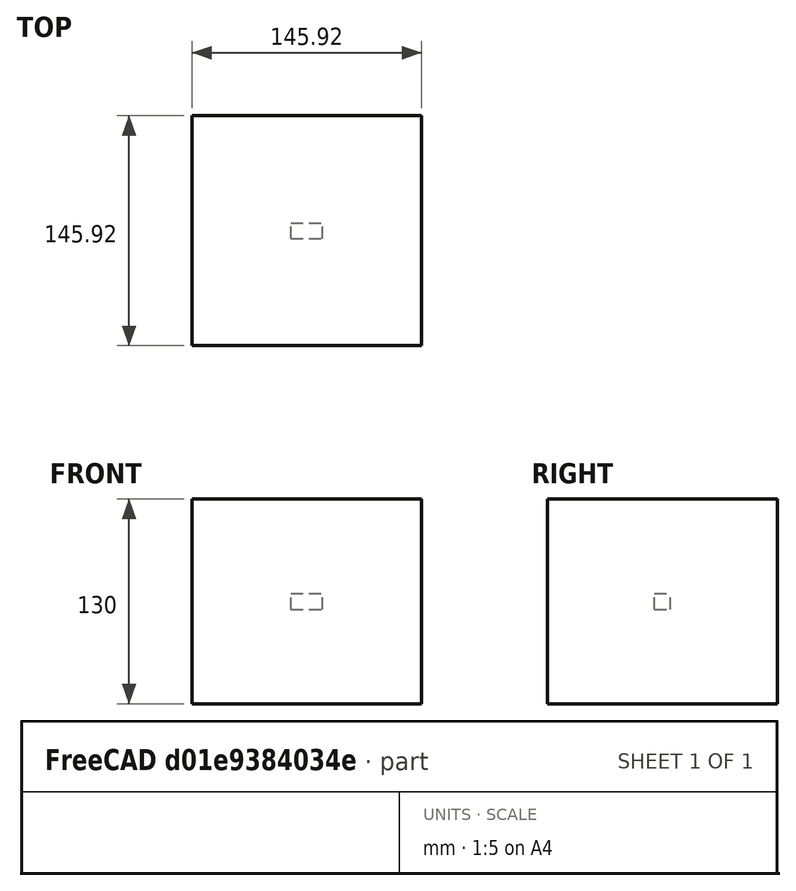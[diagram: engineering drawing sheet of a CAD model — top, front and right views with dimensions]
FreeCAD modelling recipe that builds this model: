
FCSTD DOCUMENT  (FreeCAD 0.20RUnknown)
Label: array-rotation-test-b
License: All rights reserved
objects: App::DocumentObjectGroupPython×1251, Part::FeaturePython×3, App::Part×3
note: 2 computed .brp shape members not serialized (recipe doc carries the construction recipe); baked Part::Feature solids carry a one-line shape summary decoded from their .brp

FEATURE [App::DocumentObjectGroupPython] HALFPI  # scripted group (container) (typed FeaturePython)
  name = HALFPI
  value = pi/2.
FEATURE [App::DocumentObjectGroupPython] PI  # scripted group (container) (typed FeaturePython)
  name = PI
  value = 1.*pi
FEATURE [App::DocumentObjectGroupPython] TWOPI  # scripted group (container) (typed FeaturePython)
  name = TWOPI
  value = 2.*pi
FEATURE [App::DocumentObjectGroupPython] Constants  # scripted group (container) (typed FeaturePython)
  Group = -> [HALFPI,PI,TWOPI]
FEATURE [App::DocumentObjectGroupPython] Variables  # scripted group (container) (typed FeaturePython)
FEATURE [App::DocumentObjectGroupPython] Quantities  # scripted group (container) (typed FeaturePython)
FEATURE [App::DocumentObjectGroupPython] Isotopes  # scripted group (container) (typed FeaturePython)
FEATURE [App::DocumentObjectGroupPython] Elements  # scripted group (container) (typed FeaturePython)
FEATURE [App::DocumentObjectGroupPython] Matrix  # scripted group (container) (typed FeaturePython)
FEATURE [App::DocumentObjectGroupPython] Surfaces  # scripted group (container) (typed FeaturePython)
FEATURE [App::DocumentObjectGroupPython] Opticals  # scripted group (container) (typed FeaturePython)
  Group = -> [Matrix,Surfaces]
FEATURE [App::DocumentObjectGroupPython] G4Isotopes  # scripted group (container) (typed FeaturePython)
FEATURE [App::DocumentObjectGroupPython] H_element  # scripted group (container) (typed FeaturePython)
  Z = 1
  atom_value = 1.008
  formula = H
  name = H_element
FEATURE [App::DocumentObjectGroupPython] He_element  # scripted group (container) (typed FeaturePython)
  Z = 2
  atom_value = 4.0026
  formula = He
  name = He_element
FEATURE [App::DocumentObjectGroupPython] Li_element  # scripted group (container) (typed FeaturePython)
  Z = 3
  atom_value = 6.94
  formula = Li
  name = Li_element
FEATURE [App::DocumentObjectGroupPython] Be_element  # scripted group (container) (typed FeaturePython)
  Z = 4
  atom_value = 9.01218
  formula = Be
  name = Be_element
FEATURE [App::DocumentObjectGroupPython] B_element  # scripted group (container) (typed FeaturePython)
  Z = 5
  atom_value = 10.81
  formula = B
  name = B_element
FEATURE [App::DocumentObjectGroupPython] C_element  # scripted group (container) (typed FeaturePython)
  Z = 6
  atom_value = 12.011
  formula = C
  name = C_element
FEATURE [App::DocumentObjectGroupPython] N_element  # scripted group (container) (typed FeaturePython)
  Z = 7
  atom_value = 14.007
  formula = N
  name = N_element
FEATURE [App::DocumentObjectGroupPython] O_element  # scripted group (container) (typed FeaturePython)
  Z = 8
  atom_value = 15.999
  formula = O
  name = O_element
FEATURE [App::DocumentObjectGroupPython] F_element  # scripted group (container) (typed FeaturePython)
  Z = 9
  atom_value = 18.9984
  formula = F
  name = F_element
FEATURE [App::DocumentObjectGroupPython] Ne_element  # scripted group (container) (typed FeaturePython)
  Z = 10
  atom_value = 20.1797
  formula = Ne
  name = Ne_element
FEATURE [App::DocumentObjectGroupPython] Na_element  # scripted group (container) (typed FeaturePython)
  Z = 11
  atom_value = 22.9898
  formula = Na
  name = Na_element
FEATURE [App::DocumentObjectGroupPython] Mg_element  # scripted group (container) (typed FeaturePython)
  Z = 12
  atom_value = 24.305
  formula = Mg
  name = Mg_element
FEATURE [App::DocumentObjectGroupPython] Al_element  # scripted group (container) (typed FeaturePython)
  Z = 13
  atom_value = 26.9815
  formula = Al
  name = Al_element
FEATURE [App::DocumentObjectGroupPython] Si_element  # scripted group (container) (typed FeaturePython)
  Z = 14
  atom_value = 28.085
  formula = Si
  name = Si_element
FEATURE [App::DocumentObjectGroupPython] P_element  # scripted group (container) (typed FeaturePython)
  Z = 15
  atom_value = 30.9738
  formula = P
  name = P_element
FEATURE [App::DocumentObjectGroupPython] S_element  # scripted group (container) (typed FeaturePython)
  Z = 16
  atom_value = 32.06
  formula = S
  name = S_element
FEATURE [App::DocumentObjectGroupPython] Cl_element  # scripted group (container) (typed FeaturePython)
  Z = 17
  atom_value = 35.45
  formula = Cl
  name = Cl_element
FEATURE [App::DocumentObjectGroupPython] Ar_element  # scripted group (container) (typed FeaturePython)
  Z = 18
  atom_value = 39.95
  formula = Ar
  name = Ar_element
FEATURE [App::DocumentObjectGroupPython] K_element  # scripted group (container) (typed FeaturePython)
  Z = 19
  atom_value = 39.0983
  formula = K
  name = K_element
FEATURE [App::DocumentObjectGroupPython] Ca_element  # scripted group (container) (typed FeaturePython)
  Z = 20
  atom_value = 40.078
  formula = Ca
  name = Ca_element
FEATURE [App::DocumentObjectGroupPython] Sc_element  # scripted group (container) (typed FeaturePython)
  Z = 21
  atom_value = 44.9559
  formula = Sc
  name = Sc_element
FEATURE [App::DocumentObjectGroupPython] Ti_element  # scripted group (container) (typed FeaturePython)
  Z = 22
  atom_value = 47.867
  formula = Ti
  name = Ti_element
FEATURE [App::DocumentObjectGroupPython] V_element  # scripted group (container) (typed FeaturePython)
  Z = 23
  atom_value = 50.9415
  formula = V
  name = V_element
FEATURE [App::DocumentObjectGroupPython] Cr_element  # scripted group (container) (typed FeaturePython)
  Z = 24
  atom_value = 51.9961
  formula = Cr
  name = Cr_element
FEATURE [App::DocumentObjectGroupPython] Mn_element  # scripted group (container) (typed FeaturePython)
  Z = 25
  atom_value = 54.938
  formula = Mn
  name = Mn_element
FEATURE [App::DocumentObjectGroupPython] Fe_element  # scripted group (container) (typed FeaturePython)
  Z = 26
  atom_value = 55.845
  formula = Fe
  name = Fe_element
FEATURE [App::DocumentObjectGroupPython] Co_element  # scripted group (container) (typed FeaturePython)
  Z = 27
  atom_value = 58.9332
  formula = Co
  name = Co_element
FEATURE [App::DocumentObjectGroupPython] Ni_element  # scripted group (container) (typed FeaturePython)
  Z = 28
  atom_value = 58.6934
  formula = Ni
  name = Ni_element
FEATURE [App::DocumentObjectGroupPython] Cu_element  # scripted group (container) (typed FeaturePython)
  Z = 29
  atom_value = 63.546
  formula = Cu
  name = Cu_element
FEATURE [App::DocumentObjectGroupPython] Zn_element  # scripted group (container) (typed FeaturePython)
  Z = 30
  atom_value = 65.38
  formula = Zn
  name = Zn_element
FEATURE [App::DocumentObjectGroupPython] Ga_element  # scripted group (container) (typed FeaturePython)
  Z = 31
  atom_value = 69.723
  formula = Ga
  name = Ga_element
FEATURE [App::DocumentObjectGroupPython] Ge_element  # scripted group (container) (typed FeaturePython)
  Z = 32
  atom_value = 72.63
  formula = Ge
  name = Ge_element
FEATURE [App::DocumentObjectGroupPython] As_element  # scripted group (container) (typed FeaturePython)
  Z = 33
  atom_value = 74.9216
  formula = As
  name = As_element
FEATURE [App::DocumentObjectGroupPython] Se_element  # scripted group (container) (typed FeaturePython)
  Z = 34
  atom_value = 78.971
  formula = Se
  name = Se_element
FEATURE [App::DocumentObjectGroupPython] Br_element  # scripted group (container) (typed FeaturePython)
  Z = 35
  atom_value = 79.904
  formula = Br
  name = Br_element
FEATURE [App::DocumentObjectGroupPython] Kr_element  # scripted group (container) (typed FeaturePython)
  Z = 36
  atom_value = 83.798
  formula = Kr
  name = Kr_element
FEATURE [App::DocumentObjectGroupPython] Rb_element  # scripted group (container) (typed FeaturePython)
  Z = 37
  atom_value = 85.4678
  formula = Rb
  name = Rb_element
FEATURE [App::DocumentObjectGroupPython] Sr_element  # scripted group (container) (typed FeaturePython)
  Z = 38
  atom_value = 87.62
  formula = Sr
  name = Sr_element
FEATURE [App::DocumentObjectGroupPython] Y_element  # scripted group (container) (typed FeaturePython)
  Z = 39
  atom_value = 88.9058
  formula = Y
  name = Y_element
FEATURE [App::DocumentObjectGroupPython] Zr_element  # scripted group (container) (typed FeaturePython)
  Z = 40
  atom_value = 91.224
  formula = Zr
  name = Zr_element
FEATURE [App::DocumentObjectGroupPython] Nb_element  # scripted group (container) (typed FeaturePython)
  Z = 41
  atom_value = 92.9064
  formula = Nb
  name = Nb_element
FEATURE [App::DocumentObjectGroupPython] Mo_element  # scripted group (container) (typed FeaturePython)
  Z = 42
  atom_value = 95.95
  formula = Mo
  name = Mo_element
FEATURE [App::DocumentObjectGroupPython] Tc_element  # scripted group (container) (typed FeaturePython)
  Z = 43
  atom_value = 97
  formula = Tc
  name = Tc_element
FEATURE [App::DocumentObjectGroupPython] Ru_element  # scripted group (container) (typed FeaturePython)
  Z = 44
  atom_value = 101.07
  formula = Ru
  name = Ru_element
FEATURE [App::DocumentObjectGroupPython] Rh_element  # scripted group (container) (typed FeaturePython)
  Z = 45
  atom_value = 102.905
  formula = Rh
  name = Rh_element
FEATURE [App::DocumentObjectGroupPython] Pd_element  # scripted group (container) (typed FeaturePython)
  Z = 46
  atom_value = 106.42
  formula = Pd
  name = Pd_element
FEATURE [App::DocumentObjectGroupPython] Ag_element  # scripted group (container) (typed FeaturePython)
  Z = 47
  atom_value = 107.868
  formula = Ag
  name = Ag_element
FEATURE [App::DocumentObjectGroupPython] Cd_element  # scripted group (container) (typed FeaturePython)
  Z = 48
  atom_value = 112.414
  formula = Cd
  name = Cd_element
FEATURE [App::DocumentObjectGroupPython] In_element  # scripted group (container) (typed FeaturePython)
  Z = 49
  atom_value = 114.818
  formula = In
  name = In_element
FEATURE [App::DocumentObjectGroupPython] Sn_element  # scripted group (container) (typed FeaturePython)
  Z = 50
  atom_value = 118.71
  formula = Sn
  name = Sn_element
FEATURE [App::DocumentObjectGroupPython] Sb_element  # scripted group (container) (typed FeaturePython)
  Z = 51
  atom_value = 121.76
  formula = Sb
  name = Sb_element
FEATURE [App::DocumentObjectGroupPython] Te_element  # scripted group (container) (typed FeaturePython)
  Z = 52
  atom_value = 127.6
  formula = Te
  name = Te_element
FEATURE [App::DocumentObjectGroupPython] I_element  # scripted group (container) (typed FeaturePython)
  Z = 53
  atom_value = 126.904
  formula = I
  name = I_element
FEATURE [App::DocumentObjectGroupPython] Xe_element  # scripted group (container) (typed FeaturePython)
  Z = 54
  atom_value = 131.293
  formula = Xe
  name = Xe_element
FEATURE [App::DocumentObjectGroupPython] Cs_element  # scripted group (container) (typed FeaturePython)
  Z = 55
  atom_value = 132.905
  formula = Cs
  name = Cs_element
FEATURE [App::DocumentObjectGroupPython] Ba_element  # scripted group (container) (typed FeaturePython)
  Z = 56
  atom_value = 137.327
  formula = Ba
  name = Ba_element
FEATURE [App::DocumentObjectGroupPython] La_element  # scripted group (container) (typed FeaturePython)
  Z = 57
  atom_value = 138.905
  formula = La
  name = La_element
FEATURE [App::DocumentObjectGroupPython] Ce_element  # scripted group (container) (typed FeaturePython)
  Z = 58
  atom_value = 140.116
  formula = Ce
  name = Ce_element
FEATURE [App::DocumentObjectGroupPython] Pr_element  # scripted group (container) (typed FeaturePython)
  Z = 59
  atom_value = 140.908
  formula = Pr
  name = Pr_element
FEATURE [App::DocumentObjectGroupPython] Nd_element  # scripted group (container) (typed FeaturePython)
  Z = 60
  atom_value = 144.242
  formula = Nd
  name = Nd_element
FEATURE [App::DocumentObjectGroupPython] Pm_element  # scripted group (container) (typed FeaturePython)
  Z = 61
  atom_value = 145
  formula = Pm
  name = Pm_element
FEATURE [App::DocumentObjectGroupPython] Sm_element  # scripted group (container) (typed FeaturePython)
  Z = 62
  atom_value = 150.36
  formula = Sm
  name = Sm_element
FEATURE [App::DocumentObjectGroupPython] Eu_element  # scripted group (container) (typed FeaturePython)
  Z = 63
  atom_value = 151.964
  formula = Eu
  name = Eu_element
FEATURE [App::DocumentObjectGroupPython] Gd_element  # scripted group (container) (typed FeaturePython)
  Z = 64
  atom_value = 157.25
  formula = Gd
  name = Gd_element
FEATURE [App::DocumentObjectGroupPython] Tb_element  # scripted group (container) (typed FeaturePython)
  Z = 65
  atom_value = 158.925
  formula = Tb
  name = Tb_element
FEATURE [App::DocumentObjectGroupPython] Dy_element  # scripted group (container) (typed FeaturePython)
  Z = 66
  atom_value = 162.5
  formula = Dy
  name = Dy_element
FEATURE [App::DocumentObjectGroupPython] Ho_element  # scripted group (container) (typed FeaturePython)
  Z = 67
  atom_value = 164.93
  formula = Ho
  name = Ho_element
FEATURE [App::DocumentObjectGroupPython] Er_element  # scripted group (container) (typed FeaturePython)
  Z = 68
  atom_value = 167.259
  formula = Er
  name = Er_element
FEATURE [App::DocumentObjectGroupPython] Tm_element  # scripted group (container) (typed FeaturePython)
  Z = 69
  atom_value = 168.934
  formula = Tm
  name = Tm_element
FEATURE [App::DocumentObjectGroupPython] Yb_element  # scripted group (container) (typed FeaturePython)
  Z = 70
  atom_value = 173.045
  formula = Yb
  name = Yb_element
FEATURE [App::DocumentObjectGroupPython] Lu_element  # scripted group (container) (typed FeaturePython)
  Z = 71
  atom_value = 174.967
  formula = Lu
  name = Lu_element
FEATURE [App::DocumentObjectGroupPython] Hf_element  # scripted group (container) (typed FeaturePython)
  Z = 72
  atom_value = 178.49
  formula = Hf
  name = Hf_element
FEATURE [App::DocumentObjectGroupPython] Ta_element  # scripted group (container) (typed FeaturePython)
  Z = 73
  atom_value = 180.948
  formula = Ta
  name = Ta_element
FEATURE [App::DocumentObjectGroupPython] W_element  # scripted group (container) (typed FeaturePython)
  Z = 74
  atom_value = 183.84
  formula = W
  name = W_element
FEATURE [App::DocumentObjectGroupPython] Re_element  # scripted group (container) (typed FeaturePython)
  Z = 75
  atom_value = 186.207
  formula = Re
  name = Re_element
FEATURE [App::DocumentObjectGroupPython] Os_element  # scripted group (container) (typed FeaturePython)
  Z = 76
  atom_value = 190.23
  formula = Os
  name = Os_element
FEATURE [App::DocumentObjectGroupPython] Ir_element  # scripted group (container) (typed FeaturePython)
  Z = 77
  atom_value = 192.217
  formula = Ir
  name = Ir_element
FEATURE [App::DocumentObjectGroupPython] Pt_element  # scripted group (container) (typed FeaturePython)
  Z = 78
  atom_value = 195.084
  formula = Pt
  name = Pt_element
FEATURE [App::DocumentObjectGroupPython] Au_element  # scripted group (container) (typed FeaturePython)
  Z = 79
  atom_value = 196.967
  formula = Au
  name = Au_element
FEATURE [App::DocumentObjectGroupPython] Hg_element  # scripted group (container) (typed FeaturePython)
  Z = 80
  atom_value = 200.592
  formula = Hg
  name = Hg_element
FEATURE [App::DocumentObjectGroupPython] Tl_element  # scripted group (container) (typed FeaturePython)
  Z = 81
  atom_value = 204.38
  formula = Tl
  name = Tl_element
FEATURE [App::DocumentObjectGroupPython] Pb_element  # scripted group (container) (typed FeaturePython)
  Z = 82
  atom_value = 207.2
  formula = Pb
  name = Pb_element
FEATURE [App::DocumentObjectGroupPython] Bi_element  # scripted group (container) (typed FeaturePython)
  Z = 83
  atom_value = 208.98
  formula = Bi
  name = Bi_element
FEATURE [App::DocumentObjectGroupPython] Po_element  # scripted group (container) (typed FeaturePython)
  Z = 84
  atom_value = 209
  formula = Po
  name = Po_element
FEATURE [App::DocumentObjectGroupPython] At_element  # scripted group (container) (typed FeaturePython)
  Z = 85
  atom_value = 210
  formula = At
  name = At_element
FEATURE [App::DocumentObjectGroupPython] Rn_element  # scripted group (container) (typed FeaturePython)
  Z = 86
  atom_value = 222
  formula = Rn
  name = Rn_element
FEATURE [App::DocumentObjectGroupPython] Fr_element  # scripted group (container) (typed FeaturePython)
  Z = 87
  atom_value = 223
  formula = Fr
  name = Fr_element
FEATURE [App::DocumentObjectGroupPython] Ra_element  # scripted group (container) (typed FeaturePython)
  Z = 88
  atom_value = 226
  formula = Ra
  name = Ra_element
FEATURE [App::DocumentObjectGroupPython] Ac_element  # scripted group (container) (typed FeaturePython)
  Z = 89
  atom_value = 227
  formula = Ac
  name = Ac_element
FEATURE [App::DocumentObjectGroupPython] Th_element  # scripted group (container) (typed FeaturePython)
  Z = 90
  atom_value = 232.038
  formula = Th
  name = Th_element
FEATURE [App::DocumentObjectGroupPython] Pa_element  # scripted group (container) (typed FeaturePython)
  Z = 91
  atom_value = 231.036
  formula = Pa
  name = Pa_element
FEATURE [App::DocumentObjectGroupPython] U_element  # scripted group (container) (typed FeaturePython)
  Z = 92
  atom_value = 238.029
  formula = U
  name = U_element
FEATURE [App::DocumentObjectGroupPython] Np_element  # scripted group (container) (typed FeaturePython)
  Z = 93
  atom_value = 237
  formula = Np
  name = Np_element
FEATURE [App::DocumentObjectGroupPython] Pu_element  # scripted group (container) (typed FeaturePython)
  Z = 94
  atom_value = 244
  formula = Pu
  name = Pu_element
FEATURE [App::DocumentObjectGroupPython] Am_element  # scripted group (container) (typed FeaturePython)
  Z = 95
  atom_value = 243
  formula = Am
  name = Am_element
FEATURE [App::DocumentObjectGroupPython] Cm_element  # scripted group (container) (typed FeaturePython)
  Z = 96
  atom_value = 247
  formula = Cm
  name = Cm_element
FEATURE [App::DocumentObjectGroupPython] Bk_element  # scripted group (container) (typed FeaturePython)
  Z = 97
  atom_value = 247
  formula = Bk
  name = Bk_element
FEATURE [App::DocumentObjectGroupPython] Cf_element  # scripted group (container) (typed FeaturePython)
  Z = 98
  atom_value = 251
  formula = Cf
  name = Cf_element
FEATURE [App::DocumentObjectGroupPython] G4Elements  # scripted group (container) (typed FeaturePython)
  Group = -> [H_element,He_element,Li_element,Be_element,B_element,C_element,N_element,O_element,F_element,Ne_element,Na_element,Mg_element,Al_element,Si_element,P_element,S_element,Cl_element,Ar_element,K_element,Ca_element,Sc_element,Ti_element,V_element,Cr_element,Mn_element,Fe_element,Co_element,Ni_element,Cu_element,Zn_element,Ga_element,Ge_element,As_element,Se_element,Br_element,Kr_element,Rb_element,+61 more]
FEATURE [App::DocumentObjectGroupPython] H_element001  label="H_element : 0.101"  # scripted group (container) (typed FeaturePython)
  n = 0.101327
FEATURE [App::DocumentObjectGroupPython] C_element001  label="C_element : 0.775"  # scripted group (container) (typed FeaturePython)
  n = 0.7755
FEATURE [App::DocumentObjectGroupPython] N_element001  label="N_element : 0.035"  # scripted group (container) (typed FeaturePython)
  n = 0.035057
FEATURE [App::DocumentObjectGroupPython] O_element001  label="O_element : 0.052"  # scripted group (container) (typed FeaturePython)
  n = 0.0523159
FEATURE [App::DocumentObjectGroupPython] F_element001  label="F_element : 0.017"  # scripted group (container) (typed FeaturePython)
  n = 0.017422
FEATURE [App::DocumentObjectGroupPython] Ca_element001  label="Ca_element : 0.018"  # scripted group (container) (typed FeaturePython)
  n = 0.018378
FEATURE [App::DocumentObjectGroupPython] G4_A_150_TISSUE  label="G4_A-150_TISSUE"  # scripted group (container) (typed FeaturePython)
  Dunit = g/cm3
  Dvalue = 1.127
  Group = -> [H_element001,C_element001,N_element001,O_element001,F_element001,Ca_element001]
  conduct = 2
  density = 1
  expand = 3
  formula = G4_A-150_TISSUE
  name = G4_A-150_TISSUE
  specific = 4
FEATURE [App::DocumentObjectGroupPython] C_element002  label="C_element : 3"  # scripted group (container) (typed FeaturePython)
  n = 3
  ref = C_element
FEATURE [App::DocumentObjectGroupPython] H_element002  label="H_element : 6"  # scripted group (container) (typed FeaturePython)
  n = 6
  ref = H_element
FEATURE [App::DocumentObjectGroupPython] O_element002  label="O_element : 1"  # scripted group (container) (typed FeaturePython)
  n = 1
  ref = O_element
FEATURE [App::DocumentObjectGroupPython] G4_ACETONE  # scripted group (container) (typed FeaturePython)
  Dunit = g/cm3
  Dvalue = 0.7899
  Group = -> [C_element002,H_element002,O_element002]
  conduct = 2
  density = 1
  expand = 3
  formula = G4_ACETONE
  name = G4_ACETONE
  specific = 4
FEATURE [App::DocumentObjectGroupPython] C_element003  label="C_element : 2"  # scripted group (container) (typed FeaturePython)
  n = 2
  ref = C_element
FEATURE [App::DocumentObjectGroupPython] H_element003  label="H_element : 2"  # scripted group (container) (typed FeaturePython)
  n = 2
  ref = H_element
FEATURE [App::DocumentObjectGroupPython] G4_ACETYLENE  # scripted group (container) (typed FeaturePython)
  Dunit = g/cm3
  Dvalue = 0.0010967
  Group = -> [C_element003,H_element003]
  conduct = 2
  density = 1
  expand = 3
  formula = G4_ACETYLENE
  name = G4_ACETYLENE
  specific = 4
FEATURE [App::DocumentObjectGroupPython] C_element004  label="C_element : 5"  # scripted group (container) (typed FeaturePython)
  n = 5
  ref = C_element
FEATURE [App::DocumentObjectGroupPython] H_element004  label="H_element : 5"  # scripted group (container) (typed FeaturePython)
  n = 5
  ref = H_element
FEATURE [App::DocumentObjectGroupPython] N_element002  label="N_element : 5"  # scripted group (container) (typed FeaturePython)
  n = 5
  ref = N_element
FEATURE [App::DocumentObjectGroupPython] G4_ADENINE  # scripted group (container) (typed FeaturePython)
  Dunit = g/cm3
  Dvalue = 1.6
  Group = -> [C_element004,H_element004,N_element002]
  conduct = 2
  density = 1
  expand = 3
  formula = G4_ADENINE
  name = G4_ADENINE
  specific = 4
FEATURE [App::DocumentObjectGroupPython] H_element005  label="H_element : 0.114"  # scripted group (container) (typed FeaturePython)
  n = 0.114
FEATURE [App::DocumentObjectGroupPython] C_element005  label="C_element : 0.598"  # scripted group (container) (typed FeaturePython)
  n = 0.598
FEATURE [App::DocumentObjectGroupPython] N_element003  label="N_element : 0.007"  # scripted group (container) (typed FeaturePython)
  n = 0.007
FEATURE [App::DocumentObjectGroupPython] O_element003  label="O_element : 0.278"  # scripted group (container) (typed FeaturePython)
  n = 0.278
FEATURE [App::DocumentObjectGroupPython] Na_element001  label="Na_element : 0.001"  # scripted group (container) (typed FeaturePython)
  n = 0.001
FEATURE [App::DocumentObjectGroupPython] S_element001  label="S_element : 0.001"  # scripted group (container) (typed FeaturePython)
  n = 0.001
FEATURE [App::DocumentObjectGroupPython] Cl_element001  label="Cl_element : 0.001"  # scripted group (container) (typed FeaturePython)
  n = 0.001
FEATURE [App::DocumentObjectGroupPython] G4_ADIPOSE_TISSUE_ICRP  # scripted group (container) (typed FeaturePython)
  Dunit = g/cm3
  Dvalue = 0.95
  Group = -> [H_element005,C_element005,N_element003,O_element003,Na_element001,S_element001,Cl_element001]
  conduct = 2
  density = 1
  expand = 3
  formula = G4_ADIPOSE_TISSUE_ICRP
  name = G4_ADIPOSE_TISSUE_ICRP
  specific = 4
FEATURE [App::DocumentObjectGroupPython] C_element006  label="C_element : 0.000"  # scripted group (container) (typed FeaturePython)
  n = 0.000124
FEATURE [App::DocumentObjectGroupPython] N_element004  label="N_element : 0.755"  # scripted group (container) (typed FeaturePython)
  n = 0.755268
FEATURE [App::DocumentObjectGroupPython] O_element004  label="O_element : 0.232"  # scripted group (container) (typed FeaturePython)
  n = 0.231781
FEATURE [App::DocumentObjectGroupPython] Ar_element001  label="Ar_element : 0.013"  # scripted group (container) (typed FeaturePython)
  n = 0.012827
FEATURE [App::DocumentObjectGroupPython] G4_AIR  # scripted group (container) (typed FeaturePython)
  Dunit = g/cm3
  Dvalue = 0.00120479
  Group = -> [C_element006,N_element004,O_element004,Ar_element001]
  conduct = 2
  density = 1
  expand = 3
  formula = G4_AIR
  name = G4_AIR
  specific = 4
FEATURE [App::DocumentObjectGroupPython] C_element007  label="C_element : 006"  # scripted group (container) (typed FeaturePython)
  n = 3
  ref = C_element
FEATURE [App::DocumentObjectGroupPython] H_element006  label="H_element : 7"  # scripted group (container) (typed FeaturePython)
  n = 7
  ref = H_element
FEATURE [App::DocumentObjectGroupPython] N_element005  label="N_element : 1"  # scripted group (container) (typed FeaturePython)
  n = 1
  ref = N_element
FEATURE [App::DocumentObjectGroupPython] O_element005  label="O_element : 2"  # scripted group (container) (typed FeaturePython)
  n = 2
  ref = O_element
FEATURE [App::DocumentObjectGroupPython] G4_ALANINE  # scripted group (container) (typed FeaturePython)
  Dunit = g/cm3
  Dvalue = 1.42
  Group = -> [C_element007,H_element006,N_element005,O_element005]
  conduct = 2
  density = 1
  expand = 3
  formula = G4_ALANINE
  name = G4_ALANINE
  specific = 4
FEATURE [App::DocumentObjectGroupPython] Al_element001  label="Al_element : 2"  # scripted group (container) (typed FeaturePython)
  n = 2
  ref = Al_element
FEATURE [App::DocumentObjectGroupPython] O_element006  label="O_element : 3"  # scripted group (container) (typed FeaturePython)
  n = 3
  ref = O_element
FEATURE [App::DocumentObjectGroupPython] G4_ALUMINUM_OXIDE  # scripted group (container) (typed FeaturePython)
  Dunit = g/cm3
  Dvalue = 3.97
  Group = -> [Al_element001,O_element006]
  conduct = 2
  density = 1
  expand = 3
  formula = G4_ALUMINUM_OXIDE
  name = G4_ALUMINUM_OXIDE
  specific = 4
FEATURE [App::DocumentObjectGroupPython] H_element007  label="H_element : 0.106"  # scripted group (container) (typed FeaturePython)
  n = 0.10593
FEATURE [App::DocumentObjectGroupPython] C_element008  label="C_element : 0.789"  # scripted group (container) (typed FeaturePython)
  n = 0.788974
FEATURE [App::DocumentObjectGroupPython] O_element007  label="O_element : 0.105"  # scripted group (container) (typed FeaturePython)
  n = 0.105096
FEATURE [App::DocumentObjectGroupPython] G4_AMBER  # scripted group (container) (typed FeaturePython)
  Dunit = g/cm3
  Dvalue = 1.1
  Group = -> [H_element007,C_element008,O_element007]
  conduct = 2
  density = 1
  expand = 3
  formula = G4_AMBER
  name = G4_AMBER
  specific = 4
FEATURE [App::DocumentObjectGroupPython] N_element006  label="N_element : 006"  # scripted group (container) (typed FeaturePython)
  n = 1
  ref = N_element
FEATURE [App::DocumentObjectGroupPython] H_element008  label="H_element : 3"  # scripted group (container) (typed FeaturePython)
  n = 3
  ref = H_element
FEATURE [App::DocumentObjectGroupPython] G4_AMMONIA  # scripted group (container) (typed FeaturePython)
  Dunit = g/cm3
  Dvalue = 0.000826019
  Group = -> [N_element006,H_element008]
  conduct = 2
  density = 1
  expand = 3
  formula = G4_AMMONIA
  name = G4_AMMONIA
  specific = 4
FEATURE [App::DocumentObjectGroupPython] C_element009  label="C_element : 6"  # scripted group (container) (typed FeaturePython)
  n = 6
  ref = C_element
FEATURE [App::DocumentObjectGroupPython] H_element009  label="H_element : 008"  # scripted group (container) (typed FeaturePython)
  n = 7
  ref = H_element
FEATURE [App::DocumentObjectGroupPython] N_element007  label="N_element : 007"  # scripted group (container) (typed FeaturePython)
  n = 1
  ref = N_element
FEATURE [App::DocumentObjectGroupPython] G4_ANILINE  # scripted group (container) (typed FeaturePython)
  Dunit = g/cm3
  Dvalue = 1.0235
  Group = -> [C_element009,H_element009,N_element007]
  conduct = 2
  density = 1
  expand = 3
  formula = G4_ANILINE
  name = G4_ANILINE
  specific = 4
FEATURE [App::DocumentObjectGroupPython] C_element010  label="C_element : 14"  # scripted group (container) (typed FeaturePython)
  n = 14
  ref = C_element
FEATURE [App::DocumentObjectGroupPython] H_element010  label="H_element : 10"  # scripted group (container) (typed FeaturePython)
  n = 10
  ref = H_element
FEATURE [App::DocumentObjectGroupPython] G4_ANTHRACENE  # scripted group (container) (typed FeaturePython)
  Dunit = g/cm3
  Dvalue = 1.283
  Group = -> [C_element010,H_element010]
  conduct = 2
  density = 1
  expand = 3
  formula = G4_ANTHRACENE
  name = G4_ANTHRACENE
  specific = 4
FEATURE [App::DocumentObjectGroupPython] H_element011  label="H_element : 0.065"  # scripted group (container) (typed FeaturePython)
  n = 0.0654709
FEATURE [App::DocumentObjectGroupPython] C_element011  label="C_element : 0.537"  # scripted group (container) (typed FeaturePython)
  n = 0.536944
FEATURE [App::DocumentObjectGroupPython] N_element008  label="N_element : 0.021"  # scripted group (container) (typed FeaturePython)
  n = 0.0215
FEATURE [App::DocumentObjectGroupPython] O_element008  label="O_element : 0.032"  # scripted group (container) (typed FeaturePython)
  n = 0.032085
FEATURE [App::DocumentObjectGroupPython] F_element002  label="F_element : 0.167"  # scripted group (container) (typed FeaturePython)
  n = 0.167411
FEATURE [App::DocumentObjectGroupPython] Ca_element002  label="Ca_element : 0.177"  # scripted group (container) (typed FeaturePython)
  n = 0.176589
FEATURE [App::DocumentObjectGroupPython] G4_B_100_BONE  label="G4_B-100_BONE"  # scripted group (container) (typed FeaturePython)
  Dunit = g/cm3
  Dvalue = 1.45
  Group = -> [H_element011,C_element011,N_element008,O_element008,F_element002,Ca_element002]
  conduct = 2
  density = 1
  expand = 3
  formula = G4_B-100_BONE
  name = G4_B-100_BONE
  specific = 4
FEATURE [App::DocumentObjectGroupPython] H_element012  label="H_element : 0.057"  # scripted group (container) (typed FeaturePython)
  n = 0.057441
FEATURE [App::DocumentObjectGroupPython] C_element012  label="C_element : 0.790"  # scripted group (container) (typed FeaturePython)
  n = 0.774591
FEATURE [App::DocumentObjectGroupPython] O_element009  label="O_element : 0.168"  # scripted group (container) (typed FeaturePython)
  n = 0.167968
FEATURE [App::DocumentObjectGroupPython] G4_BAKELITE  # scripted group (container) (typed FeaturePython)
  Dunit = g/cm3
  Dvalue = 1.25
  Group = -> [H_element012,C_element012,O_element009]
  conduct = 2
  density = 1
  expand = 3
  formula = G4_BAKELITE
  name = G4_BAKELITE
  specific = 4
FEATURE [App::DocumentObjectGroupPython] Ba_element001  label="Ba_element : 1"  # scripted group (container) (typed FeaturePython)
  n = 1
  ref = Ba_element
FEATURE [App::DocumentObjectGroupPython] F_element003  label="F_element : 2"  # scripted group (container) (typed FeaturePython)
  n = 2
  ref = F_element
FEATURE [App::DocumentObjectGroupPython] G4_BARIUM_FLUORIDE  # scripted group (container) (typed FeaturePython)
  Dunit = g/cm3
  Dvalue = 4.89
  Group = -> [Ba_element001,F_element003]
  conduct = 2
  density = 1
  expand = 3
  formula = G4_BARIUM_FLUORIDE
  name = G4_BARIUM_FLUORIDE
  specific = 4
FEATURE [App::DocumentObjectGroupPython] Ba_element002  label="Ba_element : 002"  # scripted group (container) (typed FeaturePython)
  n = 1
  ref = Ba_element
FEATURE [App::DocumentObjectGroupPython] S_element002  label="S_element : 1"  # scripted group (container) (typed FeaturePython)
  n = 1
  ref = S_element
FEATURE [App::DocumentObjectGroupPython] O_element010  label="O_element : 4"  # scripted group (container) (typed FeaturePython)
  n = 4
  ref = O_element
FEATURE [App::DocumentObjectGroupPython] G4_BARIUM_SULFATE  # scripted group (container) (typed FeaturePython)
  Dunit = g/cm3
  Dvalue = 4.5
  Group = -> [Ba_element002,S_element002,O_element010]
  conduct = 2
  density = 1
  expand = 3
  formula = G4_BARIUM_SULFATE
  name = G4_BARIUM_SULFATE
  specific = 4
FEATURE [App::DocumentObjectGroupPython] C_element013  label="C_element : 007"  # scripted group (container) (typed FeaturePython)
  n = 6
  ref = C_element
FEATURE [App::DocumentObjectGroupPython] H_element013  label="H_element : 009"  # scripted group (container) (typed FeaturePython)
  n = 6
  ref = H_element
FEATURE [App::DocumentObjectGroupPython] G4_BENZENE  # scripted group (container) (typed FeaturePython)
  Dunit = g/cm3
  Dvalue = 0.87865
  Group = -> [C_element013,H_element013]
  conduct = 2
  density = 1
  expand = 3
  formula = G4_BENZENE
  name = G4_BENZENE
  specific = 4
FEATURE [App::DocumentObjectGroupPython] Be_element001  label="Be_element : 1"  # scripted group (container) (typed FeaturePython)
  n = 1
  ref = Be_element
FEATURE [App::DocumentObjectGroupPython] O_element011  label="O_element : 005"  # scripted group (container) (typed FeaturePython)
  n = 1
  ref = O_element
FEATURE [App::DocumentObjectGroupPython] G4_BERYLLIUM_OXIDE  # scripted group (container) (typed FeaturePython)
  Dunit = g/cm3
  Dvalue = 3.01
  Group = -> [Be_element001,O_element011]
  conduct = 2
  density = 1
  expand = 3
  formula = G4_BERYLLIUM_OXIDE
  name = G4_BERYLLIUM_OXIDE
  specific = 4
FEATURE [App::DocumentObjectGroupPython] Bi_element001  label="Bi_element : 4"  # scripted group (container) (typed FeaturePython)
  n = 4
  ref = Bi_element
FEATURE [App::DocumentObjectGroupPython] Ge_element001  label="Ge_element : 3"  # scripted group (container) (typed FeaturePython)
  n = 3
  ref = Ge_element
FEATURE [App::DocumentObjectGroupPython] O_element012  label="O_element : 12"  # scripted group (container) (typed FeaturePython)
  n = 12
  ref = O_element
FEATURE [App::DocumentObjectGroupPython] G4_BGO  # scripted group (container) (typed FeaturePython)
  Dunit = g/cm3
  Dvalue = 7.13
  Group = -> [Bi_element001,Ge_element001,O_element012]
  conduct = 2
  density = 1
  expand = 3
  formula = G4_BGO
  name = G4_BGO
  specific = 4
FEATURE [App::DocumentObjectGroupPython] H_element014  label="H_element : 0.102"  # scripted group (container) (typed FeaturePython)
  n = 0.102
FEATURE [App::DocumentObjectGroupPython] C_element014  label="C_element : 0.110"  # scripted group (container) (typed FeaturePython)
  n = 0.11
FEATURE [App::DocumentObjectGroupPython] N_element009  label="N_element : 0.033"  # scripted group (container) (typed FeaturePython)
  n = 0.033
FEATURE [App::DocumentObjectGroupPython] O_element013  label="O_element : 0.745"  # scripted group (container) (typed FeaturePython)
  n = 0.745
FEATURE [App::DocumentObjectGroupPython] Na_element002  label="Na_element : 0.002"  # scripted group (container) (typed FeaturePython)
  n = 0.001
FEATURE [App::DocumentObjectGroupPython] P_element001  label="P_element : 0.001"  # scripted group (container) (typed FeaturePython)
  n = 0.001
FEATURE [App::DocumentObjectGroupPython] S_element003  label="S_element : 0.002"  # scripted group (container) (typed FeaturePython)
  n = 0.002
FEATURE [App::DocumentObjectGroupPython] Cl_element002  label="Cl_element : 0.003"  # scripted group (container) (typed FeaturePython)
  n = 0.003
FEATURE [App::DocumentObjectGroupPython] K_element001  label="K_element : 0.002"  # scripted group (container) (typed FeaturePython)
  n = 0.002
FEATURE [App::DocumentObjectGroupPython] Fe_element001  label="Fe_element : 0.001"  # scripted group (container) (typed FeaturePython)
  n = 0.001
FEATURE [App::DocumentObjectGroupPython] G4_BLOOD_ICRP  # scripted group (container) (typed FeaturePython)
  Dunit = g/cm3
  Dvalue = 1.06
  Group = -> [H_element014,C_element014,N_element009,O_element013,Na_element002,P_element001,S_element003,Cl_element002,K_element001,Fe_element001]
  conduct = 2
  density = 1
  expand = 3
  formula = G4_BLOOD_ICRP
  name = G4_BLOOD_ICRP
  specific = 4
FEATURE [App::DocumentObjectGroupPython] H_element015  label="H_element : 0.064"  # scripted group (container) (typed FeaturePython)
  n = 0.064
FEATURE [App::DocumentObjectGroupPython] C_element015  label="C_element : 0.278"  # scripted group (container) (typed FeaturePython)
  n = 0.278
FEATURE [App::DocumentObjectGroupPython] N_element010  label="N_element : 0.027"  # scripted group (container) (typed FeaturePython)
  n = 0.027
FEATURE [App::DocumentObjectGroupPython] O_element014  label="O_element : 0.410"  # scripted group (container) (typed FeaturePython)
  n = 0.41
FEATURE [App::DocumentObjectGroupPython] Mg_element001  label="Mg_element : 0.002"  # scripted group (container) (typed FeaturePython)
  n = 0.002
FEATURE [App::DocumentObjectGroupPython] P_element002  label="P_element : 0.070"  # scripted group (container) (typed FeaturePython)
  n = 0.07
FEATURE [App::DocumentObjectGroupPython] S_element004  label="S_element : 0.003"  # scripted group (container) (typed FeaturePython)
  n = 0.002
FEATURE [App::DocumentObjectGroupPython] Ca_element003  label="Ca_element : 0.147"  # scripted group (container) (typed FeaturePython)
  n = 0.147
FEATURE [App::DocumentObjectGroupPython] G4_BONE_COMPACT_ICRU  # scripted group (container) (typed FeaturePython)
  Dunit = g/cm3
  Dvalue = 1.85
  Group = -> [H_element015,C_element015,N_element010,O_element014,Mg_element001,P_element002,S_element004,Ca_element003]
  conduct = 2
  density = 1
  expand = 3
  formula = G4_BONE_COMPACT_ICRU
  name = G4_BONE_COMPACT_ICRU
  specific = 4
FEATURE [App::DocumentObjectGroupPython] H_element016  label="H_element : 0.034"  # scripted group (container) (typed FeaturePython)
  n = 0.034
FEATURE [App::DocumentObjectGroupPython] C_element016  label="C_element : 0.155"  # scripted group (container) (typed FeaturePython)
  n = 0.155
FEATURE [App::DocumentObjectGroupPython] N_element011  label="N_element : 0.042"  # scripted group (container) (typed FeaturePython)
  n = 0.042
FEATURE [App::DocumentObjectGroupPython] O_element015  label="O_element : 0.435"  # scripted group (container) (typed FeaturePython)
  n = 0.435
FEATURE [App::DocumentObjectGroupPython] Na_element003  label="Na_element : 0.003"  # scripted group (container) (typed FeaturePython)
  n = 0.001
FEATURE [App::DocumentObjectGroupPython] Mg_element002  label="Mg_element : 0.003"  # scripted group (container) (typed FeaturePython)
  n = 0.002
FEATURE [App::DocumentObjectGroupPython] P_element003  label="P_element : 0.103"  # scripted group (container) (typed FeaturePython)
  n = 0.103
FEATURE [App::DocumentObjectGroupPython] S_element005  label="S_element : 0.004"  # scripted group (container) (typed FeaturePython)
  n = 0.003
FEATURE [App::DocumentObjectGroupPython] Ca_element004  label="Ca_element : 0.225"  # scripted group (container) (typed FeaturePython)
  n = 0.225
FEATURE [App::DocumentObjectGroupPython] G4_BONE_CORTICAL_ICRP  # scripted group (container) (typed FeaturePython)
  Dunit = g/cm3
  Dvalue = 1.92
  Group = -> [H_element016,C_element016,N_element011,O_element015,Na_element003,Mg_element002,P_element003,S_element005,Ca_element004]
  conduct = 2
  density = 1
  expand = 3
  formula = G4_BONE_CORTICAL_ICRP
  name = G4_BONE_CORTICAL_ICRP
  specific = 4
FEATURE [App::DocumentObjectGroupPython] B_element001  label="B_element : 4"  # scripted group (container) (typed FeaturePython)
  n = 4
  ref = B_element
FEATURE [App::DocumentObjectGroupPython] C_element017  label="C_element : 1"  # scripted group (container) (typed FeaturePython)
  n = 1
  ref = C_element
FEATURE [App::DocumentObjectGroupPython] G4_BORON_CARBIDE  # scripted group (container) (typed FeaturePython)
  Dunit = g/cm3
  Dvalue = 2.52
  Group = -> [B_element001,C_element017]
  conduct = 2
  density = 1
  expand = 3
  formula = G4_BORON_CARBIDE
  name = G4_BORON_CARBIDE
  specific = 4
FEATURE [App::DocumentObjectGroupPython] B_element002  label="B_element : 2"  # scripted group (container) (typed FeaturePython)
  n = 2
  ref = B_element
FEATURE [App::DocumentObjectGroupPython] O_element016  label="O_element : 006"  # scripted group (container) (typed FeaturePython)
  n = 3
  ref = O_element
FEATURE [App::DocumentObjectGroupPython] G4_BORON_OXIDE  # scripted group (container) (typed FeaturePython)
  Dunit = g/cm3
  Dvalue = 1.812
  Group = -> [B_element002,O_element016]
  conduct = 2
  density = 1
  expand = 3
  formula = G4_BORON_OXIDE
  name = G4_BORON_OXIDE
  specific = 4
FEATURE [App::DocumentObjectGroupPython] H_element017  label="H_element : 0.107"  # scripted group (container) (typed FeaturePython)
  n = 0.107
FEATURE [App::DocumentObjectGroupPython] C_element018  label="C_element : 0.145"  # scripted group (container) (typed FeaturePython)
  n = 0.145
FEATURE [App::DocumentObjectGroupPython] N_element012  label="N_element : 0.022"  # scripted group (container) (typed FeaturePython)
  n = 0.022
FEATURE [App::DocumentObjectGroupPython] O_element017  label="O_element : 0.712"  # scripted group (container) (typed FeaturePython)
  n = 0.712
FEATURE [App::DocumentObjectGroupPython] Na_element004  label="Na_element : 0.004"  # scripted group (container) (typed FeaturePython)
  n = 0.002
FEATURE [App::DocumentObjectGroupPython] P_element004  label="P_element : 0.004"  # scripted group (container) (typed FeaturePython)
  n = 0.004
FEATURE [App::DocumentObjectGroupPython] S_element006  label="S_element : 0.005"  # scripted group (container) (typed FeaturePython)
  n = 0.002
FEATURE [App::DocumentObjectGroupPython] Cl_element003  label="Cl_element : 0.004"  # scripted group (container) (typed FeaturePython)
  n = 0.003
FEATURE [App::DocumentObjectGroupPython] K_element002  label="K_element : 0.003"  # scripted group (container) (typed FeaturePython)
  n = 0.003
FEATURE [App::DocumentObjectGroupPython] G4_BRAIN_ICRP  # scripted group (container) (typed FeaturePython)
  Dunit = g/cm3
  Dvalue = 1.04
  Group = -> [H_element017,C_element018,N_element012,O_element017,Na_element004,P_element004,S_element006,Cl_element003,K_element002]
  conduct = 2
  density = 1
  expand = 3
  formula = G4_BRAIN_ICRP
  name = G4_BRAIN_ICRP
  specific = 4
FEATURE [App::DocumentObjectGroupPython] C_element019  label="C_element : 4"  # scripted group (container) (typed FeaturePython)
  n = 4
  ref = C_element
FEATURE [App::DocumentObjectGroupPython] H_element018  label="H_element : 010"  # scripted group (container) (typed FeaturePython)
  n = 10
  ref = H_element
FEATURE [App::DocumentObjectGroupPython] G4_BUTANE  # scripted group (container) (typed FeaturePython)
  Dunit = g/cm3
  Dvalue = 0.00249343
  Group = -> [C_element019,H_element018]
  conduct = 2
  density = 1
  expand = 3
  formula = G4_BUTANE
  name = G4_BUTANE
  specific = 4
FEATURE [App::DocumentObjectGroupPython] C_element020  label="C_element : 008"  # scripted group (container) (typed FeaturePython)
  n = 4
  ref = C_element
FEATURE [App::DocumentObjectGroupPython] H_element019  label="H_element : 011"  # scripted group (container) (typed FeaturePython)
  n = 10
  ref = H_element
FEATURE [App::DocumentObjectGroupPython] O_element018  label="O_element : 007"  # scripted group (container) (typed FeaturePython)
  n = 1
  ref = O_element
FEATURE [App::DocumentObjectGroupPython] G4_N_BUTYL_ALCOHOL  label="G4_N-BUTYL_ALCOHOL"  # scripted group (container) (typed FeaturePython)
  Dunit = g/cm3
  Dvalue = 0.8098
  Group = -> [C_element020,H_element019,O_element018]
  conduct = 2
  density = 1
  expand = 3
  formula = G4_N-BUTYL_ALCOHOL
  name = G4_N-BUTYL_ALCOHOL
  specific = 4
FEATURE [App::DocumentObjectGroupPython] H_element020  label="H_element : 0.025"  # scripted group (container) (typed FeaturePython)
  n = 0.02468
FEATURE [App::DocumentObjectGroupPython] C_element021  label="C_element : 0.502"  # scripted group (container) (typed FeaturePython)
  n = 0.501611
FEATURE [App::DocumentObjectGroupPython] O_element019  label="O_element : 0.005"  # scripted group (container) (typed FeaturePython)
  n = 0.004527
FEATURE [App::DocumentObjectGroupPython] F_element004  label="F_element : 0.465"  # scripted group (container) (typed FeaturePython)
  n = 0.465209
FEATURE [App::DocumentObjectGroupPython] Si_element001  label="Si_element : 0.004"  # scripted group (container) (typed FeaturePython)
  n = 0.003973
FEATURE [App::DocumentObjectGroupPython] G4_C_552  label="G4_C-552"  # scripted group (container) (typed FeaturePython)
  Dunit = g/cm3
  Dvalue = 1.76
  Group = -> [H_element020,C_element021,O_element019,F_element004,Si_element001]
  conduct = 2
  density = 1
  expand = 3
  formula = G4_C-552
  name = G4_C-552
  specific = 4
FEATURE [App::DocumentObjectGroupPython] Cd_element001  label="Cd_element : 1"  # scripted group (container) (typed FeaturePython)
  n = 1
  ref = Cd_element
FEATURE [App::DocumentObjectGroupPython] Te_element001  label="Te_element : 1"  # scripted group (container) (typed FeaturePython)
  n = 1
  ref = Te_element
FEATURE [App::DocumentObjectGroupPython] G4_CADMIUM_TELLURIDE  # scripted group (container) (typed FeaturePython)
  Dunit = g/cm3
  Dvalue = 6.2
  Group = -> [Cd_element001,Te_element001]
  conduct = 2
  density = 1
  expand = 3
  formula = G4_CADMIUM_TELLURIDE
  name = G4_CADMIUM_TELLURIDE
  specific = 4
FEATURE [App::DocumentObjectGroupPython] Cd_element002  label="Cd_element : 002"  # scripted group (container) (typed FeaturePython)
  n = 1
  ref = Cd_element
FEATURE [App::DocumentObjectGroupPython] W_element001  label="W_element : 1"  # scripted group (container) (typed FeaturePython)
  n = 1
  ref = W_element
FEATURE [App::DocumentObjectGroupPython] O_element020  label="O_element : 008"  # scripted group (container) (typed FeaturePython)
  n = 4
  ref = O_element
FEATURE [App::DocumentObjectGroupPython] G4_CADMIUM_TUNGSTATE  # scripted group (container) (typed FeaturePython)
  Dunit = g/cm3
  Dvalue = 7.9
  Group = -> [Cd_element002,W_element001,O_element020]
  conduct = 2
  density = 1
  expand = 3
  formula = G4_CADMIUM_TUNGSTATE
  name = G4_CADMIUM_TUNGSTATE
  specific = 4
FEATURE [App::DocumentObjectGroupPython] Ca_element005  label="Ca_element : 1"  # scripted group (container) (typed FeaturePython)
  n = 1
  ref = Ca_element
FEATURE [App::DocumentObjectGroupPython] C_element022  label="C_element : 009"  # scripted group (container) (typed FeaturePython)
  n = 1
  ref = C_element
FEATURE [App::DocumentObjectGroupPython] O_element021  label="O_element : 009"  # scripted group (container) (typed FeaturePython)
  n = 3
  ref = O_element
FEATURE [App::DocumentObjectGroupPython] G4_CALCIUM_CARBONATE  # scripted group (container) (typed FeaturePython)
  Dunit = g/cm3
  Dvalue = 2.8
  Group = -> [Ca_element005,C_element022,O_element021]
  conduct = 2
  density = 1
  expand = 3
  formula = G4_CALCIUM_CARBONATE
  name = G4_CALCIUM_CARBONATE
  specific = 4
FEATURE [App::DocumentObjectGroupPython] Ca_element006  label="Ca_element : 002"  # scripted group (container) (typed FeaturePython)
  n = 1
  ref = Ca_element
FEATURE [App::DocumentObjectGroupPython] F_element005  label="F_element : 003"  # scripted group (container) (typed FeaturePython)
  n = 2
  ref = F_element
FEATURE [App::DocumentObjectGroupPython] G4_CALCIUM_FLUORIDE  # scripted group (container) (typed FeaturePython)
  Dunit = g/cm3
  Dvalue = 3.18
  Group = -> [Ca_element006,F_element005]
  conduct = 2
  density = 1
  expand = 3
  formula = G4_CALCIUM_FLUORIDE
  name = G4_CALCIUM_FLUORIDE
  specific = 4
FEATURE [App::DocumentObjectGroupPython] Ca_element007  label="Ca_element : 003"  # scripted group (container) (typed FeaturePython)
  n = 1
  ref = Ca_element
FEATURE [App::DocumentObjectGroupPython] O_element022  label="O_element : 010"  # scripted group (container) (typed FeaturePython)
  n = 1
  ref = O_element
FEATURE [App::DocumentObjectGroupPython] G4_CALCIUM_OXIDE  # scripted group (container) (typed FeaturePython)
  Dunit = g/cm3
  Dvalue = 3.3
  Group = -> [Ca_element007,O_element022]
  conduct = 2
  density = 1
  expand = 3
  formula = G4_CALCIUM_OXIDE
  name = G4_CALCIUM_OXIDE
  specific = 4
FEATURE [App::DocumentObjectGroupPython] Ca_element008  label="Ca_element : 004"  # scripted group (container) (typed FeaturePython)
  n = 1
  ref = Ca_element
FEATURE [App::DocumentObjectGroupPython] S_element007  label="S_element : 002"  # scripted group (container) (typed FeaturePython)
  n = 1
  ref = S_element
FEATURE [App::DocumentObjectGroupPython] O_element023  label="O_element : 011"  # scripted group (container) (typed FeaturePython)
  n = 4
  ref = O_element
FEATURE [App::DocumentObjectGroupPython] G4_CALCIUM_SULFATE  # scripted group (container) (typed FeaturePython)
  Dunit = g/cm3
  Dvalue = 2.96
  Group = -> [Ca_element008,S_element007,O_element023]
  conduct = 2
  density = 1
  expand = 3
  formula = G4_CALCIUM_SULFATE
  name = G4_CALCIUM_SULFATE
  specific = 4
FEATURE [App::DocumentObjectGroupPython] Ca_element009  label="Ca_element : 005"  # scripted group (container) (typed FeaturePython)
  n = 1
  ref = Ca_element
FEATURE [App::DocumentObjectGroupPython] W_element002  label="W_element : 002"  # scripted group (container) (typed FeaturePython)
  n = 1
  ref = W_element
FEATURE [App::DocumentObjectGroupPython] O_element024  label="O_element : 012"  # scripted group (container) (typed FeaturePython)
  n = 4
  ref = O_element
FEATURE [App::DocumentObjectGroupPython] G4_CALCIUM_TUNGSTATE  # scripted group (container) (typed FeaturePython)
  Dunit = g/cm3
  Dvalue = 6.062
  Group = -> [Ca_element009,W_element002,O_element024]
  conduct = 2
  density = 1
  expand = 3
  formula = G4_CALCIUM_TUNGSTATE
  name = G4_CALCIUM_TUNGSTATE
  specific = 4
FEATURE [App::DocumentObjectGroupPython] C_element023  label="C_element : 010"  # scripted group (container) (typed FeaturePython)
  n = 1
  ref = C_element
FEATURE [App::DocumentObjectGroupPython] O_element025  label="O_element : 013"  # scripted group (container) (typed FeaturePython)
  n = 2
  ref = O_element
FEATURE [App::DocumentObjectGroupPython] G4_CARBON_DIOXIDE  # scripted group (container) (typed FeaturePython)
  Dunit = g/cm3
  Dvalue = 0.00184212
  Group = -> [C_element023,O_element025]
  conduct = 2
  density = 1
  expand = 3
  formula = G4_CARBON_DIOXIDE
  name = G4_CARBON_DIOXIDE
  specific = 4
FEATURE [App::DocumentObjectGroupPython] C_element024  label="C_element : 011"  # scripted group (container) (typed FeaturePython)
  n = 1
  ref = C_element
FEATURE [App::DocumentObjectGroupPython] Cl_element004  label="Cl_element : 4"  # scripted group (container) (typed FeaturePython)
  n = 4
  ref = Cl_element
FEATURE [App::DocumentObjectGroupPython] G4_CARBON_TETRACHLORIDE  # scripted group (container) (typed FeaturePython)
  Dunit = g/cm3
  Dvalue = 1.594
  Group = -> [C_element024,Cl_element004]
  conduct = 2
  density = 1
  expand = 3
  formula = G4_CARBON_TETRACHLORIDE
  name = G4_CARBON_TETRACHLORIDE
  specific = 4
FEATURE [App::DocumentObjectGroupPython] C_element025  label="C_element : 012"  # scripted group (container) (typed FeaturePython)
  n = 6
  ref = C_element
FEATURE [App::DocumentObjectGroupPython] H_element021  label="H_element : 012"  # scripted group (container) (typed FeaturePython)
  n = 10
  ref = H_element
FEATURE [App::DocumentObjectGroupPython] O_element026  label="O_element : 5"  # scripted group (container) (typed FeaturePython)
  n = 5
  ref = O_element
FEATURE [App::DocumentObjectGroupPython] G4_CELLULOSE_CELLOPHANE  # scripted group (container) (typed FeaturePython)
  Dunit = g/cm3
  Dvalue = 1.42
  Group = -> [C_element025,H_element021,O_element026]
  conduct = 2
  density = 1
  expand = 3
  formula = G4_CELLULOSE_CELLOPHANE
  name = G4_CELLULOSE_CELLOPHANE
  specific = 4
FEATURE [App::DocumentObjectGroupPython] H_element022  label="H_element : 0.067"  # scripted group (container) (typed FeaturePython)
  n = 0.067125
FEATURE [App::DocumentObjectGroupPython] C_element026  label="C_element : 0.545"  # scripted group (container) (typed FeaturePython)
  n = 0.545403
FEATURE [App::DocumentObjectGroupPython] O_element027  label="O_element : 0.387"  # scripted group (container) (typed FeaturePython)
  n = 0.387472
FEATURE [App::DocumentObjectGroupPython] G4_CELLULOSE_BUTYRATE  # scripted group (container) (typed FeaturePython)
  Dunit = g/cm3
  Dvalue = 1.2
  Group = -> [H_element022,C_element026,O_element027]
  conduct = 2
  density = 1
  expand = 3
  formula = G4_CELLULOSE_BUTYRATE
  name = G4_CELLULOSE_BUTYRATE
  specific = 4
FEATURE [App::DocumentObjectGroupPython] H_element023  label="H_element : 0.029"  # scripted group (container) (typed FeaturePython)
  n = 0.029216
FEATURE [App::DocumentObjectGroupPython] C_element027  label="C_element : 0.271"  # scripted group (container) (typed FeaturePython)
  n = 0.271296
FEATURE [App::DocumentObjectGroupPython] N_element013  label="N_element : 0.121"  # scripted group (container) (typed FeaturePython)
  n = 0.121276
FEATURE [App::DocumentObjectGroupPython] O_element028  label="O_element : 0.578"  # scripted group (container) (typed FeaturePython)
  n = 0.578212
FEATURE [App::DocumentObjectGroupPython] G4_CELLULOSE_NITRATE  # scripted group (container) (typed FeaturePython)
  Dunit = g/cm3
  Dvalue = 1.49
  Group = -> [H_element023,C_element027,N_element013,O_element028]
  conduct = 2
  density = 1
  expand = 3
  formula = G4_CELLULOSE_NITRATE
  name = G4_CELLULOSE_NITRATE
  specific = 4
FEATURE [App::DocumentObjectGroupPython] H_element024  label="H_element : 0.108"  # scripted group (container) (typed FeaturePython)
  n = 0.107596
FEATURE [App::DocumentObjectGroupPython] N_element014  label="N_element : 0.001"  # scripted group (container) (typed FeaturePython)
  n = 0.0008
FEATURE [App::DocumentObjectGroupPython] O_element029  label="O_element : 0.875"  # scripted group (container) (typed FeaturePython)
  n = 0.874976
FEATURE [App::DocumentObjectGroupPython] S_element008  label="S_element : 0.015"  # scripted group (container) (typed FeaturePython)
  n = 0.014627
FEATURE [App::DocumentObjectGroupPython] Ce_element001  label="Ce_element : 0.002"  # scripted group (container) (typed FeaturePython)
  n = 0.002001
FEATURE [App::DocumentObjectGroupPython] G4_CERIC_SULFATE  # scripted group (container) (typed FeaturePython)
  Dunit = g/cm3
  Dvalue = 1.03
  Group = -> [H_element024,N_element014,O_element029,S_element008,Ce_element001]
  conduct = 2
  density = 1
  expand = 3
  formula = G4_CERIC_SULFATE
  name = G4_CERIC_SULFATE
  specific = 4
FEATURE [App::DocumentObjectGroupPython] Cs_element001  label="Cs_element : 1"  # scripted group (container) (typed FeaturePython)
  n = 1
  ref = Cs_element
FEATURE [App::DocumentObjectGroupPython] F_element006  label="F_element : 1"  # scripted group (container) (typed FeaturePython)
  n = 1
  ref = F_element
FEATURE [App::DocumentObjectGroupPython] G4_CESIUM_FLUORIDE  # scripted group (container) (typed FeaturePython)
  Dunit = g/cm3
  Dvalue = 4.115
  Group = -> [Cs_element001,F_element006]
  conduct = 2
  density = 1
  expand = 3
  formula = G4_CESIUM_FLUORIDE
  name = G4_CESIUM_FLUORIDE
  specific = 4
FEATURE [App::DocumentObjectGroupPython] Cs_element002  label="Cs_element : 002"  # scripted group (container) (typed FeaturePython)
  n = 1
  ref = Cs_element
FEATURE [App::DocumentObjectGroupPython] I_element001  label="I_element : 1"  # scripted group (container) (typed FeaturePython)
  n = 1
  ref = I_element
FEATURE [App::DocumentObjectGroupPython] G4_CESIUM_IODIDE  # scripted group (container) (typed FeaturePython)
  Dunit = g/cm3
  Dvalue = 4.51
  Group = -> [Cs_element002,I_element001]
  conduct = 2
  density = 1
  expand = 3
  formula = G4_CESIUM_IODIDE
  name = G4_CESIUM_IODIDE
  specific = 4
FEATURE [App::DocumentObjectGroupPython] C_element028  label="C_element : 013"  # scripted group (container) (typed FeaturePython)
  n = 6
  ref = C_element
FEATURE [App::DocumentObjectGroupPython] H_element025  label="H_element : 013"  # scripted group (container) (typed FeaturePython)
  n = 5
  ref = H_element
FEATURE [App::DocumentObjectGroupPython] Cl_element005  label="Cl_element : 1"  # scripted group (container) (typed FeaturePython)
  n = 1
  ref = Cl_element
FEATURE [App::DocumentObjectGroupPython] G4_CHLOROBENZENE  # scripted group (container) (typed FeaturePython)
  Dunit = g/cm3
  Dvalue = 1.1058
  Group = -> [C_element028,H_element025,Cl_element005]
  conduct = 2
  density = 1
  expand = 3
  formula = G4_CHLOROBENZENE
  name = G4_CHLOROBENZENE
  specific = 4
FEATURE [App::DocumentObjectGroupPython] C_element029  label="C_element : 014"  # scripted group (container) (typed FeaturePython)
  n = 1
  ref = C_element
FEATURE [App::DocumentObjectGroupPython] H_element026  label="H_element : 1"  # scripted group (container) (typed FeaturePython)
  n = 1
  ref = H_element
FEATURE [App::DocumentObjectGroupPython] Cl_element006  label="Cl_element : 3"  # scripted group (container) (typed FeaturePython)
  n = 3
  ref = Cl_element
FEATURE [App::DocumentObjectGroupPython] G4_CHLOROFORM  # scripted group (container) (typed FeaturePython)
  Dunit = g/cm3
  Dvalue = 1.4832
  Group = -> [C_element029,H_element026,Cl_element006]
  conduct = 2
  density = 1
  expand = 3
  formula = G4_CHLOROFORM
  name = G4_CHLOROFORM
  specific = 4
FEATURE [App::DocumentObjectGroupPython] H_element027  label="H_element : 0.010"  # scripted group (container) (typed FeaturePython)
  n = 0.01
FEATURE [App::DocumentObjectGroupPython] C_element030  label="C_element : 0.001"  # scripted group (container) (typed FeaturePython)
  n = 0.001
FEATURE [App::DocumentObjectGroupPython] O_element030  label="O_element : 0.529"  # scripted group (container) (typed FeaturePython)
  n = 0.529107
FEATURE [App::DocumentObjectGroupPython] Na_element005  label="Na_element : 0.016"  # scripted group (container) (typed FeaturePython)
  n = 0.016
FEATURE [App::DocumentObjectGroupPython] Mg_element003  label="Mg_element : 0.004"  # scripted group (container) (typed FeaturePython)
  n = 0.002
FEATURE [App::DocumentObjectGroupPython] Al_element002  label="Al_element : 0.034"  # scripted group (container) (typed FeaturePython)
  n = 0.033872
FEATURE [App::DocumentObjectGroupPython] Si_element002  label="Si_element : 0.337"  # scripted group (container) (typed FeaturePython)
  n = 0.337021
FEATURE [App::DocumentObjectGroupPython] K_element003  label="K_element : 0.013"  # scripted group (container) (typed FeaturePython)
  n = 0.013
FEATURE [App::DocumentObjectGroupPython] Ca_element010  label="Ca_element : 0.044"  # scripted group (container) (typed FeaturePython)
  n = 0.044
FEATURE [App::DocumentObjectGroupPython] Fe_element002  label="Fe_element : 0.014"  # scripted group (container) (typed FeaturePython)
  n = 0.014
FEATURE [App::DocumentObjectGroupPython] G4_CONCRETE  # scripted group (container) (typed FeaturePython)
  Dunit = g/cm3
  Dvalue = 2.3
  Group = -> [H_element027,C_element030,O_element030,Na_element005,Mg_element003,Al_element002,Si_element002,K_element003,Ca_element010,Fe_element002]
  conduct = 2
  density = 1
  expand = 3
  formula = G4_CONCRETE
  name = G4_CONCRETE
  specific = 4
FEATURE [App::DocumentObjectGroupPython] C_element031  label="C_element : 015"  # scripted group (container) (typed FeaturePython)
  n = 6
  ref = C_element
FEATURE [App::DocumentObjectGroupPython] H_element028  label="H_element : 12"  # scripted group (container) (typed FeaturePython)
  n = 12
  ref = H_element
FEATURE [App::DocumentObjectGroupPython] G4_CYCLOHEXANE  # scripted group (container) (typed FeaturePython)
  Dunit = g/cm3
  Dvalue = 0.779
  Group = -> [C_element031,H_element028]
  conduct = 2
  density = 1
  expand = 3
  formula = G4_CYCLOHEXANE
  name = G4_CYCLOHEXANE
  specific = 4
FEATURE [App::DocumentObjectGroupPython] C_element032  label="C_element : 016"  # scripted group (container) (typed FeaturePython)
  n = 6
  ref = C_element
FEATURE [App::DocumentObjectGroupPython] H_element029  label="H_element : 4"  # scripted group (container) (typed FeaturePython)
  n = 4
  ref = H_element
FEATURE [App::DocumentObjectGroupPython] Cl_element007  label="Cl_element : 2"  # scripted group (container) (typed FeaturePython)
  n = 2
  ref = Cl_element
FEATURE [App::DocumentObjectGroupPython] G4_1_2_DICHLOROBENZENE  label="G4_1.2-DICHLOROBENZENE"  # scripted group (container) (typed FeaturePython)
  Dunit = g/cm3
  Dvalue = 1.3048
  Group = -> [C_element032,H_element029,Cl_element007]
  conduct = 2
  density = 1
  expand = 3
  formula = G4_1.2-DICHLOROBENZENE
  name = G4_1.2-DICHLOROBENZENE
  specific = 4
FEATURE [App::DocumentObjectGroupPython] C_element033  label="C_element : 017"  # scripted group (container) (typed FeaturePython)
  n = 4
  ref = C_element
FEATURE [App::DocumentObjectGroupPython] H_element030  label="H_element : 8"  # scripted group (container) (typed FeaturePython)
  n = 8
  ref = H_element
FEATURE [App::DocumentObjectGroupPython] O_element031  label="O_element : 014"  # scripted group (container) (typed FeaturePython)
  n = 1
  ref = O_element
FEATURE [App::DocumentObjectGroupPython] Cl_element008  label="Cl_element : 005"  # scripted group (container) (typed FeaturePython)
  n = 2
  ref = Cl_element
FEATURE [App::DocumentObjectGroupPython] G4_DICHLORODIETHYL_ETHER  # scripted group (container) (typed FeaturePython)
  Dunit = g/cm3
  Dvalue = 1.2199
  Group = -> [C_element033,H_element030,O_element031,Cl_element008]
  conduct = 2
  density = 1
  expand = 3
  formula = G4_DICHLORODIETHYL_ETHER
  name = G4_DICHLORODIETHYL_ETHER
  specific = 4
FEATURE [App::DocumentObjectGroupPython] C_element034  label="C_element : 018"  # scripted group (container) (typed FeaturePython)
  n = 2
  ref = C_element
FEATURE [App::DocumentObjectGroupPython] H_element031  label="H_element : 014"  # scripted group (container) (typed FeaturePython)
  n = 4
  ref = H_element
FEATURE [App::DocumentObjectGroupPython] Cl_element009  label="Cl_element : 006"  # scripted group (container) (typed FeaturePython)
  n = 2
  ref = Cl_element
FEATURE [App::DocumentObjectGroupPython] G4_1_2_DICHLOROETHANE  label="G4_1.2-DICHLOROETHANE"  # scripted group (container) (typed FeaturePython)
  Dunit = g/cm3
  Dvalue = 1.2351
  Group = -> [C_element034,H_element031,Cl_element009]
  conduct = 2
  density = 1
  expand = 3
  formula = G4_1.2-DICHLOROETHANE
  name = G4_1.2-DICHLOROETHANE
  specific = 4
FEATURE [App::DocumentObjectGroupPython] C_element035  label="C_element : 019"  # scripted group (container) (typed FeaturePython)
  n = 4
  ref = C_element
FEATURE [App::DocumentObjectGroupPython] H_element032  label="H_element : 015"  # scripted group (container) (typed FeaturePython)
  n = 10
  ref = H_element
FEATURE [App::DocumentObjectGroupPython] O_element032  label="O_element : 015"  # scripted group (container) (typed FeaturePython)
  n = 1
  ref = O_element
FEATURE [App::DocumentObjectGroupPython] G4_DIETHYL_ETHER  # scripted group (container) (typed FeaturePython)
  Dunit = g/cm3
  Dvalue = 0.71378
  Group = -> [C_element035,H_element032,O_element032]
  conduct = 2
  density = 1
  expand = 3
  formula = G4_DIETHYL_ETHER
  name = G4_DIETHYL_ETHER
  specific = 4
FEATURE [App::DocumentObjectGroupPython] C_element036  label="C_element : 020"  # scripted group (container) (typed FeaturePython)
  n = 3
  ref = C_element
FEATURE [App::DocumentObjectGroupPython] H_element033  label="H_element : 016"  # scripted group (container) (typed FeaturePython)
  n = 7
  ref = H_element
FEATURE [App::DocumentObjectGroupPython] N_element015  label="N_element : 008"  # scripted group (container) (typed FeaturePython)
  n = 1
  ref = N_element
FEATURE [App::DocumentObjectGroupPython] O_element033  label="O_element : 016"  # scripted group (container) (typed FeaturePython)
  n = 1
  ref = O_element
FEATURE [App::DocumentObjectGroupPython] G4_N_N_DIMETHYL_FORMAMIDE  label="G4_N.N-DIMETHYL_FORMAMIDE"  # scripted group (container) (typed FeaturePython)
  Dunit = g/cm3
  Dvalue = 0.9487
  Group = -> [C_element036,H_element033,N_element015,O_element033]
  conduct = 2
  density = 1
  expand = 3
  formula = G4_N.N-DIMETHYL_FORMAMIDE
  name = G4_N.N-DIMETHYL_FORMAMIDE
  specific = 4
FEATURE [App::DocumentObjectGroupPython] C_element037  label="C_element : 021"  # scripted group (container) (typed FeaturePython)
  n = 2
  ref = C_element
FEATURE [App::DocumentObjectGroupPython] H_element034  label="H_element : 017"  # scripted group (container) (typed FeaturePython)
  n = 6
  ref = H_element
FEATURE [App::DocumentObjectGroupPython] O_element034  label="O_element : 017"  # scripted group (container) (typed FeaturePython)
  n = 1
  ref = O_element
FEATURE [App::DocumentObjectGroupPython] S_element009  label="S_element : 003"  # scripted group (container) (typed FeaturePython)
  n = 1
  ref = S_element
FEATURE [App::DocumentObjectGroupPython] G4_DIMETHYL_SULFOXIDE  # scripted group (container) (typed FeaturePython)
  Dunit = g/cm3
  Dvalue = 1.1014
  Group = -> [C_element037,H_element034,O_element034,S_element009]
  conduct = 2
  density = 1
  expand = 3
  formula = G4_DIMETHYL_SULFOXIDE
  name = G4_DIMETHYL_SULFOXIDE
  specific = 4
FEATURE [App::DocumentObjectGroupPython] C_element038  label="C_element : 022"  # scripted group (container) (typed FeaturePython)
  n = 2
  ref = C_element
FEATURE [App::DocumentObjectGroupPython] H_element035  label="H_element : 018"  # scripted group (container) (typed FeaturePython)
  n = 6
  ref = H_element
FEATURE [App::DocumentObjectGroupPython] G4_ETHANE  # scripted group (container) (typed FeaturePython)
  Dunit = g/cm3
  Dvalue = 0.00125324
  Group = -> [C_element038,H_element035]
  conduct = 2
  density = 1
  expand = 3
  formula = G4_ETHANE
  name = G4_ETHANE
  specific = 4
FEATURE [App::DocumentObjectGroupPython] C_element039  label="C_element : 023"  # scripted group (container) (typed FeaturePython)
  n = 2
  ref = C_element
FEATURE [App::DocumentObjectGroupPython] H_element036  label="H_element : 019"  # scripted group (container) (typed FeaturePython)
  n = 6
  ref = H_element
FEATURE [App::DocumentObjectGroupPython] O_element035  label="O_element : 018"  # scripted group (container) (typed FeaturePython)
  n = 1
  ref = O_element
FEATURE [App::DocumentObjectGroupPython] G4_ETHYL_ALCOHOL  # scripted group (container) (typed FeaturePython)
  Dunit = g/cm3
  Dvalue = 0.7893
  Group = -> [C_element039,H_element036,O_element035]
  conduct = 2
  density = 1
  expand = 3
  formula = G4_ETHYL_ALCOHOL
  name = G4_ETHYL_ALCOHOL
  specific = 4
FEATURE [App::DocumentObjectGroupPython] H_element037  label="H_element : 0.090"  # scripted group (container) (typed FeaturePython)
  n = 0.090027
FEATURE [App::DocumentObjectGroupPython] C_element040  label="C_element : 0.585"  # scripted group (container) (typed FeaturePython)
  n = 0.585182
FEATURE [App::DocumentObjectGroupPython] O_element036  label="O_element : 0.325"  # scripted group (container) (typed FeaturePython)
  n = 0.324791
FEATURE [App::DocumentObjectGroupPython] G4_ETHYL_CELLULOSE  # scripted group (container) (typed FeaturePython)
  Dunit = g/cm3
  Dvalue = 1.13
  Group = -> [H_element037,C_element040,O_element036]
  conduct = 2
  density = 1
  expand = 3
  formula = G4_ETHYL_CELLULOSE
  name = G4_ETHYL_CELLULOSE
  specific = 4
FEATURE [App::DocumentObjectGroupPython] C_element041  label="C_element : 024"  # scripted group (container) (typed FeaturePython)
  n = 2
  ref = C_element
FEATURE [App::DocumentObjectGroupPython] H_element038  label="H_element : 020"  # scripted group (container) (typed FeaturePython)
  n = 4
  ref = H_element
FEATURE [App::DocumentObjectGroupPython] G4_ETHYLENE  # scripted group (container) (typed FeaturePython)
  Dunit = g/cm3
  Dvalue = 0.00117497
  Group = -> [C_element041,H_element038]
  conduct = 2
  density = 1
  expand = 3
  formula = G4_ETHYLENE
  name = G4_ETHYLENE
  specific = 4
FEATURE [App::DocumentObjectGroupPython] H_element039  label="H_element : 0.096"  # scripted group (container) (typed FeaturePython)
  n = 0.096
FEATURE [App::DocumentObjectGroupPython] C_element042  label="C_element : 0.195"  # scripted group (container) (typed FeaturePython)
  n = 0.195
FEATURE [App::DocumentObjectGroupPython] N_element016  label="N_element : 0.057"  # scripted group (container) (typed FeaturePython)
  n = 0.057
FEATURE [App::DocumentObjectGroupPython] O_element037  label="O_element : 0.646"  # scripted group (container) (typed FeaturePython)
  n = 0.646
FEATURE [App::DocumentObjectGroupPython] Na_element006  label="Na_element : 0.017"  # scripted group (container) (typed FeaturePython)
  n = 0.001
FEATURE [App::DocumentObjectGroupPython] P_element005  label="P_element : 0.104"  # scripted group (container) (typed FeaturePython)
  n = 0.001
FEATURE [App::DocumentObjectGroupPython] S_element010  label="S_element : 0.016"  # scripted group (container) (typed FeaturePython)
  n = 0.003
FEATURE [App::DocumentObjectGroupPython] Cl_element010  label="Cl_element : 0.005"  # scripted group (container) (typed FeaturePython)
  n = 0.001
FEATURE [App::DocumentObjectGroupPython] G4_EYE_LENS_ICRP  # scripted group (container) (typed FeaturePython)
  Dunit = g/cm3
  Dvalue = 1.07
  Group = -> [H_element039,C_element042,N_element016,O_element037,Na_element006,P_element005,S_element010,Cl_element010]
  conduct = 2
  density = 1
  expand = 3
  formula = G4_EYE_LENS_ICRP
  name = G4_EYE_LENS_ICRP
  specific = 4
FEATURE [App::DocumentObjectGroupPython] Fe_element003  label="Fe_element : 2"  # scripted group (container) (typed FeaturePython)
  n = 2
  ref = Fe_element
FEATURE [App::DocumentObjectGroupPython] O_element038  label="O_element : 019"  # scripted group (container) (typed FeaturePython)
  n = 3
  ref = O_element
FEATURE [App::DocumentObjectGroupPython] G4_FERRIC_OXIDE  # scripted group (container) (typed FeaturePython)
  Dunit = g/cm3
  Dvalue = 5.2
  Group = -> [Fe_element003,O_element038]
  conduct = 2
  density = 1
  expand = 3
  formula = G4_FERRIC_OXIDE
  name = G4_FERRIC_OXIDE
  specific = 4
FEATURE [App::DocumentObjectGroupPython] Fe_element004  label="Fe_element : 1"  # scripted group (container) (typed FeaturePython)
  n = 1
  ref = Fe_element
FEATURE [App::DocumentObjectGroupPython] B_element003  label="B_element : 1"  # scripted group (container) (typed FeaturePython)
  n = 1
  ref = B_element
FEATURE [App::DocumentObjectGroupPython] G4_FERROBORIDE  # scripted group (container) (typed FeaturePython)
  Dunit = g/cm3
  Dvalue = 7.15
  Group = -> [Fe_element004,B_element003]
  conduct = 2
  density = 1
  expand = 3
  formula = G4_FERROBORIDE
  name = G4_FERROBORIDE
  specific = 4
FEATURE [App::DocumentObjectGroupPython] Fe_element005  label="Fe_element : 003"  # scripted group (container) (typed FeaturePython)
  n = 1
  ref = Fe_element
FEATURE [App::DocumentObjectGroupPython] O_element039  label="O_element : 020"  # scripted group (container) (typed FeaturePython)
  n = 1
  ref = O_element
FEATURE [App::DocumentObjectGroupPython] G4_FERROUS_OXIDE  # scripted group (container) (typed FeaturePython)
  Dunit = g/cm3
  Dvalue = 5.7
  Group = -> [Fe_element005,O_element039]
  conduct = 2
  density = 1
  expand = 3
  formula = G4_FERROUS_OXIDE
  name = G4_FERROUS_OXIDE
  specific = 4
FEATURE [App::DocumentObjectGroupPython] H_element040  label="H_element : 0.115"  # scripted group (container) (typed FeaturePython)
  n = 0.108259
FEATURE [App::DocumentObjectGroupPython] N_element017  label="N_element : 0.000"  # scripted group (container) (typed FeaturePython)
  n = 2.7e-05
FEATURE [App::DocumentObjectGroupPython] O_element040  label="O_element : 0.879"  # scripted group (container) (typed FeaturePython)
  n = 0.878636
FEATURE [App::DocumentObjectGroupPython] Na_element007  label="Na_element : 0.000"  # scripted group (container) (typed FeaturePython)
  n = 2.2e-05
FEATURE [App::DocumentObjectGroupPython] S_element011  label="S_element : 0.013"  # scripted group (container) (typed FeaturePython)
  n = 0.012968
FEATURE [App::DocumentObjectGroupPython] Cl_element011  label="Cl_element : 0.000"  # scripted group (container) (typed FeaturePython)
  n = 3.4e-05
FEATURE [App::DocumentObjectGroupPython] Fe_element006  label="Fe_element : 0.000"  # scripted group (container) (typed FeaturePython)
  n = 5.4e-05
FEATURE [App::DocumentObjectGroupPython] G4_FERROUS_SULFATE  # scripted group (container) (typed FeaturePython)
  Dunit = g/cm3
  Dvalue = 1.024
  Group = -> [H_element040,N_element017,O_element040,Na_element007,S_element011,Cl_element011,Fe_element006]
  conduct = 2
  density = 1
  expand = 3
  formula = G4_FERROUS_SULFATE
  name = G4_FERROUS_SULFATE
  specific = 4
FEATURE [App::DocumentObjectGroupPython] C_element043  label="C_element : 0.099"  # scripted group (container) (typed FeaturePython)
  n = 0.099335
FEATURE [App::DocumentObjectGroupPython] F_element007  label="F_element : 0.314"  # scripted group (container) (typed FeaturePython)
  n = 0.314247
FEATURE [App::DocumentObjectGroupPython] Cl_element012  label="Cl_element : 0.586"  # scripted group (container) (typed FeaturePython)
  n = 0.586418
FEATURE [App::DocumentObjectGroupPython] G4_FREON_12  label="G4_FREON-12"  # scripted group (container) (typed FeaturePython)
  Dunit = g/cm3
  Dvalue = 1.12
  Group = -> [C_element043,F_element007,Cl_element012]
  conduct = 2
  density = 1
  expand = 3
  formula = G4_FREON-12
  name = G4_FREON-12
  specific = 4
FEATURE [App::DocumentObjectGroupPython] C_element044  label="C_element : 0.057"  # scripted group (container) (typed FeaturePython)
  n = 0.057245
FEATURE [App::DocumentObjectGroupPython] F_element008  label="F_element : 0.181"  # scripted group (container) (typed FeaturePython)
  n = 0.181096
FEATURE [App::DocumentObjectGroupPython] Br_element001  label="Br_element : 0.762"  # scripted group (container) (typed FeaturePython)
  n = 0.761659
FEATURE [App::DocumentObjectGroupPython] G4_FREON_12B2  label="G4_FREON-12B2"  # scripted group (container) (typed FeaturePython)
  Dunit = g/cm3
  Dvalue = 1.8
  Group = -> [C_element044,F_element008,Br_element001]
  conduct = 2
  density = 1
  expand = 3
  formula = G4_FREON-12B2
  name = G4_FREON-12B2
  specific = 4
FEATURE [App::DocumentObjectGroupPython] C_element045  label="C_element : 0.115"  # scripted group (container) (typed FeaturePython)
  n = 0.114983
FEATURE [App::DocumentObjectGroupPython] F_element009  label="F_element : 0.546"  # scripted group (container) (typed FeaturePython)
  n = 0.545621
FEATURE [App::DocumentObjectGroupPython] Cl_element013  label="Cl_element : 0.339"  # scripted group (container) (typed FeaturePython)
  n = 0.339396
FEATURE [App::DocumentObjectGroupPython] G4_FREON_13  label="G4_FREON-13"  # scripted group (container) (typed FeaturePython)
  Dunit = g/cm3
  Dvalue = 0.95
  Group = -> [C_element045,F_element009,Cl_element013]
  conduct = 2
  density = 1
  expand = 3
  formula = G4_FREON-13
  name = G4_FREON-13
  specific = 4
FEATURE [App::DocumentObjectGroupPython] C_element046  label="C_element : 025"  # scripted group (container) (typed FeaturePython)
  n = 1
  ref = C_element
FEATURE [App::DocumentObjectGroupPython] F_element010  label="F_element : 3"  # scripted group (container) (typed FeaturePython)
  n = 3
  ref = F_element
FEATURE [App::DocumentObjectGroupPython] Br_element002  label="Br_element : 1"  # scripted group (container) (typed FeaturePython)
  n = 1
  ref = Br_element
FEATURE [App::DocumentObjectGroupPython] G4_FREON_13B1  label="G4_FREON-13B1"  # scripted group (container) (typed FeaturePython)
  Dunit = g/cm3
  Dvalue = 1.5
  Group = -> [C_element046,F_element010,Br_element002]
  conduct = 2
  density = 1
  expand = 3
  formula = G4_FREON-13B1
  name = G4_FREON-13B1
  specific = 4
FEATURE [App::DocumentObjectGroupPython] C_element047  label="C_element : 0.061"  # scripted group (container) (typed FeaturePython)
  n = 0.061309
FEATURE [App::DocumentObjectGroupPython] F_element011  label="F_element : 0.291"  # scripted group (container) (typed FeaturePython)
  n = 0.290924
FEATURE [App::DocumentObjectGroupPython] I_element002  label="I_element : 0.648"  # scripted group (container) (typed FeaturePython)
  n = 0.647767
FEATURE [App::DocumentObjectGroupPython] G4_FREON_13I1  label="G4_FREON-13I1"  # scripted group (container) (typed FeaturePython)
  Dunit = g/cm3
  Dvalue = 1.8
  Group = -> [C_element047,F_element011,I_element002]
  conduct = 2
  density = 1
  expand = 3
  formula = G4_FREON-13I1
  name = G4_FREON-13I1
  specific = 4
FEATURE [App::DocumentObjectGroupPython] Gd_element001  label="Gd_element : 2"  # scripted group (container) (typed FeaturePython)
  n = 2
  ref = Gd_element
FEATURE [App::DocumentObjectGroupPython] O_element041  label="O_element : 021"  # scripted group (container) (typed FeaturePython)
  n = 2
  ref = O_element
FEATURE [App::DocumentObjectGroupPython] S_element012  label="S_element : 004"  # scripted group (container) (typed FeaturePython)
  n = 1
  ref = S_element
FEATURE [App::DocumentObjectGroupPython] G4_GADOLINIUM_OXYSULFIDE  # scripted group (container) (typed FeaturePython)
  Dunit = g/cm3
  Dvalue = 7.44
  Group = -> [Gd_element001,O_element041,S_element012]
  conduct = 2
  density = 1
  expand = 3
  formula = G4_GADOLINIUM_OXYSULFIDE
  name = G4_GADOLINIUM_OXYSULFIDE
  specific = 4
FEATURE [App::DocumentObjectGroupPython] Ga_element001  label="Ga_element : 1"  # scripted group (container) (typed FeaturePython)
  n = 1
  ref = Ga_element
FEATURE [App::DocumentObjectGroupPython] As_element001  label="As_element : 1"  # scripted group (container) (typed FeaturePython)
  n = 1
  ref = As_element
FEATURE [App::DocumentObjectGroupPython] G4_GALLIUM_ARSENIDE  # scripted group (container) (typed FeaturePython)
  Dunit = g/cm3
  Dvalue = 5.31
  Group = -> [Ga_element001,As_element001]
  conduct = 2
  density = 1
  expand = 3
  formula = G4_GALLIUM_ARSENIDE
  name = G4_GALLIUM_ARSENIDE
  specific = 4
FEATURE [App::DocumentObjectGroupPython] H_element041  label="H_element : 0.081"  # scripted group (container) (typed FeaturePython)
  n = 0.08118
FEATURE [App::DocumentObjectGroupPython] C_element048  label="C_element : 0.416"  # scripted group (container) (typed FeaturePython)
  n = 0.41606
FEATURE [App::DocumentObjectGroupPython] N_element018  label="N_element : 0.111"  # scripted group (container) (typed FeaturePython)
  n = 0.11124
FEATURE [App::DocumentObjectGroupPython] O_element042  label="O_element : 0.381"  # scripted group (container) (typed FeaturePython)
  n = 0.38064
FEATURE [App::DocumentObjectGroupPython] S_element013  label="S_element : 0.011"  # scripted group (container) (typed FeaturePython)
  n = 0.01088
FEATURE [App::DocumentObjectGroupPython] G4_GEL_PHOTO_EMULSION  # scripted group (container) (typed FeaturePython)
  Dunit = g/cm3
  Dvalue = 1.2914
  Group = -> [H_element041,C_element048,N_element018,O_element042,S_element013]
  conduct = 2
  density = 1
  expand = 3
  formula = G4_GEL_PHOTO_EMULSION
  name = G4_GEL_PHOTO_EMULSION
  specific = 4
FEATURE [App::DocumentObjectGroupPython] B_element004  label="B_element : 0.040"  # scripted group (container) (typed FeaturePython)
  n = 0.0400639
FEATURE [App::DocumentObjectGroupPython] O_element043  label="O_element : 0.540"  # scripted group (container) (typed FeaturePython)
  n = 0.539561
FEATURE [App::DocumentObjectGroupPython] Na_element008  label="Na_element : 0.028"  # scripted group (container) (typed FeaturePython)
  n = 0.0281909
FEATURE [App::DocumentObjectGroupPython] Al_element003  label="Al_element : 0.012"  # scripted group (container) (typed FeaturePython)
  n = 0.011644
FEATURE [App::DocumentObjectGroupPython] Si_element003  label="Si_element : 0.377"  # scripted group (container) (typed FeaturePython)
  n = 0.377219
FEATURE [App::DocumentObjectGroupPython] K_element004  label="K_element : 0.014"  # scripted group (container) (typed FeaturePython)
  n = 0.00332099
FEATURE [App::DocumentObjectGroupPython] G4_Pyrex_Glass  # scripted group (container) (typed FeaturePython)
  Dunit = g/cm3
  Dvalue = 2.23
  Group = -> [B_element004,O_element043,Na_element008,Al_element003,Si_element003,K_element004]
  conduct = 2
  density = 1
  expand = 3
  formula = G4_Pyrex_Glass
  name = G4_Pyrex_Glass
  specific = 4
FEATURE [App::DocumentObjectGroupPython] O_element044  label="O_element : 0.156"  # scripted group (container) (typed FeaturePython)
  n = 0.156453
FEATURE [App::DocumentObjectGroupPython] Si_element004  label="Si_element : 0.081"  # scripted group (container) (typed FeaturePython)
  n = 0.080866
FEATURE [App::DocumentObjectGroupPython] Ti_element001  label="Ti_element : 0.008"  # scripted group (container) (typed FeaturePython)
  n = 0.008092
FEATURE [App::DocumentObjectGroupPython] As_element002  label="As_element : 0.003"  # scripted group (container) (typed FeaturePython)
  n = 0.002651
FEATURE [App::DocumentObjectGroupPython] Pb_element001  label="Pb_element : 0.752"  # scripted group (container) (typed FeaturePython)
  n = 0.751938
FEATURE [App::DocumentObjectGroupPython] G4_GLASS_LEAD  # scripted group (container) (typed FeaturePython)
  Dunit = g/cm3
  Dvalue = 6.22
  Group = -> [O_element044,Si_element004,Ti_element001,As_element002,Pb_element001]
  conduct = 2
  density = 1
  expand = 3
  formula = G4_GLASS_LEAD
  name = G4_GLASS_LEAD
  specific = 4
FEATURE [App::DocumentObjectGroupPython] O_element045  label="O_element : 0.460"  # scripted group (container) (typed FeaturePython)
  n = 0.4598
FEATURE [App::DocumentObjectGroupPython] Na_element009  label="Na_element : 0.096"  # scripted group (container) (typed FeaturePython)
  n = 0.0964411
FEATURE [App::DocumentObjectGroupPython] Si_element005  label="Si_element : 0.378"  # scripted group (container) (typed FeaturePython)
  n = 0.336553
FEATURE [App::DocumentObjectGroupPython] Ca_element011  label="Ca_element : 0.107"  # scripted group (container) (typed FeaturePython)
  n = 0.107205
FEATURE [App::DocumentObjectGroupPython] G4_GLASS_PLATE  # scripted group (container) (typed FeaturePython)
  Dunit = g/cm3
  Dvalue = 2.4
  Group = -> [O_element045,Na_element009,Si_element005,Ca_element011]
  conduct = 2
  density = 1
  expand = 3
  formula = G4_GLASS_PLATE
  name = G4_GLASS_PLATE
  specific = 4
FEATURE [App::DocumentObjectGroupPython] C_element049  label="C_element : 026"  # scripted group (container) (typed FeaturePython)
  n = 5
  ref = C_element
FEATURE [App::DocumentObjectGroupPython] H_element042  label="H_element : 021"  # scripted group (container) (typed FeaturePython)
  n = 10
  ref = H_element
FEATURE [App::DocumentObjectGroupPython] N_element019  label="N_element : 2"  # scripted group (container) (typed FeaturePython)
  n = 2
  ref = N_element
FEATURE [App::DocumentObjectGroupPython] O_element046  label="O_element : 022"  # scripted group (container) (typed FeaturePython)
  n = 3
  ref = O_element
FEATURE [App::DocumentObjectGroupPython] G4_GLUTAMINE  # scripted group (container) (typed FeaturePython)
  Dunit = g/cm3
  Dvalue = 1.46
  Group = -> [C_element049,H_element042,N_element019,O_element046]
  conduct = 2
  density = 1
  expand = 3
  formula = G4_GLUTAMINE
  name = G4_GLUTAMINE
  specific = 4
FEATURE [App::DocumentObjectGroupPython] C_element050  label="C_element : 027"  # scripted group (container) (typed FeaturePython)
  n = 3
  ref = C_element
FEATURE [App::DocumentObjectGroupPython] H_element043  label="H_element : 022"  # scripted group (container) (typed FeaturePython)
  n = 8
  ref = H_element
FEATURE [App::DocumentObjectGroupPython] O_element047  label="O_element : 023"  # scripted group (container) (typed FeaturePython)
  n = 3
  ref = O_element
FEATURE [App::DocumentObjectGroupPython] G4_GLYCEROL  # scripted group (container) (typed FeaturePython)
  Dunit = g/cm3
  Dvalue = 1.2613
  Group = -> [C_element050,H_element043,O_element047]
  conduct = 2
  density = 1
  expand = 3
  formula = G4_GLYCEROL
  name = G4_GLYCEROL
  specific = 4
FEATURE [App::DocumentObjectGroupPython] C_element051  label="C_element : 028"  # scripted group (container) (typed FeaturePython)
  n = 5
  ref = C_element
FEATURE [App::DocumentObjectGroupPython] H_element044  label="H_element : 023"  # scripted group (container) (typed FeaturePython)
  n = 5
  ref = H_element
FEATURE [App::DocumentObjectGroupPython] N_element020  label="N_element : 009"  # scripted group (container) (typed FeaturePython)
  n = 5
  ref = N_element
FEATURE [App::DocumentObjectGroupPython] O_element048  label="O_element : 024"  # scripted group (container) (typed FeaturePython)
  n = 1
  ref = O_element
FEATURE [App::DocumentObjectGroupPython] G4_GUANINE  # scripted group (container) (typed FeaturePython)
  Dunit = g/cm3
  Dvalue = 2.2
  Group = -> [C_element051,H_element044,N_element020,O_element048]
  conduct = 2
  density = 1
  expand = 3
  formula = G4_GUANINE
  name = G4_GUANINE
  specific = 4
FEATURE [App::DocumentObjectGroupPython] Ca_element012  label="Ca_element : 006"  # scripted group (container) (typed FeaturePython)
  n = 1
  ref = Ca_element
FEATURE [App::DocumentObjectGroupPython] S_element014  label="S_element : 005"  # scripted group (container) (typed FeaturePython)
  n = 1
  ref = S_element
FEATURE [App::DocumentObjectGroupPython] O_element049  label="O_element : 6"  # scripted group (container) (typed FeaturePython)
  n = 6
  ref = O_element
FEATURE [App::DocumentObjectGroupPython] H_element045  label="H_element : 024"  # scripted group (container) (typed FeaturePython)
  n = 4
  ref = H_element
FEATURE [App::DocumentObjectGroupPython] G4_GYPSUM  # scripted group (container) (typed FeaturePython)
  Dunit = g/cm3
  Dvalue = 2.32
  Group = -> [Ca_element012,S_element014,O_element049,H_element045]
  conduct = 2
  density = 1
  expand = 3
  formula = G4_GYPSUM
  name = G4_GYPSUM
  specific = 4
FEATURE [App::DocumentObjectGroupPython] C_element052  label="C_element : 7"  # scripted group (container) (typed FeaturePython)
  n = 7
  ref = C_element
FEATURE [App::DocumentObjectGroupPython] H_element046  label="H_element : 16"  # scripted group (container) (typed FeaturePython)
  n = 16
  ref = H_element
FEATURE [App::DocumentObjectGroupPython] G4_N_HEPTANE  label="G4_N-HEPTANE"  # scripted group (container) (typed FeaturePython)
  Dunit = g/cm3
  Dvalue = 0.68376
  Group = -> [C_element052,H_element046]
  conduct = 2
  density = 1
  expand = 3
  formula = G4_N-HEPTANE
  name = G4_N-HEPTANE
  specific = 4
FEATURE [App::DocumentObjectGroupPython] C_element053  label="C_element : 029"  # scripted group (container) (typed FeaturePython)
  n = 6
  ref = C_element
FEATURE [App::DocumentObjectGroupPython] H_element047  label="H_element : 14"  # scripted group (container) (typed FeaturePython)
  n = 14
  ref = H_element
FEATURE [App::DocumentObjectGroupPython] G4_N_HEXANE  label="G4_N-HEXANE"  # scripted group (container) (typed FeaturePython)
  Dunit = g/cm3
  Dvalue = 0.6603
  Group = -> [C_element053,H_element047]
  conduct = 2
  density = 1
  expand = 3
  formula = G4_N-HEXANE
  name = G4_N-HEXANE
  specific = 4
FEATURE [App::DocumentObjectGroupPython] C_element054  label="C_element : 22"  # scripted group (container) (typed FeaturePython)
  n = 22
  ref = C_element
FEATURE [App::DocumentObjectGroupPython] H_element048  label="H_element : 025"  # scripted group (container) (typed FeaturePython)
  n = 10
  ref = H_element
FEATURE [App::DocumentObjectGroupPython] N_element021  label="N_element : 010"  # scripted group (container) (typed FeaturePython)
  n = 2
  ref = N_element
FEATURE [App::DocumentObjectGroupPython] O_element050  label="O_element : 025"  # scripted group (container) (typed FeaturePython)
  n = 5
  ref = O_element
FEATURE [App::DocumentObjectGroupPython] G4_KAPTON  # scripted group (container) (typed FeaturePython)
  Dunit = g/cm3
  Dvalue = 1.42
  Group = -> [C_element054,H_element048,N_element021,O_element050]
  conduct = 2
  density = 1
  expand = 3
  formula = G4_KAPTON
  name = G4_KAPTON
  specific = 4
FEATURE [App::DocumentObjectGroupPython] La_element001  label="La_element : 1"  # scripted group (container) (typed FeaturePython)
  n = 1
  ref = La_element
FEATURE [App::DocumentObjectGroupPython] Br_element003  label="Br_element : 002"  # scripted group (container) (typed FeaturePython)
  n = 1
  ref = Br_element
FEATURE [App::DocumentObjectGroupPython] O_element051  label="O_element : 026"  # scripted group (container) (typed FeaturePython)
  n = 1
  ref = O_element
FEATURE [App::DocumentObjectGroupPython] G4_LANTHANUM_OXYBROMIDE  # scripted group (container) (typed FeaturePython)
  Dunit = g/cm3
  Dvalue = 6.28
  Group = -> [La_element001,Br_element003,O_element051]
  conduct = 2
  density = 1
  expand = 3
  formula = G4_LANTHANUM_OXYBROMIDE
  name = G4_LANTHANUM_OXYBROMIDE
  specific = 4
FEATURE [App::DocumentObjectGroupPython] La_element002  label="La_element : 2"  # scripted group (container) (typed FeaturePython)
  n = 2
  ref = La_element
FEATURE [App::DocumentObjectGroupPython] O_element052  label="O_element : 027"  # scripted group (container) (typed FeaturePython)
  n = 2
  ref = O_element
FEATURE [App::DocumentObjectGroupPython] S_element015  label="S_element : 006"  # scripted group (container) (typed FeaturePython)
  n = 1
  ref = S_element
FEATURE [App::DocumentObjectGroupPython] G4_LANTHANUM_OXYSULFIDE  # scripted group (container) (typed FeaturePython)
  Dunit = g/cm3
  Dvalue = 5.86
  Group = -> [La_element002,O_element052,S_element015]
  conduct = 2
  density = 1
  expand = 3
  formula = G4_LANTHANUM_OXYSULFIDE
  name = G4_LANTHANUM_OXYSULFIDE
  specific = 4
FEATURE [App::DocumentObjectGroupPython] O_element053  label="O_element : 0.072"  # scripted group (container) (typed FeaturePython)
  n = 0.071682
FEATURE [App::DocumentObjectGroupPython] Pb_element002  label="Pb_element : 0.928"  # scripted group (container) (typed FeaturePython)
  n = 0.928318
FEATURE [App::DocumentObjectGroupPython] G4_LEAD_OXIDE  # scripted group (container) (typed FeaturePython)
  Dunit = g/cm3
  Dvalue = 9.53
  Group = -> [O_element053,Pb_element002]
  conduct = 2
  density = 1
  expand = 3
  formula = G4_LEAD_OXIDE
  name = G4_LEAD_OXIDE
  specific = 4
FEATURE [App::DocumentObjectGroupPython] Li_element001  label="Li_element : 1"  # scripted group (container) (typed FeaturePython)
  n = 1
  ref = Li_element
FEATURE [App::DocumentObjectGroupPython] N_element022  label="N_element : 011"  # scripted group (container) (typed FeaturePython)
  n = 1
  ref = N_element
FEATURE [App::DocumentObjectGroupPython] H_element049  label="H_element : 026"  # scripted group (container) (typed FeaturePython)
  n = 2
  ref = H_element
FEATURE [App::DocumentObjectGroupPython] G4_LITHIUM_AMIDE  # scripted group (container) (typed FeaturePython)
  Dunit = g/cm3
  Dvalue = 1.178
  Group = -> [Li_element001,N_element022,H_element049]
  conduct = 2
  density = 1
  expand = 3
  formula = G4_LITHIUM_AMIDE
  name = G4_LITHIUM_AMIDE
  specific = 4
FEATURE [App::DocumentObjectGroupPython] Li_element002  label="Li_element : 2"  # scripted group (container) (typed FeaturePython)
  n = 2
  ref = Li_element
FEATURE [App::DocumentObjectGroupPython] C_element055  label="C_element : 030"  # scripted group (container) (typed FeaturePython)
  n = 1
  ref = C_element
FEATURE [App::DocumentObjectGroupPython] O_element054  label="O_element : 028"  # scripted group (container) (typed FeaturePython)
  n = 3
  ref = O_element
FEATURE [App::DocumentObjectGroupPython] G4_LITHIUM_CARBONATE  # scripted group (container) (typed FeaturePython)
  Dunit = g/cm3
  Dvalue = 2.11
  Group = -> [Li_element002,C_element055,O_element054]
  conduct = 2
  density = 1
  expand = 3
  formula = G4_LITHIUM_CARBONATE
  name = G4_LITHIUM_CARBONATE
  specific = 4
FEATURE [App::DocumentObjectGroupPython] Li_element003  label="Li_element : 003"  # scripted group (container) (typed FeaturePython)
  n = 1
  ref = Li_element
FEATURE [App::DocumentObjectGroupPython] F_element012  label="F_element : 004"  # scripted group (container) (typed FeaturePython)
  n = 1
  ref = F_element
FEATURE [App::DocumentObjectGroupPython] G4_LITHIUM_FLUORIDE  # scripted group (container) (typed FeaturePython)
  Dunit = g/cm3
  Dvalue = 2.635
  Group = -> [Li_element003,F_element012]
  conduct = 2
  density = 1
  expand = 3
  formula = G4_LITHIUM_FLUORIDE
  name = G4_LITHIUM_FLUORIDE
  specific = 4
FEATURE [App::DocumentObjectGroupPython] Li_element004  label="Li_element : 004"  # scripted group (container) (typed FeaturePython)
  n = 1
  ref = Li_element
FEATURE [App::DocumentObjectGroupPython] H_element050  label="H_element : 027"  # scripted group (container) (typed FeaturePython)
  n = 1
  ref = H_element
FEATURE [App::DocumentObjectGroupPython] G4_LITHIUM_HYDRIDE  # scripted group (container) (typed FeaturePython)
  Dunit = g/cm3
  Dvalue = 0.82
  Group = -> [Li_element004,H_element050]
  conduct = 2
  density = 1
  expand = 3
  formula = G4_LITHIUM_HYDRIDE
  name = G4_LITHIUM_HYDRIDE
  specific = 4
FEATURE [App::DocumentObjectGroupPython] Li_element005  label="Li_element : 005"  # scripted group (container) (typed FeaturePython)
  n = 1
  ref = Li_element
FEATURE [App::DocumentObjectGroupPython] I_element003  label="I_element : 002"  # scripted group (container) (typed FeaturePython)
  n = 1
  ref = I_element
FEATURE [App::DocumentObjectGroupPython] G4_LITHIUM_IODIDE  # scripted group (container) (typed FeaturePython)
  Dunit = g/cm3
  Dvalue = 3.494
  Group = -> [Li_element005,I_element003]
  conduct = 2
  density = 1
  expand = 3
  formula = G4_LITHIUM_IODIDE
  name = G4_LITHIUM_IODIDE
  specific = 4
FEATURE [App::DocumentObjectGroupPython] Li_element006  label="Li_element : 006"  # scripted group (container) (typed FeaturePython)
  n = 2
  ref = Li_element
FEATURE [App::DocumentObjectGroupPython] O_element055  label="O_element : 029"  # scripted group (container) (typed FeaturePython)
  n = 1
  ref = O_element
FEATURE [App::DocumentObjectGroupPython] G4_LITHIUM_OXIDE  # scripted group (container) (typed FeaturePython)
  Dunit = g/cm3
  Dvalue = 2.013
  Group = -> [Li_element006,O_element055]
  conduct = 2
  density = 1
  expand = 3
  formula = G4_LITHIUM_OXIDE
  name = G4_LITHIUM_OXIDE
  specific = 4
FEATURE [App::DocumentObjectGroupPython] Li_element007  label="Li_element : 007"  # scripted group (container) (typed FeaturePython)
  n = 2
  ref = Li_element
FEATURE [App::DocumentObjectGroupPython] B_element005  label="B_element : 005"  # scripted group (container) (typed FeaturePython)
  n = 4
  ref = B_element
FEATURE [App::DocumentObjectGroupPython] O_element056  label="O_element : 7"  # scripted group (container) (typed FeaturePython)
  n = 7
  ref = O_element
FEATURE [App::DocumentObjectGroupPython] G4_LITHIUM_TETRABORATE  # scripted group (container) (typed FeaturePython)
  Dunit = g/cm3
  Dvalue = 2.44
  Group = -> [Li_element007,B_element005,O_element056]
  conduct = 2
  density = 1
  expand = 3
  formula = G4_LITHIUM_TETRABORATE
  name = G4_LITHIUM_TETRABORATE
  specific = 4
FEATURE [App::DocumentObjectGroupPython] H_element051  label="H_element : 0.105"  # scripted group (container) (typed FeaturePython)
  n = 0.105
FEATURE [App::DocumentObjectGroupPython] C_element056  label="C_element : 0.083"  # scripted group (container) (typed FeaturePython)
  n = 0.083
FEATURE [App::DocumentObjectGroupPython] N_element023  label="N_element : 0.023"  # scripted group (container) (typed FeaturePython)
  n = 0.023
FEATURE [App::DocumentObjectGroupPython] O_element057  label="O_element : 0.779"  # scripted group (container) (typed FeaturePython)
  n = 0.779
FEATURE [App::DocumentObjectGroupPython] Na_element010  label="Na_element : 0.097"  # scripted group (container) (typed FeaturePython)
  n = 0.002
FEATURE [App::DocumentObjectGroupPython] P_element006  label="P_element : 0.105"  # scripted group (container) (typed FeaturePython)
  n = 0.001
FEATURE [App::DocumentObjectGroupPython] S_element016  label="S_element : 0.017"  # scripted group (container) (typed FeaturePython)
  n = 0.002
FEATURE [App::DocumentObjectGroupPython] Cl_element014  label="Cl_element : 0.587"  # scripted group (container) (typed FeaturePython)
  n = 0.003
FEATURE [App::DocumentObjectGroupPython] K_element005  label="K_element : 0.015"  # scripted group (container) (typed FeaturePython)
  n = 0.002
FEATURE [App::DocumentObjectGroupPython] G4_LUNG_ICRP  # scripted group (container) (typed FeaturePython)
  Dunit = g/cm3
  Dvalue = 1.04
  Group = -> [H_element051,C_element056,N_element023,O_element057,Na_element010,P_element006,S_element016,Cl_element014,K_element005]
  conduct = 2
  density = 1
  expand = 3
  formula = G4_LUNG_ICRP
  name = G4_LUNG_ICRP
  specific = 4
FEATURE [App::DocumentObjectGroupPython] H_element052  label="H_element : 0.116"  # scripted group (container) (typed FeaturePython)
  n = 0.114318
FEATURE [App::DocumentObjectGroupPython] C_element057  label="C_element : 0.656"  # scripted group (container) (typed FeaturePython)
  n = 0.655824
FEATURE [App::DocumentObjectGroupPython] O_element058  label="O_element : 0.092"  # scripted group (container) (typed FeaturePython)
  n = 0.0921831
FEATURE [App::DocumentObjectGroupPython] Mg_element004  label="Mg_element : 0.135"  # scripted group (container) (typed FeaturePython)
  n = 0.134792
FEATURE [App::DocumentObjectGroupPython] Ca_element013  label="Ca_element : 0.003"  # scripted group (container) (typed FeaturePython)
  n = 0.002883
FEATURE [App::DocumentObjectGroupPython] G4_M3_WAX  # scripted group (container) (typed FeaturePython)
  Dunit = g/cm3
  Dvalue = 1.05
  Group = -> [H_element052,C_element057,O_element058,Mg_element004,Ca_element013]
  conduct = 2
  density = 1
  expand = 3
  formula = G4_M3_WAX
  name = G4_M3_WAX
  specific = 4
FEATURE [App::DocumentObjectGroupPython] Mg_element005  label="Mg_element : 1"  # scripted group (container) (typed FeaturePython)
  n = 1
  ref = Mg_element
FEATURE [App::DocumentObjectGroupPython] C_element058  label="C_element : 031"  # scripted group (container) (typed FeaturePython)
  n = 1
  ref = C_element
FEATURE [App::DocumentObjectGroupPython] O_element059  label="O_element : 030"  # scripted group (container) (typed FeaturePython)
  n = 3
  ref = O_element
FEATURE [App::DocumentObjectGroupPython] G4_MAGNESIUM_CARBONATE  # scripted group (container) (typed FeaturePython)
  Dunit = g/cm3
  Dvalue = 2.958
  Group = -> [Mg_element005,C_element058,O_element059]
  conduct = 2
  density = 1
  expand = 3
  formula = G4_MAGNESIUM_CARBONATE
  name = G4_MAGNESIUM_CARBONATE
  specific = 4
FEATURE [App::DocumentObjectGroupPython] Mg_element006  label="Mg_element : 002"  # scripted group (container) (typed FeaturePython)
  n = 1
  ref = Mg_element
FEATURE [App::DocumentObjectGroupPython] F_element013  label="F_element : 005"  # scripted group (container) (typed FeaturePython)
  n = 2
  ref = F_element
FEATURE [App::DocumentObjectGroupPython] G4_MAGNESIUM_FLUORIDE  # scripted group (container) (typed FeaturePython)
  Dunit = g/cm3
  Dvalue = 3
  Group = -> [Mg_element006,F_element013]
  conduct = 2
  density = 1
  expand = 3
  formula = G4_MAGNESIUM_FLUORIDE
  name = G4_MAGNESIUM_FLUORIDE
  specific = 4
FEATURE [App::DocumentObjectGroupPython] Mg_element007  label="Mg_element : 003"  # scripted group (container) (typed FeaturePython)
  n = 1
  ref = Mg_element
FEATURE [App::DocumentObjectGroupPython] O_element060  label="O_element : 031"  # scripted group (container) (typed FeaturePython)
  n = 1
  ref = O_element
FEATURE [App::DocumentObjectGroupPython] G4_MAGNESIUM_OXIDE  # scripted group (container) (typed FeaturePython)
  Dunit = g/cm3
  Dvalue = 3.58
  Group = -> [Mg_element007,O_element060]
  conduct = 2
  density = 1
  expand = 3
  formula = G4_MAGNESIUM_OXIDE
  name = G4_MAGNESIUM_OXIDE
  specific = 4
FEATURE [App::DocumentObjectGroupPython] Mg_element008  label="Mg_element : 004"  # scripted group (container) (typed FeaturePython)
  n = 1
  ref = Mg_element
FEATURE [App::DocumentObjectGroupPython] B_element006  label="B_element : 006"  # scripted group (container) (typed FeaturePython)
  n = 4
  ref = B_element
FEATURE [App::DocumentObjectGroupPython] O_element061  label="O_element : 032"  # scripted group (container) (typed FeaturePython)
  n = 7
  ref = O_element
FEATURE [App::DocumentObjectGroupPython] G4_MAGNESIUM_TETRABORATE  # scripted group (container) (typed FeaturePython)
  Dunit = g/cm3
  Dvalue = 2.53
  Group = -> [Mg_element008,B_element006,O_element061]
  conduct = 2
  density = 1
  expand = 3
  formula = G4_MAGNESIUM_TETRABORATE
  name = G4_MAGNESIUM_TETRABORATE
  specific = 4
FEATURE [App::DocumentObjectGroupPython] Hg_element001  label="Hg_element : 1"  # scripted group (container) (typed FeaturePython)
  n = 1
  ref = Hg_element
FEATURE [App::DocumentObjectGroupPython] I_element004  label="I_element : 2"  # scripted group (container) (typed FeaturePython)
  n = 2
  ref = I_element
FEATURE [App::DocumentObjectGroupPython] G4_MERCURIC_IODIDE  # scripted group (container) (typed FeaturePython)
  Dunit = g/cm3
  Dvalue = 6.36
  Group = -> [Hg_element001,I_element004]
  conduct = 2
  density = 1
  expand = 3
  formula = G4_MERCURIC_IODIDE
  name = G4_MERCURIC_IODIDE
  specific = 4
FEATURE [App::DocumentObjectGroupPython] C_element059  label="C_element : 032"  # scripted group (container) (typed FeaturePython)
  n = 1
  ref = C_element
FEATURE [App::DocumentObjectGroupPython] H_element053  label="H_element : 028"  # scripted group (container) (typed FeaturePython)
  n = 4
  ref = H_element
FEATURE [App::DocumentObjectGroupPython] G4_METHANE  # scripted group (container) (typed FeaturePython)
  Dunit = g/cm3
  Dvalue = 0.000667151
  Group = -> [C_element059,H_element053]
  conduct = 2
  density = 1
  expand = 3
  formula = G4_METHANE
  name = G4_METHANE
  specific = 4
FEATURE [App::DocumentObjectGroupPython] C_element060  label="C_element : 033"  # scripted group (container) (typed FeaturePython)
  n = 1
  ref = C_element
FEATURE [App::DocumentObjectGroupPython] H_element054  label="H_element : 029"  # scripted group (container) (typed FeaturePython)
  n = 4
  ref = H_element
FEATURE [App::DocumentObjectGroupPython] O_element062  label="O_element : 033"  # scripted group (container) (typed FeaturePython)
  n = 1
  ref = O_element
FEATURE [App::DocumentObjectGroupPython] G4_METHANOL  # scripted group (container) (typed FeaturePython)
  Dunit = g/cm3
  Dvalue = 0.7914
  Group = -> [C_element060,H_element054,O_element062]
  conduct = 2
  density = 1
  expand = 3
  formula = G4_METHANOL
  name = G4_METHANOL
  specific = 4
FEATURE [App::DocumentObjectGroupPython] H_element055  label="H_element : 0.134"  # scripted group (container) (typed FeaturePython)
  n = 0.13404
FEATURE [App::DocumentObjectGroupPython] C_element061  label="C_element : 0.778"  # scripted group (container) (typed FeaturePython)
  n = 0.77796
FEATURE [App::DocumentObjectGroupPython] O_element063  label="O_element : 0.035"  # scripted group (container) (typed FeaturePython)
  n = 0.03502
FEATURE [App::DocumentObjectGroupPython] Mg_element009  label="Mg_element : 0.039"  # scripted group (container) (typed FeaturePython)
  n = 0.038594
FEATURE [App::DocumentObjectGroupPython] Ti_element002  label="Ti_element : 0.014"  # scripted group (container) (typed FeaturePython)
  n = 0.014386
FEATURE [App::DocumentObjectGroupPython] G4_MIX_D_WAX  # scripted group (container) (typed FeaturePython)
  Dunit = g/cm3
  Dvalue = 0.99
  Group = -> [H_element055,C_element061,O_element063,Mg_element009,Ti_element002]
  conduct = 2
  density = 1
  expand = 3
  formula = G4_MIX_D_WAX
  name = G4_MIX_D_WAX
  specific = 4
FEATURE [App::DocumentObjectGroupPython] H_element056  label="H_element : 0.135"  # scripted group (container) (typed FeaturePython)
  n = 0.081192
FEATURE [App::DocumentObjectGroupPython] C_element062  label="C_element : 0.583"  # scripted group (container) (typed FeaturePython)
  n = 0.583442
FEATURE [App::DocumentObjectGroupPython] N_element024  label="N_element : 0.018"  # scripted group (container) (typed FeaturePython)
  n = 0.017798
FEATURE [App::DocumentObjectGroupPython] O_element064  label="O_element : 0.186"  # scripted group (container) (typed FeaturePython)
  n = 0.186381
FEATURE [App::DocumentObjectGroupPython] Mg_element010  label="Mg_element : 0.130"  # scripted group (container) (typed FeaturePython)
  n = 0.130287
FEATURE [App::DocumentObjectGroupPython] Cl_element015  label="Cl_element : 0.588"  # scripted group (container) (typed FeaturePython)
  n = 0.0009
FEATURE [App::DocumentObjectGroupPython] G4_MS20_TISSUE  # scripted group (container) (typed FeaturePython)
  Dunit = g/cm3
  Dvalue = 1
  Group = -> [H_element056,C_element062,N_element024,O_element064,Mg_element010,Cl_element015]
  conduct = 2
  density = 1
  expand = 3
  formula = G4_MS20_TISSUE
  name = G4_MS20_TISSUE
  specific = 4
FEATURE [App::DocumentObjectGroupPython] H_element057  label="H_element : 0.136"  # scripted group (container) (typed FeaturePython)
  n = 0.102
FEATURE [App::DocumentObjectGroupPython] C_element063  label="C_element : 0.143"  # scripted group (container) (typed FeaturePython)
  n = 0.143
FEATURE [App::DocumentObjectGroupPython] N_element025  label="N_element : 0.034"  # scripted group (container) (typed FeaturePython)
  n = 0.034
FEATURE [App::DocumentObjectGroupPython] O_element065  label="O_element : 0.710"  # scripted group (container) (typed FeaturePython)
  n = 0.71
FEATURE [App::DocumentObjectGroupPython] Na_element011  label="Na_element : 0.098"  # scripted group (container) (typed FeaturePython)
  n = 0.001
FEATURE [App::DocumentObjectGroupPython] P_element007  label="P_element : 0.002"  # scripted group (container) (typed FeaturePython)
  n = 0.002
FEATURE [App::DocumentObjectGroupPython] S_element017  label="S_element : 0.018"  # scripted group (container) (typed FeaturePython)
  n = 0.003
FEATURE [App::DocumentObjectGroupPython] Cl_element016  label="Cl_element : 0.589"  # scripted group (container) (typed FeaturePython)
  n = 0.001
FEATURE [App::DocumentObjectGroupPython] K_element006  label="K_element : 0.004"  # scripted group (container) (typed FeaturePython)
  n = 0.004
FEATURE [App::DocumentObjectGroupPython] G4_MUSCLE_SKELETAL_ICRP  # scripted group (container) (typed FeaturePython)
  Dunit = g/cm3
  Dvalue = 1.05
  Group = -> [H_element057,C_element063,N_element025,O_element065,Na_element011,P_element007,S_element017,Cl_element016,K_element006]
  conduct = 2
  density = 1
  expand = 3
  formula = G4_MUSCLE_SKELETAL_ICRP
  name = G4_MUSCLE_SKELETAL_ICRP
  specific = 4
FEATURE [App::DocumentObjectGroupPython] H_element058  label="H_element : 0.137"  # scripted group (container) (typed FeaturePython)
  n = 0.102102
FEATURE [App::DocumentObjectGroupPython] C_element064  label="C_element : 0.123"  # scripted group (container) (typed FeaturePython)
  n = 0.123123
FEATURE [App::DocumentObjectGroupPython] N_element026  label="N_element : 0.756"  # scripted group (container) (typed FeaturePython)
  n = 0.035035
FEATURE [App::DocumentObjectGroupPython] O_element066  label="O_element : 0.730"  # scripted group (container) (typed FeaturePython)
  n = 0.72973
FEATURE [App::DocumentObjectGroupPython] Na_element012  label="Na_element : 0.099"  # scripted group (container) (typed FeaturePython)
  n = 0.001001
FEATURE [App::DocumentObjectGroupPython] P_element008  label="P_element : 0.106"  # scripted group (container) (typed FeaturePython)
  n = 0.002002
FEATURE [App::DocumentObjectGroupPython] S_element018  label="S_element : 0.019"  # scripted group (container) (typed FeaturePython)
  n = 0.004004
FEATURE [App::DocumentObjectGroupPython] K_element007  label="K_element : 0.016"  # scripted group (container) (typed FeaturePython)
  n = 0.003003
FEATURE [App::DocumentObjectGroupPython] G4_MUSCLE_STRIATED_ICRU  # scripted group (container) (typed FeaturePython)
  Dunit = g/cm3
  Dvalue = 1.04
  Group = -> [H_element058,C_element064,N_element026,O_element066,Na_element012,P_element008,S_element018,K_element007]
  conduct = 2
  density = 1
  expand = 3
  formula = G4_MUSCLE_STRIATED_ICRU
  name = G4_MUSCLE_STRIATED_ICRU
  specific = 4
FEATURE [App::DocumentObjectGroupPython] H_element059  label="H_element : 0.098"  # scripted group (container) (typed FeaturePython)
  n = 0.0982341
FEATURE [App::DocumentObjectGroupPython] C_element065  label="C_element : 0.156"  # scripted group (container) (typed FeaturePython)
  n = 0.156214
FEATURE [App::DocumentObjectGroupPython] N_element027  label="N_element : 0.757"  # scripted group (container) (typed FeaturePython)
  n = 0.035451
FEATURE [App::DocumentObjectGroupPython] O_element067  label="O_element : 0.880"  # scripted group (container) (typed FeaturePython)
  n = 0.710101
FEATURE [App::DocumentObjectGroupPython] G4_MUSCLE_WITH_SUCROSE  # scripted group (container) (typed FeaturePython)
  Dunit = g/cm3
  Dvalue = 1.11
  Group = -> [H_element059,C_element065,N_element027,O_element067]
  conduct = 2
  density = 1
  expand = 3
  formula = G4_MUSCLE_WITH_SUCROSE
  name = G4_MUSCLE_WITH_SUCROSE
  specific = 4
FEATURE [App::DocumentObjectGroupPython] H_element060  label="H_element : 0.138"  # scripted group (container) (typed FeaturePython)
  n = 0.101969
FEATURE [App::DocumentObjectGroupPython] C_element066  label="C_element : 0.120"  # scripted group (container) (typed FeaturePython)
  n = 0.120058
FEATURE [App::DocumentObjectGroupPython] N_element028  label="N_element : 0.758"  # scripted group (container) (typed FeaturePython)
  n = 0.035451
FEATURE [App::DocumentObjectGroupPython] O_element068  label="O_element : 0.743"  # scripted group (container) (typed FeaturePython)
  n = 0.742522
FEATURE [App::DocumentObjectGroupPython] G4_MUSCLE_WITHOUT_SUCROSE  # scripted group (container) (typed FeaturePython)
  Dunit = g/cm3
  Dvalue = 1.07
  Group = -> [H_element060,C_element066,N_element028,O_element068]
  conduct = 2
  density = 1
  expand = 3
  formula = G4_MUSCLE_WITHOUT_SUCROSE
  name = G4_MUSCLE_WITHOUT_SUCROSE
  specific = 4
FEATURE [App::DocumentObjectGroupPython] C_element067  label="C_element : 10"  # scripted group (container) (typed FeaturePython)
  n = 10
  ref = C_element
FEATURE [App::DocumentObjectGroupPython] H_element061  label="H_element : 030"  # scripted group (container) (typed FeaturePython)
  n = 8
  ref = H_element
FEATURE [App::DocumentObjectGroupPython] G4_NAPHTHALENE  # scripted group (container) (typed FeaturePython)
  Dunit = g/cm3
  Dvalue = 1.145
  Group = -> [C_element067,H_element061]
  conduct = 2
  density = 1
  expand = 3
  formula = G4_NAPHTHALENE
  name = G4_NAPHTHALENE
  specific = 4
FEATURE [App::DocumentObjectGroupPython] C_element068  label="C_element : 034"  # scripted group (container) (typed FeaturePython)
  n = 6
  ref = C_element
FEATURE [App::DocumentObjectGroupPython] H_element062  label="H_element : 031"  # scripted group (container) (typed FeaturePython)
  n = 5
  ref = H_element
FEATURE [App::DocumentObjectGroupPython] N_element029  label="N_element : 012"  # scripted group (container) (typed FeaturePython)
  n = 1
  ref = N_element
FEATURE [App::DocumentObjectGroupPython] O_element069  label="O_element : 034"  # scripted group (container) (typed FeaturePython)
  n = 2
  ref = O_element
FEATURE [App::DocumentObjectGroupPython] G4_NITROBENZENE  # scripted group (container) (typed FeaturePython)
  Dunit = g/cm3
  Dvalue = 1.19867
  Group = -> [C_element068,H_element062,N_element029,O_element069]
  conduct = 2
  density = 1
  expand = 3
  formula = G4_NITROBENZENE
  name = G4_NITROBENZENE
  specific = 4
FEATURE [App::DocumentObjectGroupPython] N_element030  label="N_element : 013"  # scripted group (container) (typed FeaturePython)
  n = 2
  ref = N_element
FEATURE [App::DocumentObjectGroupPython] O_element070  label="O_element : 035"  # scripted group (container) (typed FeaturePython)
  n = 1
  ref = O_element
FEATURE [App::DocumentObjectGroupPython] G4_NITROUS_OXIDE  # scripted group (container) (typed FeaturePython)
  Dunit = g/cm3
  Dvalue = 0.00183094
  Group = -> [N_element030,O_element070]
  conduct = 2
  density = 1
  expand = 3
  formula = G4_NITROUS_OXIDE
  name = G4_NITROUS_OXIDE
  specific = 4
FEATURE [App::DocumentObjectGroupPython] H_element063  label="H_element : 0.104"  # scripted group (container) (typed FeaturePython)
  n = 0.103509
FEATURE [App::DocumentObjectGroupPython] C_element069  label="C_element : 0.648"  # scripted group (container) (typed FeaturePython)
  n = 0.648416
FEATURE [App::DocumentObjectGroupPython] N_element031  label="N_element : 0.100"  # scripted group (container) (typed FeaturePython)
  n = 0.0995361
FEATURE [App::DocumentObjectGroupPython] O_element071  label="O_element : 0.149"  # scripted group (container) (typed FeaturePython)
  n = 0.148539
FEATURE [App::DocumentObjectGroupPython] G4_NYLON_8062  label="G4_NYLON-8062"  # scripted group (container) (typed FeaturePython)
  Dunit = g/cm3
  Dvalue = 1.08
  Group = -> [H_element063,C_element069,N_element031,O_element071]
  conduct = 2
  density = 1
  expand = 3
  formula = G4_NYLON-8062
  name = G4_NYLON-8062
  specific = 4
FEATURE [App::DocumentObjectGroupPython] C_element070  label="C_element : 035"  # scripted group (container) (typed FeaturePython)
  n = 6
  ref = C_element
FEATURE [App::DocumentObjectGroupPython] H_element064  label="H_element : 11"  # scripted group (container) (typed FeaturePython)
  n = 11
  ref = H_element
FEATURE [App::DocumentObjectGroupPython] N_element032  label="N_element : 014"  # scripted group (container) (typed FeaturePython)
  n = 1
  ref = N_element
FEATURE [App::DocumentObjectGroupPython] O_element072  label="O_element : 036"  # scripted group (container) (typed FeaturePython)
  n = 1
  ref = O_element
FEATURE [App::DocumentObjectGroupPython] G4_NYLON_6_6  label="G4_NYLON-6-6"  # scripted group (container) (typed FeaturePython)
  Dunit = g/cm3
  Dvalue = 1.14
  Group = -> [C_element070,H_element064,N_element032,O_element072]
  conduct = 2
  density = 1
  expand = 3
  formula = G4_NYLON-6-6
  name = G4_NYLON-6-6
  specific = 4
FEATURE [App::DocumentObjectGroupPython] H_element065  label="H_element : 0.139"  # scripted group (container) (typed FeaturePython)
  n = 0.107062
FEATURE [App::DocumentObjectGroupPython] C_element071  label="C_element : 0.680"  # scripted group (container) (typed FeaturePython)
  n = 0.680449
FEATURE [App::DocumentObjectGroupPython] N_element033  label="N_element : 0.099"  # scripted group (container) (typed FeaturePython)
  n = 0.099189
FEATURE [App::DocumentObjectGroupPython] O_element073  label="O_element : 0.113"  # scripted group (container) (typed FeaturePython)
  n = 0.1133
FEATURE [App::DocumentObjectGroupPython] G4_NYLON_6_10  label="G4_NYLON-6-10"  # scripted group (container) (typed FeaturePython)
  Dunit = g/cm3
  Dvalue = 1.14
  Group = -> [H_element065,C_element071,N_element033,O_element073]
  conduct = 2
  density = 1
  expand = 3
  formula = G4_NYLON-6-10
  name = G4_NYLON-6-10
  specific = 4
FEATURE [App::DocumentObjectGroupPython] H_element066  label="H_element : 0.140"  # scripted group (container) (typed FeaturePython)
  n = 0.115476
FEATURE [App::DocumentObjectGroupPython] C_element072  label="C_element : 0.721"  # scripted group (container) (typed FeaturePython)
  n = 0.720818
FEATURE [App::DocumentObjectGroupPython] N_element034  label="N_element : 0.076"  # scripted group (container) (typed FeaturePython)
  n = 0.0764169
FEATURE [App::DocumentObjectGroupPython] O_element074  label="O_element : 0.087"  # scripted group (container) (typed FeaturePython)
  n = 0.0872889
FEATURE [App::DocumentObjectGroupPython] G4_NYLON_11_RILSAN  label="G4_NYLON-11_RILSAN"  # scripted group (container) (typed FeaturePython)
  Dunit = g/cm3
  Dvalue = 1.425
  Group = -> [H_element066,C_element072,N_element034,O_element074]
  conduct = 2
  density = 1
  expand = 3
  formula = G4_NYLON-11_RILSAN
  name = G4_NYLON-11_RILSAN
  specific = 4
FEATURE [App::DocumentObjectGroupPython] C_element073  label="C_element : 8"  # scripted group (container) (typed FeaturePython)
  n = 8
  ref = C_element
FEATURE [App::DocumentObjectGroupPython] H_element067  label="H_element : 18"  # scripted group (container) (typed FeaturePython)
  n = 18
  ref = H_element
FEATURE [App::DocumentObjectGroupPython] G4_OCTANE  # scripted group (container) (typed FeaturePython)
  Dunit = g/cm3
  Dvalue = 0.7026
  Group = -> [C_element073,H_element067]
  conduct = 2
  density = 1
  expand = 3
  formula = G4_OCTANE
  name = G4_OCTANE
  specific = 4
FEATURE [App::DocumentObjectGroupPython] C_element074  label="C_element : 25"  # scripted group (container) (typed FeaturePython)
  n = 25
  ref = C_element
FEATURE [App::DocumentObjectGroupPython] H_element068  label="H_element : 52"  # scripted group (container) (typed FeaturePython)
  n = 52
  ref = H_element
FEATURE [App::DocumentObjectGroupPython] G4_PARAFFIN  # scripted group (container) (typed FeaturePython)
  Dunit = g/cm3
  Dvalue = 0.93
  Group = -> [C_element074,H_element068]
  conduct = 2
  density = 1
  expand = 3
  formula = G4_PARAFFIN
  name = G4_PARAFFIN
  specific = 4
FEATURE [App::DocumentObjectGroupPython] C_element075  label="C_element : 036"  # scripted group (container) (typed FeaturePython)
  n = 5
  ref = C_element
FEATURE [App::DocumentObjectGroupPython] H_element069  label="H_element : 032"  # scripted group (container) (typed FeaturePython)
  n = 12
  ref = H_element
FEATURE [App::DocumentObjectGroupPython] G4_N_PENTANE  label="G4_N-PENTANE"  # scripted group (container) (typed FeaturePython)
  Dunit = g/cm3
  Dvalue = 0.6262
  Group = -> [C_element075,H_element069]
  conduct = 2
  density = 1
  expand = 3
  formula = G4_N-PENTANE
  name = G4_N-PENTANE
  specific = 4
FEATURE [App::DocumentObjectGroupPython] H_element070  label="H_element : 0.014"  # scripted group (container) (typed FeaturePython)
  n = 0.0141
FEATURE [App::DocumentObjectGroupPython] C_element076  label="C_element : 0.072"  # scripted group (container) (typed FeaturePython)
  n = 0.072261
FEATURE [App::DocumentObjectGroupPython] N_element035  label="N_element : 0.019"  # scripted group (container) (typed FeaturePython)
  n = 0.01932
FEATURE [App::DocumentObjectGroupPython] O_element075  label="O_element : 0.066"  # scripted group (container) (typed FeaturePython)
  n = 0.066101
FEATURE [App::DocumentObjectGroupPython] S_element019  label="S_element : 0.020"  # scripted group (container) (typed FeaturePython)
  n = 0.00189
FEATURE [App::DocumentObjectGroupPython] Br_element004  label="Br_element : 0.349"  # scripted group (container) (typed FeaturePython)
  n = 0.349103
FEATURE [App::DocumentObjectGroupPython] Ag_element001  label="Ag_element : 0.474"  # scripted group (container) (typed FeaturePython)
  n = 0.474105
FEATURE [App::DocumentObjectGroupPython] I_element005  label="I_element : 0.003"  # scripted group (container) (typed FeaturePython)
  n = 0.00312
FEATURE [App::DocumentObjectGroupPython] G4_PHOTO_EMULSION  # scripted group (container) (typed FeaturePython)
  Dunit = g/cm3
  Dvalue = 3.815
  Group = -> [H_element070,C_element076,N_element035,O_element075,S_element019,Br_element004,Ag_element001,I_element005]
  conduct = 2
  density = 1
  expand = 3
  formula = G4_PHOTO_EMULSION
  name = G4_PHOTO_EMULSION
  specific = 4
FEATURE [App::DocumentObjectGroupPython] C_element077  label="C_element : 9"  # scripted group (container) (typed FeaturePython)
  n = 9
  ref = C_element
FEATURE [App::DocumentObjectGroupPython] H_element071  label="H_element : 033"  # scripted group (container) (typed FeaturePython)
  n = 10
  ref = H_element
FEATURE [App::DocumentObjectGroupPython] G4_PLASTIC_SC_VINYLTOLUENE  # scripted group (container) (typed FeaturePython)
  Dunit = g/cm3
  Dvalue = 1.032
  Group = -> [C_element077,H_element071]
  conduct = 2
  density = 1
  expand = 3
  formula = G4_PLASTIC_SC_VINYLTOLUENE
  name = G4_PLASTIC_SC_VINYLTOLUENE
  specific = 4
FEATURE [App::DocumentObjectGroupPython] Pu_element001  label="Pu_element : 1"  # scripted group (container) (typed FeaturePython)
  n = 1
  ref = Pu_element
FEATURE [App::DocumentObjectGroupPython] O_element076  label="O_element : 037"  # scripted group (container) (typed FeaturePython)
  n = 2
  ref = O_element
FEATURE [App::DocumentObjectGroupPython] G4_PLUTONIUM_DIOXIDE  # scripted group (container) (typed FeaturePython)
  Dunit = g/cm3
  Dvalue = 11.46
  Group = -> [Pu_element001,O_element076]
  conduct = 2
  density = 1
  expand = 3
  formula = G4_PLUTONIUM_DIOXIDE
  name = G4_PLUTONIUM_DIOXIDE
  specific = 4
FEATURE [App::DocumentObjectGroupPython] C_element078  label="C_element : 037"  # scripted group (container) (typed FeaturePython)
  n = 3
  ref = C_element
FEATURE [App::DocumentObjectGroupPython] H_element072  label="H_element : 034"  # scripted group (container) (typed FeaturePython)
  n = 3
  ref = H_element
FEATURE [App::DocumentObjectGroupPython] N_element036  label="N_element : 015"  # scripted group (container) (typed FeaturePython)
  n = 1
  ref = N_element
FEATURE [App::DocumentObjectGroupPython] G4_POLYACRYLONITRILE  # scripted group (container) (typed FeaturePython)
  Dunit = g/cm3
  Dvalue = 1.17
  Group = -> [C_element078,H_element072,N_element036]
  conduct = 2
  density = 1
  expand = 3
  formula = G4_POLYACRYLONITRILE
  name = G4_POLYACRYLONITRILE
  specific = 4
FEATURE [App::DocumentObjectGroupPython] C_element079  label="C_element : 16"  # scripted group (container) (typed FeaturePython)
  n = 16
  ref = C_element
FEATURE [App::DocumentObjectGroupPython] H_element073  label="H_element : 035"  # scripted group (container) (typed FeaturePython)
  n = 14
  ref = H_element
FEATURE [App::DocumentObjectGroupPython] O_element077  label="O_element : 038"  # scripted group (container) (typed FeaturePython)
  n = 3
  ref = O_element
FEATURE [App::DocumentObjectGroupPython] G4_POLYCARBONATE  # scripted group (container) (typed FeaturePython)
  Dunit = g/cm3
  Dvalue = 1.2
  Group = -> [C_element079,H_element073,O_element077]
  conduct = 2
  density = 1
  expand = 3
  formula = G4_POLYCARBONATE
  name = G4_POLYCARBONATE
  specific = 4
FEATURE [App::DocumentObjectGroupPython] C_element080  label="C_element : 038"  # scripted group (container) (typed FeaturePython)
  n = 8
  ref = C_element
FEATURE [App::DocumentObjectGroupPython] H_element074  label="H_element : 036"  # scripted group (container) (typed FeaturePython)
  n = 7
  ref = H_element
FEATURE [App::DocumentObjectGroupPython] Cl_element017  label="Cl_element : 007"  # scripted group (container) (typed FeaturePython)
  n = 1
  ref = Cl_element
FEATURE [App::DocumentObjectGroupPython] G4_POLYCHLOROSTYRENE  # scripted group (container) (typed FeaturePython)
  Dunit = g/cm3
  Dvalue = 1.3
  Group = -> [C_element080,H_element074,Cl_element017]
  conduct = 2
  density = 1
  expand = 3
  formula = G4_POLYCHLOROSTYRENE
  name = G4_POLYCHLOROSTYRENE
  specific = 4
FEATURE [App::DocumentObjectGroupPython] C_element081  label="C_element : 039"  # scripted group (container) (typed FeaturePython)
  n = 1
  ref = C_element
FEATURE [App::DocumentObjectGroupPython] H_element075  label="H_element : 037"  # scripted group (container) (typed FeaturePython)
  n = 2
  ref = H_element
FEATURE [App::DocumentObjectGroupPython] G4_POLYETHYLENE  # scripted group (container) (typed FeaturePython)
  Dunit = g/cm3
  Dvalue = 0.94
  Group = -> [C_element081,H_element075]
  conduct = 2
  density = 1
  expand = 3
  formula = G4_POLYETHYLENE
  name = G4_POLYETHYLENE
  specific = 4
FEATURE [App::DocumentObjectGroupPython] C_element082  label="C_element : 040"  # scripted group (container) (typed FeaturePython)
  n = 10
  ref = C_element
FEATURE [App::DocumentObjectGroupPython] H_element076  label="H_element : 038"  # scripted group (container) (typed FeaturePython)
  n = 8
  ref = H_element
FEATURE [App::DocumentObjectGroupPython] O_element078  label="O_element : 039"  # scripted group (container) (typed FeaturePython)
  n = 4
  ref = O_element
FEATURE [App::DocumentObjectGroupPython] G4_MYLAR  # scripted group (container) (typed FeaturePython)
  Dunit = g/cm3
  Dvalue = 1.4
  Group = -> [C_element082,H_element076,O_element078]
  conduct = 2
  density = 1
  expand = 3
  formula = G4_MYLAR
  name = G4_MYLAR
  specific = 4
FEATURE [App::DocumentObjectGroupPython] C_element083  label="C_element : 041"  # scripted group (container) (typed FeaturePython)
  n = 5
  ref = C_element
FEATURE [App::DocumentObjectGroupPython] H_element077  label="H_element : 039"  # scripted group (container) (typed FeaturePython)
  n = 8
  ref = H_element
FEATURE [App::DocumentObjectGroupPython] O_element079  label="O_element : 040"  # scripted group (container) (typed FeaturePython)
  n = 2
  ref = O_element
FEATURE [App::DocumentObjectGroupPython] G4_PLEXIGLASS  # scripted group (container) (typed FeaturePython)
  Dunit = g/cm3
  Dvalue = 1.19
  Group = -> [C_element083,H_element077,O_element079]
  conduct = 2
  density = 1
  expand = 3
  formula = G4_PLEXIGLASS
  name = G4_PLEXIGLASS
  specific = 4
FEATURE [App::DocumentObjectGroupPython] C_element084  label="C_element : 042"  # scripted group (container) (typed FeaturePython)
  n = 1
  ref = C_element
FEATURE [App::DocumentObjectGroupPython] H_element078  label="H_element : 040"  # scripted group (container) (typed FeaturePython)
  n = 2
  ref = H_element
FEATURE [App::DocumentObjectGroupPython] O_element080  label="O_element : 041"  # scripted group (container) (typed FeaturePython)
  n = 1
  ref = O_element
FEATURE [App::DocumentObjectGroupPython] G4_POLYOXYMETHYLENE  # scripted group (container) (typed FeaturePython)
  Dunit = g/cm3
  Dvalue = 1.425
  Group = -> [C_element084,H_element078,O_element080]
  conduct = 2
  density = 1
  expand = 3
  formula = G4_POLYOXYMETHYLENE
  name = G4_POLYOXYMETHYLENE
  specific = 4
FEATURE [App::DocumentObjectGroupPython] C_element085  label="C_element : 043"  # scripted group (container) (typed FeaturePython)
  n = 2
  ref = C_element
FEATURE [App::DocumentObjectGroupPython] H_element079  label="H_element : 041"  # scripted group (container) (typed FeaturePython)
  n = 4
  ref = H_element
FEATURE [App::DocumentObjectGroupPython] G4_POLYPROPYLENE  # scripted group (container) (typed FeaturePython)
  Dunit = g/cm3
  Dvalue = 0.9
  Group = -> [C_element085,H_element079]
  conduct = 2
  density = 1
  expand = 3
  formula = G4_POLYPROPYLENE
  name = G4_POLYPROPYLENE
  specific = 4
FEATURE [App::DocumentObjectGroupPython] C_element086  label="C_element : 044"  # scripted group (container) (typed FeaturePython)
  n = 8
  ref = C_element
FEATURE [App::DocumentObjectGroupPython] H_element080  label="H_element : 042"  # scripted group (container) (typed FeaturePython)
  n = 8
  ref = H_element
FEATURE [App::DocumentObjectGroupPython] G4_POLYSTYRENE  # scripted group (container) (typed FeaturePython)
  Dunit = g/cm3
  Dvalue = 1.06
  Group = -> [C_element086,H_element080]
  conduct = 2
  density = 1
  expand = 3
  formula = G4_POLYSTYRENE
  name = G4_POLYSTYRENE
  specific = 4
FEATURE [App::DocumentObjectGroupPython] C_element087  label="C_element : 045"  # scripted group (container) (typed FeaturePython)
  n = 2
  ref = C_element
FEATURE [App::DocumentObjectGroupPython] F_element014  label="F_element : 4"  # scripted group (container) (typed FeaturePython)
  n = 4
  ref = F_element
FEATURE [App::DocumentObjectGroupPython] G4_TEFLON  # scripted group (container) (typed FeaturePython)
  Dunit = g/cm3
  Dvalue = 2.2
  Group = -> [C_element087,F_element014]
  conduct = 2
  density = 1
  expand = 3
  formula = G4_TEFLON
  name = G4_TEFLON
  specific = 4
FEATURE [App::DocumentObjectGroupPython] C_element088  label="C_element : 046"  # scripted group (container) (typed FeaturePython)
  n = 2
  ref = C_element
FEATURE [App::DocumentObjectGroupPython] F_element015  label="F_element : 006"  # scripted group (container) (typed FeaturePython)
  n = 3
  ref = F_element
FEATURE [App::DocumentObjectGroupPython] Cl_element018  label="Cl_element : 008"  # scripted group (container) (typed FeaturePython)
  n = 1
  ref = Cl_element
FEATURE [App::DocumentObjectGroupPython] G4_POLYTRIFLUOROCHLOROETHYLENE  # scripted group (container) (typed FeaturePython)
  Dunit = g/cm3
  Dvalue = 2.1
  Group = -> [C_element088,F_element015,Cl_element018]
  conduct = 2
  density = 1
  expand = 3
  formula = G4_POLYTRIFLUOROCHLOROETHYLENE
  name = G4_POLYTRIFLUOROCHLOROETHYLENE
  specific = 4
FEATURE [App::DocumentObjectGroupPython] C_element089  label="C_element : 047"  # scripted group (container) (typed FeaturePython)
  n = 4
  ref = C_element
FEATURE [App::DocumentObjectGroupPython] H_element081  label="H_element : 043"  # scripted group (container) (typed FeaturePython)
  n = 6
  ref = H_element
FEATURE [App::DocumentObjectGroupPython] O_element081  label="O_element : 042"  # scripted group (container) (typed FeaturePython)
  n = 2
  ref = O_element
FEATURE [App::DocumentObjectGroupPython] G4_POLYVINYL_ACETATE  # scripted group (container) (typed FeaturePython)
  Dunit = g/cm3
  Dvalue = 1.19
  Group = -> [C_element089,H_element081,O_element081]
  conduct = 2
  density = 1
  expand = 3
  formula = G4_POLYVINYL_ACETATE
  name = G4_POLYVINYL_ACETATE
  specific = 4
FEATURE [App::DocumentObjectGroupPython] C_element090  label="C_element : 048"  # scripted group (container) (typed FeaturePython)
  n = 2
  ref = C_element
FEATURE [App::DocumentObjectGroupPython] H_element082  label="H_element : 044"  # scripted group (container) (typed FeaturePython)
  n = 4
  ref = H_element
FEATURE [App::DocumentObjectGroupPython] O_element082  label="O_element : 043"  # scripted group (container) (typed FeaturePython)
  n = 1
  ref = O_element
FEATURE [App::DocumentObjectGroupPython] G4_POLYVINYL_ALCOHOL  # scripted group (container) (typed FeaturePython)
  Dunit = g/cm3
  Dvalue = 1.3
  Group = -> [C_element090,H_element082,O_element082]
  conduct = 2
  density = 1
  expand = 3
  formula = G4_POLYVINYL_ALCOHOL
  name = G4_POLYVINYL_ALCOHOL
  specific = 4
FEATURE [App::DocumentObjectGroupPython] C_element091  label="C_element : 049"  # scripted group (container) (typed FeaturePython)
  n = 8
  ref = C_element
FEATURE [App::DocumentObjectGroupPython] H_element083  label="H_element : 045"  # scripted group (container) (typed FeaturePython)
  n = 14
  ref = H_element
FEATURE [App::DocumentObjectGroupPython] O_element083  label="O_element : 044"  # scripted group (container) (typed FeaturePython)
  n = 2
  ref = O_element
FEATURE [App::DocumentObjectGroupPython] G4_POLYVINYL_BUTYRAL  # scripted group (container) (typed FeaturePython)
  Dunit = g/cm3
  Dvalue = 1.12
  Group = -> [C_element091,H_element083,O_element083]
  conduct = 2
  density = 1
  expand = 3
  formula = G4_POLYVINYL_BUTYRAL
  name = G4_POLYVINYL_BUTYRAL
  specific = 4
FEATURE [App::DocumentObjectGroupPython] C_element092  label="C_element : 050"  # scripted group (container) (typed FeaturePython)
  n = 2
  ref = C_element
FEATURE [App::DocumentObjectGroupPython] H_element084  label="H_element : 046"  # scripted group (container) (typed FeaturePython)
  n = 3
  ref = H_element
FEATURE [App::DocumentObjectGroupPython] Cl_element019  label="Cl_element : 009"  # scripted group (container) (typed FeaturePython)
  n = 1
  ref = Cl_element
FEATURE [App::DocumentObjectGroupPython] G4_POLYVINYL_CHLORIDE  # scripted group (container) (typed FeaturePython)
  Dunit = g/cm3
  Dvalue = 1.3
  Group = -> [C_element092,H_element084,Cl_element019]
  conduct = 2
  density = 1
  expand = 3
  formula = G4_POLYVINYL_CHLORIDE
  name = G4_POLYVINYL_CHLORIDE
  specific = 4
FEATURE [App::DocumentObjectGroupPython] C_element093  label="C_element : 051"  # scripted group (container) (typed FeaturePython)
  n = 2
  ref = C_element
FEATURE [App::DocumentObjectGroupPython] H_element085  label="H_element : 047"  # scripted group (container) (typed FeaturePython)
  n = 2
  ref = H_element
FEATURE [App::DocumentObjectGroupPython] Cl_element020  label="Cl_element : 010"  # scripted group (container) (typed FeaturePython)
  n = 2
  ref = Cl_element
FEATURE [App::DocumentObjectGroupPython] G4_POLYVINYLIDENE_CHLORIDE  # scripted group (container) (typed FeaturePython)
  Dunit = g/cm3
  Dvalue = 1.7
  Group = -> [C_element093,H_element085,Cl_element020]
  conduct = 2
  density = 1
  expand = 3
  formula = G4_POLYVINYLIDENE_CHLORIDE
  name = G4_POLYVINYLIDENE_CHLORIDE
  specific = 4
FEATURE [App::DocumentObjectGroupPython] C_element094  label="C_element : 052"  # scripted group (container) (typed FeaturePython)
  n = 2
  ref = C_element
FEATURE [App::DocumentObjectGroupPython] H_element086  label="H_element : 048"  # scripted group (container) (typed FeaturePython)
  n = 2
  ref = H_element
FEATURE [App::DocumentObjectGroupPython] F_element016  label="F_element : 007"  # scripted group (container) (typed FeaturePython)
  n = 2
  ref = F_element
FEATURE [App::DocumentObjectGroupPython] G4_POLYVINYLIDENE_FLUORIDE  # scripted group (container) (typed FeaturePython)
  Dunit = g/cm3
  Dvalue = 1.76
  Group = -> [C_element094,H_element086,F_element016]
  conduct = 2
  density = 1
  expand = 3
  formula = G4_POLYVINYLIDENE_FLUORIDE
  name = G4_POLYVINYLIDENE_FLUORIDE
  specific = 4
FEATURE [App::DocumentObjectGroupPython] C_element095  label="C_element : 053"  # scripted group (container) (typed FeaturePython)
  n = 6
  ref = C_element
FEATURE [App::DocumentObjectGroupPython] H_element087  label="H_element : 9"  # scripted group (container) (typed FeaturePython)
  n = 9
  ref = H_element
FEATURE [App::DocumentObjectGroupPython] N_element037  label="N_element : 016"  # scripted group (container) (typed FeaturePython)
  n = 1
  ref = N_element
FEATURE [App::DocumentObjectGroupPython] O_element084  label="O_element : 045"  # scripted group (container) (typed FeaturePython)
  n = 1
  ref = O_element
FEATURE [App::DocumentObjectGroupPython] G4_POLYVINYL_PYRROLIDONE  # scripted group (container) (typed FeaturePython)
  Dunit = g/cm3
  Dvalue = 1.25
  Group = -> [C_element095,H_element087,N_element037,O_element084]
  conduct = 2
  density = 1
  expand = 3
  formula = G4_POLYVINYL_PYRROLIDONE
  name = G4_POLYVINYL_PYRROLIDONE
  specific = 4
FEATURE [App::DocumentObjectGroupPython] K_element008  label="K_element : 1"  # scripted group (container) (typed FeaturePython)
  n = 1
  ref = K_element
FEATURE [App::DocumentObjectGroupPython] I_element006  label="I_element : 003"  # scripted group (container) (typed FeaturePython)
  n = 1
  ref = I_element
FEATURE [App::DocumentObjectGroupPython] G4_POTASSIUM_IODIDE  # scripted group (container) (typed FeaturePython)
  Dunit = g/cm3
  Dvalue = 3.13
  Group = -> [K_element008,I_element006]
  conduct = 2
  density = 1
  expand = 3
  formula = G4_POTASSIUM_IODIDE
  name = G4_POTASSIUM_IODIDE
  specific = 4
FEATURE [App::DocumentObjectGroupPython] K_element009  label="K_element : 2"  # scripted group (container) (typed FeaturePython)
  n = 2
  ref = K_element
FEATURE [App::DocumentObjectGroupPython] O_element085  label="O_element : 046"  # scripted group (container) (typed FeaturePython)
  n = 1
  ref = O_element
FEATURE [App::DocumentObjectGroupPython] G4_POTASSIUM_OXIDE  # scripted group (container) (typed FeaturePython)
  Dunit = g/cm3
  Dvalue = 2.32
  Group = -> [K_element009,O_element085]
  conduct = 2
  density = 1
  expand = 3
  formula = G4_POTASSIUM_OXIDE
  name = G4_POTASSIUM_OXIDE
  specific = 4
FEATURE [App::DocumentObjectGroupPython] C_element096  label="C_element : 054"  # scripted group (container) (typed FeaturePython)
  n = 3
  ref = C_element
FEATURE [App::DocumentObjectGroupPython] H_element088  label="H_element : 049"  # scripted group (container) (typed FeaturePython)
  n = 8
  ref = H_element
FEATURE [App::DocumentObjectGroupPython] G4_PROPANE  # scripted group (container) (typed FeaturePython)
  Dunit = g/cm3
  Dvalue = 0.00187939
  Group = -> [C_element096,H_element088]
  conduct = 2
  density = 1
  expand = 3
  formula = G4_PROPANE
  name = G4_PROPANE
  specific = 4
FEATURE [App::DocumentObjectGroupPython] C_element097  label="C_element : 055"  # scripted group (container) (typed FeaturePython)
  n = 3
  ref = C_element
FEATURE [App::DocumentObjectGroupPython] H_element089  label="H_element : 050"  # scripted group (container) (typed FeaturePython)
  n = 8
  ref = H_element
FEATURE [App::DocumentObjectGroupPython] G4_lPROPANE  # scripted group (container) (typed FeaturePython)
  Dunit = g/cm3
  Dvalue = 0.43
  Group = -> [C_element097,H_element089]
  conduct = 2
  density = 1
  expand = 3
  formula = G4_lPROPANE
  name = G4_lPROPANE
  specific = 4
FEATURE [App::DocumentObjectGroupPython] C_element098  label="C_element : 056"  # scripted group (container) (typed FeaturePython)
  n = 3
  ref = C_element
FEATURE [App::DocumentObjectGroupPython] H_element090  label="H_element : 051"  # scripted group (container) (typed FeaturePython)
  n = 8
  ref = H_element
FEATURE [App::DocumentObjectGroupPython] O_element086  label="O_element : 047"  # scripted group (container) (typed FeaturePython)
  n = 1
  ref = O_element
FEATURE [App::DocumentObjectGroupPython] G4_N_PROPYL_ALCOHOL  label="G4_N-PROPYL_ALCOHOL"  # scripted group (container) (typed FeaturePython)
  Dunit = g/cm3
  Dvalue = 0.8035
  Group = -> [C_element098,H_element090,O_element086]
  conduct = 2
  density = 1
  expand = 3
  formula = G4_N-PROPYL_ALCOHOL
  name = G4_N-PROPYL_ALCOHOL
  specific = 4
FEATURE [App::DocumentObjectGroupPython] C_element099  label="C_element : 057"  # scripted group (container) (typed FeaturePython)
  n = 5
  ref = C_element
FEATURE [App::DocumentObjectGroupPython] H_element091  label="H_element : 052"  # scripted group (container) (typed FeaturePython)
  n = 5
  ref = H_element
FEATURE [App::DocumentObjectGroupPython] N_element038  label="N_element : 017"  # scripted group (container) (typed FeaturePython)
  n = 1
  ref = N_element
FEATURE [App::DocumentObjectGroupPython] G4_PYRIDINE  # scripted group (container) (typed FeaturePython)
  Dunit = g/cm3
  Dvalue = 0.9819
  Group = -> [C_element099,H_element091,N_element038]
  conduct = 2
  density = 1
  expand = 3
  formula = G4_PYRIDINE
  name = G4_PYRIDINE
  specific = 4
FEATURE [App::DocumentObjectGroupPython] H_element092  label="H_element : 0.144"  # scripted group (container) (typed FeaturePython)
  n = 0.143711
FEATURE [App::DocumentObjectGroupPython] C_element100  label="C_element : 0.856"  # scripted group (container) (typed FeaturePython)
  n = 0.856289
FEATURE [App::DocumentObjectGroupPython] G4_RUBBER_BUTYL  # scripted group (container) (typed FeaturePython)
  Dunit = g/cm3
  Dvalue = 0.92
  Group = -> [H_element092,C_element100]
  conduct = 2
  density = 1
  expand = 3
  formula = G4_RUBBER_BUTYL
  name = G4_RUBBER_BUTYL
  specific = 4
FEATURE [App::DocumentObjectGroupPython] H_element093  label="H_element : 0.118"  # scripted group (container) (typed FeaturePython)
  n = 0.118371
FEATURE [App::DocumentObjectGroupPython] C_element101  label="C_element : 0.882"  # scripted group (container) (typed FeaturePython)
  n = 0.881629
FEATURE [App::DocumentObjectGroupPython] G4_RUBBER_NATURAL  # scripted group (container) (typed FeaturePython)
  Dunit = g/cm3
  Dvalue = 0.92
  Group = -> [H_element093,C_element101]
  conduct = 2
  density = 1
  expand = 3
  formula = G4_RUBBER_NATURAL
  name = G4_RUBBER_NATURAL
  specific = 4
FEATURE [App::DocumentObjectGroupPython] H_element094  label="H_element : 0.145"  # scripted group (container) (typed FeaturePython)
  n = 0.05692
FEATURE [App::DocumentObjectGroupPython] C_element102  label="C_element : 0.543"  # scripted group (container) (typed FeaturePython)
  n = 0.542646
FEATURE [App::DocumentObjectGroupPython] Cl_element021  label="Cl_element : 0.400"  # scripted group (container) (typed FeaturePython)
  n = 0.400434
FEATURE [App::DocumentObjectGroupPython] G4_RUBBER_NEOPRENE  # scripted group (container) (typed FeaturePython)
  Dunit = g/cm3
  Dvalue = 1.23
  Group = -> [H_element094,C_element102,Cl_element021]
  conduct = 2
  density = 1
  expand = 3
  formula = G4_RUBBER_NEOPRENE
  name = G4_RUBBER_NEOPRENE
  specific = 4
FEATURE [App::DocumentObjectGroupPython] Si_element006  label="Si_element : 1"  # scripted group (container) (typed FeaturePython)
  n = 1
  ref = Si_element
FEATURE [App::DocumentObjectGroupPython] O_element087  label="O_element : 048"  # scripted group (container) (typed FeaturePython)
  n = 2
  ref = O_element
FEATURE [App::DocumentObjectGroupPython] G4_SILICON_DIOXIDE  # scripted group (container) (typed FeaturePython)
  Dunit = g/cm3
  Dvalue = 2.32
  Group = -> [Si_element006,O_element087]
  conduct = 2
  density = 1
  expand = 3
  formula = G4_SILICON_DIOXIDE
  name = G4_SILICON_DIOXIDE
  specific = 4
FEATURE [App::DocumentObjectGroupPython] Ag_element002  label="Ag_element : 1"  # scripted group (container) (typed FeaturePython)
  n = 1
  ref = Ag_element
FEATURE [App::DocumentObjectGroupPython] Br_element005  label="Br_element : 003"  # scripted group (container) (typed FeaturePython)
  n = 1
  ref = Br_element
FEATURE [App::DocumentObjectGroupPython] G4_SILVER_BROMIDE  # scripted group (container) (typed FeaturePython)
  Dunit = g/cm3
  Dvalue = 6.473
  Group = -> [Ag_element002,Br_element005]
  conduct = 2
  density = 1
  expand = 3
  formula = G4_SILVER_BROMIDE
  name = G4_SILVER_BROMIDE
  specific = 4
FEATURE [App::DocumentObjectGroupPython] Ag_element003  label="Ag_element : 002"  # scripted group (container) (typed FeaturePython)
  n = 1
  ref = Ag_element
FEATURE [App::DocumentObjectGroupPython] Cl_element022  label="Cl_element : 011"  # scripted group (container) (typed FeaturePython)
  n = 1
  ref = Cl_element
FEATURE [App::DocumentObjectGroupPython] G4_SILVER_CHLORIDE  # scripted group (container) (typed FeaturePython)
  Dunit = g/cm3
  Dvalue = 5.56
  Group = -> [Ag_element003,Cl_element022]
  conduct = 2
  density = 1
  expand = 3
  formula = G4_SILVER_CHLORIDE
  name = G4_SILVER_CHLORIDE
  specific = 4
FEATURE [App::DocumentObjectGroupPython] Br_element006  label="Br_element : 0.423"  # scripted group (container) (typed FeaturePython)
  n = 0.422895
FEATURE [App::DocumentObjectGroupPython] Ag_element004  label="Ag_element : 0.574"  # scripted group (container) (typed FeaturePython)
  n = 0.573748
FEATURE [App::DocumentObjectGroupPython] I_element007  label="I_element : 0.649"  # scripted group (container) (typed FeaturePython)
  n = 0.003357
FEATURE [App::DocumentObjectGroupPython] G4_SILVER_HALIDES  # scripted group (container) (typed FeaturePython)
  Dunit = g/cm3
  Dvalue = 6.47
  Group = -> [Br_element006,Ag_element004,I_element007]
  conduct = 2
  density = 1
  expand = 3
  formula = G4_SILVER_HALIDES
  name = G4_SILVER_HALIDES
  specific = 4
FEATURE [App::DocumentObjectGroupPython] Ag_element005  label="Ag_element : 003"  # scripted group (container) (typed FeaturePython)
  n = 1
  ref = Ag_element
FEATURE [App::DocumentObjectGroupPython] I_element008  label="I_element : 004"  # scripted group (container) (typed FeaturePython)
  n = 1
  ref = I_element
FEATURE [App::DocumentObjectGroupPython] G4_SILVER_IODIDE  # scripted group (container) (typed FeaturePython)
  Dunit = g/cm3
  Dvalue = 6.01
  Group = -> [Ag_element005,I_element008]
  conduct = 2
  density = 1
  expand = 3
  formula = G4_SILVER_IODIDE
  name = G4_SILVER_IODIDE
  specific = 4
FEATURE [App::DocumentObjectGroupPython] H_element095  label="H_element : 0.100"  # scripted group (container) (typed FeaturePython)
  n = 0.1
FEATURE [App::DocumentObjectGroupPython] C_element103  label="C_element : 0.204"  # scripted group (container) (typed FeaturePython)
  n = 0.204
FEATURE [App::DocumentObjectGroupPython] N_element039  label="N_element : 0.759"  # scripted group (container) (typed FeaturePython)
  n = 0.042
FEATURE [App::DocumentObjectGroupPython] O_element088  label="O_element : 0.645"  # scripted group (container) (typed FeaturePython)
  n = 0.645
FEATURE [App::DocumentObjectGroupPython] Na_element013  label="Na_element : 0.100"  # scripted group (container) (typed FeaturePython)
  n = 0.002
FEATURE [App::DocumentObjectGroupPython] P_element009  label="P_element : 0.107"  # scripted group (container) (typed FeaturePython)
  n = 0.001
FEATURE [App::DocumentObjectGroupPython] S_element020  label="S_element : 0.021"  # scripted group (container) (typed FeaturePython)
  n = 0.002
FEATURE [App::DocumentObjectGroupPython] Cl_element023  label="Cl_element : 0.590"  # scripted group (container) (typed FeaturePython)
  n = 0.003
FEATURE [App::DocumentObjectGroupPython] K_element010  label="K_element : 0.001"  # scripted group (container) (typed FeaturePython)
  n = 0.001
FEATURE [App::DocumentObjectGroupPython] G4_SKIN_ICRP  # scripted group (container) (typed FeaturePython)
  Dunit = g/cm3
  Dvalue = 1.09
  Group = -> [H_element095,C_element103,N_element039,O_element088,Na_element013,P_element009,S_element020,Cl_element023,K_element010]
  conduct = 2
  density = 1
  expand = 3
  formula = G4_SKIN_ICRP
  name = G4_SKIN_ICRP
  specific = 4
FEATURE [App::DocumentObjectGroupPython] Na_element014  label="Na_element : 2"  # scripted group (container) (typed FeaturePython)
  n = 2
  ref = Na_element
FEATURE [App::DocumentObjectGroupPython] C_element104  label="C_element : 058"  # scripted group (container) (typed FeaturePython)
  n = 1
  ref = C_element
FEATURE [App::DocumentObjectGroupPython] O_element089  label="O_element : 049"  # scripted group (container) (typed FeaturePython)
  n = 3
  ref = O_element
FEATURE [App::DocumentObjectGroupPython] G4_SODIUM_CARBONATE  # scripted group (container) (typed FeaturePython)
  Dunit = g/cm3
  Dvalue = 2.532
  Group = -> [Na_element014,C_element104,O_element089]
  conduct = 2
  density = 1
  expand = 3
  formula = G4_SODIUM_CARBONATE
  name = G4_SODIUM_CARBONATE
  specific = 4
FEATURE [App::DocumentObjectGroupPython] Na_element015  label="Na_element : 1"  # scripted group (container) (typed FeaturePython)
  n = 1
  ref = Na_element
FEATURE [App::DocumentObjectGroupPython] I_element009  label="I_element : 005"  # scripted group (container) (typed FeaturePython)
  n = 1
  ref = I_element
FEATURE [App::DocumentObjectGroupPython] G4_SODIUM_IODIDE  # scripted group (container) (typed FeaturePython)
  Dunit = g/cm3
  Dvalue = 3.667
  Group = -> [Na_element015,I_element009]
  conduct = 2
  density = 1
  expand = 3
  formula = G4_SODIUM_IODIDE
  name = G4_SODIUM_IODIDE
  specific = 4
FEATURE [App::DocumentObjectGroupPython] Na_element016  label="Na_element : 003"  # scripted group (container) (typed FeaturePython)
  n = 2
  ref = Na_element
FEATURE [App::DocumentObjectGroupPython] O_element090  label="O_element : 050"  # scripted group (container) (typed FeaturePython)
  n = 1
  ref = O_element
FEATURE [App::DocumentObjectGroupPython] G4_SODIUM_MONOXIDE  # scripted group (container) (typed FeaturePython)
  Dunit = g/cm3
  Dvalue = 2.27
  Group = -> [Na_element016,O_element090]
  conduct = 2
  density = 1
  expand = 3
  formula = G4_SODIUM_MONOXIDE
  name = G4_SODIUM_MONOXIDE
  specific = 4
FEATURE [App::DocumentObjectGroupPython] Na_element017  label="Na_element : 004"  # scripted group (container) (typed FeaturePython)
  n = 1
  ref = Na_element
FEATURE [App::DocumentObjectGroupPython] N_element040  label="N_element : 018"  # scripted group (container) (typed FeaturePython)
  n = 1
  ref = N_element
FEATURE [App::DocumentObjectGroupPython] O_element091  label="O_element : 051"  # scripted group (container) (typed FeaturePython)
  n = 3
  ref = O_element
FEATURE [App::DocumentObjectGroupPython] G4_SODIUM_NITRATE  # scripted group (container) (typed FeaturePython)
  Dunit = g/cm3
  Dvalue = 2.261
  Group = -> [Na_element017,N_element040,O_element091]
  conduct = 2
  density = 1
  expand = 3
  formula = G4_SODIUM_NITRATE
  name = G4_SODIUM_NITRATE
  specific = 4
FEATURE [App::DocumentObjectGroupPython] C_element105  label="C_element : 059"  # scripted group (container) (typed FeaturePython)
  n = 14
  ref = C_element
FEATURE [App::DocumentObjectGroupPython] H_element096  label="H_element : 053"  # scripted group (container) (typed FeaturePython)
  n = 12
  ref = H_element
FEATURE [App::DocumentObjectGroupPython] G4_STILBENE  # scripted group (container) (typed FeaturePython)
  Dunit = g/cm3
  Dvalue = 0.9707
  Group = -> [C_element105,H_element096]
  conduct = 2
  density = 1
  expand = 3
  formula = G4_STILBENE
  name = G4_STILBENE
  specific = 4
FEATURE [App::DocumentObjectGroupPython] C_element106  label="C_element : 12"  # scripted group (container) (typed FeaturePython)
  n = 12
  ref = C_element
FEATURE [App::DocumentObjectGroupPython] H_element097  label="H_element : 22"  # scripted group (container) (typed FeaturePython)
  n = 22
  ref = H_element
FEATURE [App::DocumentObjectGroupPython] O_element092  label="O_element : 11"  # scripted group (container) (typed FeaturePython)
  n = 11
  ref = O_element
FEATURE [App::DocumentObjectGroupPython] G4_SUCROSE  # scripted group (container) (typed FeaturePython)
  Dunit = g/cm3
  Dvalue = 1.5805
  Group = -> [C_element106,H_element097,O_element092]
  conduct = 2
  density = 1
  expand = 3
  formula = G4_SUCROSE
  name = G4_SUCROSE
  specific = 4
FEATURE [App::DocumentObjectGroupPython] C_element107  label="C_element : 18"  # scripted group (container) (typed FeaturePython)
  n = 18
  ref = C_element
FEATURE [App::DocumentObjectGroupPython] H_element098  label="H_element : 054"  # scripted group (container) (typed FeaturePython)
  n = 14
  ref = H_element
FEATURE [App::DocumentObjectGroupPython] G4_TERPHENYL  # scripted group (container) (typed FeaturePython)
  Dunit = g/cm3
  Dvalue = 1.24
  Group = -> [C_element107,H_element098]
  conduct = 2
  density = 1
  expand = 3
  formula = G4_TERPHENYL
  name = G4_TERPHENYL
  specific = 4
FEATURE [App::DocumentObjectGroupPython] H_element099  label="H_element : 0.146"  # scripted group (container) (typed FeaturePython)
  n = 0.106
FEATURE [App::DocumentObjectGroupPython] C_element108  label="C_element : 0.883"  # scripted group (container) (typed FeaturePython)
  n = 0.099
FEATURE [App::DocumentObjectGroupPython] N_element041  label="N_element : 0.020"  # scripted group (container) (typed FeaturePython)
  n = 0.02
FEATURE [App::DocumentObjectGroupPython] O_element093  label="O_element : 0.766"  # scripted group (container) (typed FeaturePython)
  n = 0.766
FEATURE [App::DocumentObjectGroupPython] Na_element018  label="Na_element : 0.101"  # scripted group (container) (typed FeaturePython)
  n = 0.002
FEATURE [App::DocumentObjectGroupPython] P_element010  label="P_element : 0.108"  # scripted group (container) (typed FeaturePython)
  n = 0.001
FEATURE [App::DocumentObjectGroupPython] S_element021  label="S_element : 0.022"  # scripted group (container) (typed FeaturePython)
  n = 0.002
FEATURE [App::DocumentObjectGroupPython] Cl_element024  label="Cl_element : 0.002"  # scripted group (container) (typed FeaturePython)
  n = 0.002
FEATURE [App::DocumentObjectGroupPython] K_element011  label="K_element : 0.017"  # scripted group (container) (typed FeaturePython)
  n = 0.002
FEATURE [App::DocumentObjectGroupPython] G4_TESTIS_ICRP  # scripted group (container) (typed FeaturePython)
  Dunit = g/cm3
  Dvalue = 1.04
  Group = -> [H_element099,C_element108,N_element041,O_element093,Na_element018,P_element010,S_element021,Cl_element024,K_element011]
  conduct = 2
  density = 1
  expand = 3
  formula = G4_TESTIS_ICRP
  name = G4_TESTIS_ICRP
  specific = 4
FEATURE [App::DocumentObjectGroupPython] C_element109  label="C_element : 060"  # scripted group (container) (typed FeaturePython)
  n = 2
  ref = C_element
FEATURE [App::DocumentObjectGroupPython] Cl_element025  label="Cl_element : 012"  # scripted group (container) (typed FeaturePython)
  n = 4
  ref = Cl_element
FEATURE [App::DocumentObjectGroupPython] G4_TETRACHLOROETHYLENE  # scripted group (container) (typed FeaturePython)
  Dunit = g/cm3
  Dvalue = 1.625
  Group = -> [C_element109,Cl_element025]
  conduct = 2
  density = 1
  expand = 3
  formula = G4_TETRACHLOROETHYLENE
  name = G4_TETRACHLOROETHYLENE
  specific = 4
FEATURE [App::DocumentObjectGroupPython] Tl_element001  label="Tl_element : 1"  # scripted group (container) (typed FeaturePython)
  n = 1
  ref = Tl_element
FEATURE [App::DocumentObjectGroupPython] Cl_element026  label="Cl_element : 013"  # scripted group (container) (typed FeaturePython)
  n = 1
  ref = Cl_element
FEATURE [App::DocumentObjectGroupPython] G4_THALLIUM_CHLORIDE  # scripted group (container) (typed FeaturePython)
  Dunit = g/cm3
  Dvalue = 7.004
  Group = -> [Tl_element001,Cl_element026]
  conduct = 2
  density = 1
  expand = 3
  formula = G4_THALLIUM_CHLORIDE
  name = G4_THALLIUM_CHLORIDE
  specific = 4
FEATURE [App::DocumentObjectGroupPython] H_element100  label="H_element : 0.147"  # scripted group (container) (typed FeaturePython)
  n = 0.105
FEATURE [App::DocumentObjectGroupPython] C_element110  label="C_element : 0.256"  # scripted group (container) (typed FeaturePython)
  n = 0.256
FEATURE [App::DocumentObjectGroupPython] N_element042  label="N_element : 0.760"  # scripted group (container) (typed FeaturePython)
  n = 0.027
FEATURE [App::DocumentObjectGroupPython] O_element094  label="O_element : 0.602"  # scripted group (container) (typed FeaturePython)
  n = 0.602
FEATURE [App::DocumentObjectGroupPython] Na_element019  label="Na_element : 0.102"  # scripted group (container) (typed FeaturePython)
  n = 0.001
FEATURE [App::DocumentObjectGroupPython] P_element011  label="P_element : 0.109"  # scripted group (container) (typed FeaturePython)
  n = 0.002
FEATURE [App::DocumentObjectGroupPython] S_element022  label="S_element : 0.023"  # scripted group (container) (typed FeaturePython)
  n = 0.003
FEATURE [App::DocumentObjectGroupPython] Cl_element027  label="Cl_element : 0.591"  # scripted group (container) (typed FeaturePython)
  n = 0.002
FEATURE [App::DocumentObjectGroupPython] K_element012  label="K_element : 0.018"  # scripted group (container) (typed FeaturePython)
  n = 0.002
FEATURE [App::DocumentObjectGroupPython] G4_TISSUE_SOFT_ICRP  # scripted group (container) (typed FeaturePython)
  Dunit = g/cm3
  Dvalue = 1.03
  Group = -> [H_element100,C_element110,N_element042,O_element094,Na_element019,P_element011,S_element022,Cl_element027,K_element012]
  conduct = 2
  density = 1
  expand = 3
  formula = G4_TISSUE_SOFT_ICRP
  name = G4_TISSUE_SOFT_ICRP
  specific = 4
FEATURE [App::DocumentObjectGroupPython] H_element101  label="H_element : 0.148"  # scripted group (container) (typed FeaturePython)
  n = 0.101
FEATURE [App::DocumentObjectGroupPython] C_element111  label="C_element : 0.111"  # scripted group (container) (typed FeaturePython)
  n = 0.111
FEATURE [App::DocumentObjectGroupPython] N_element043  label="N_element : 0.026"  # scripted group (container) (typed FeaturePython)
  n = 0.026
FEATURE [App::DocumentObjectGroupPython] O_element095  label="O_element : 0.762"  # scripted group (container) (typed FeaturePython)
  n = 0.762
FEATURE [App::DocumentObjectGroupPython] G4_TISSUE_SOFT_ICRU_4  label="G4_TISSUE_SOFT_ICRU-4"  # scripted group (container) (typed FeaturePython)
  Dunit = g/cm3
  Dvalue = 1
  Group = -> [H_element101,C_element111,N_element043,O_element095]
  conduct = 2
  density = 1
  expand = 3
  formula = G4_TISSUE_SOFT_ICRU-4
  name = G4_TISSUE_SOFT_ICRU-4
  specific = 4
FEATURE [App::DocumentObjectGroupPython] H_element102  label="H_element : 0.149"  # scripted group (container) (typed FeaturePython)
  n = 0.101869
FEATURE [App::DocumentObjectGroupPython] C_element112  label="C_element : 0.456"  # scripted group (container) (typed FeaturePython)
  n = 0.456179
FEATURE [App::DocumentObjectGroupPython] N_element044  label="N_element : 0.761"  # scripted group (container) (typed FeaturePython)
  n = 0.035172
FEATURE [App::DocumentObjectGroupPython] O_element096  label="O_element : 0.407"  # scripted group (container) (typed FeaturePython)
  n = 0.40678
FEATURE [App::DocumentObjectGroupPython] G4_TISSUE_METHANE  label="G4_TISSUE-METHANE"  # scripted group (container) (typed FeaturePython)
  Dunit = g/cm3
  Dvalue = 0.00106409
  Group = -> [H_element102,C_element112,N_element044,O_element096]
  conduct = 2
  density = 1
  expand = 3
  formula = G4_TISSUE-METHANE
  name = G4_TISSUE-METHANE
  specific = 4
FEATURE [App::DocumentObjectGroupPython] H_element103  label="H_element : 0.103"  # scripted group (container) (typed FeaturePython)
  n = 0.102672
FEATURE [App::DocumentObjectGroupPython] C_element113  label="C_element : 0.569"  # scripted group (container) (typed FeaturePython)
  n = 0.56894
FEATURE [App::DocumentObjectGroupPython] N_element045  label="N_element : 0.762"  # scripted group (container) (typed FeaturePython)
  n = 0.035022
FEATURE [App::DocumentObjectGroupPython] O_element097  label="O_element : 0.293"  # scripted group (container) (typed FeaturePython)
  n = 0.293366
FEATURE [App::DocumentObjectGroupPython] G4_TISSUE_PROPANE  label="G4_TISSUE-PROPANE"  # scripted group (container) (typed FeaturePython)
  Dunit = g/cm3
  Dvalue = 0.00182628
  Group = -> [H_element103,C_element113,N_element045,O_element097]
  conduct = 2
  density = 1
  expand = 3
  formula = G4_TISSUE-PROPANE
  name = G4_TISSUE-PROPANE
  specific = 4
FEATURE [App::DocumentObjectGroupPython] Ti_element003  label="Ti_element : 1"  # scripted group (container) (typed FeaturePython)
  n = 1
  ref = Ti_element
FEATURE [App::DocumentObjectGroupPython] O_element098  label="O_element : 052"  # scripted group (container) (typed FeaturePython)
  n = 2
  ref = O_element
FEATURE [App::DocumentObjectGroupPython] G4_TITANIUM_DIOXIDE  # scripted group (container) (typed FeaturePython)
  Dunit = g/cm3
  Dvalue = 4.26
  Group = -> [Ti_element003,O_element098]
  conduct = 2
  density = 1
  expand = 3
  formula = G4_TITANIUM_DIOXIDE
  name = G4_TITANIUM_DIOXIDE
  specific = 4
FEATURE [App::DocumentObjectGroupPython] C_element114  label="C_element : 061"  # scripted group (container) (typed FeaturePython)
  n = 7
  ref = C_element
FEATURE [App::DocumentObjectGroupPython] H_element104  label="H_element : 055"  # scripted group (container) (typed FeaturePython)
  n = 8
  ref = H_element
FEATURE [App::DocumentObjectGroupPython] G4_TOLUENE  # scripted group (container) (typed FeaturePython)
  Dunit = g/cm3
  Dvalue = 0.8669
  Group = -> [C_element114,H_element104]
  conduct = 2
  density = 1
  expand = 3
  formula = G4_TOLUENE
  name = G4_TOLUENE
  specific = 4
FEATURE [App::DocumentObjectGroupPython] C_element115  label="C_element : 062"  # scripted group (container) (typed FeaturePython)
  n = 2
  ref = C_element
FEATURE [App::DocumentObjectGroupPython] H_element105  label="H_element : 056"  # scripted group (container) (typed FeaturePython)
  n = 1
  ref = H_element
FEATURE [App::DocumentObjectGroupPython] Cl_element028  label="Cl_element : 014"  # scripted group (container) (typed FeaturePython)
  n = 3
  ref = Cl_element
FEATURE [App::DocumentObjectGroupPython] G4_TRICHLOROETHYLENE  # scripted group (container) (typed FeaturePython)
  Dunit = g/cm3
  Dvalue = 1.46
  Group = -> [C_element115,H_element105,Cl_element028]
  conduct = 2
  density = 1
  expand = 3
  formula = G4_TRICHLOROETHYLENE
  name = G4_TRICHLOROETHYLENE
  specific = 4
FEATURE [App::DocumentObjectGroupPython] C_element116  label="C_element : 063"  # scripted group (container) (typed FeaturePython)
  n = 6
  ref = C_element
FEATURE [App::DocumentObjectGroupPython] H_element106  label="H_element : 15"  # scripted group (container) (typed FeaturePython)
  n = 15
  ref = H_element
FEATURE [App::DocumentObjectGroupPython] O_element099  label="O_element : 053"  # scripted group (container) (typed FeaturePython)
  n = 4
  ref = O_element
FEATURE [App::DocumentObjectGroupPython] P_element012  label="P_element : 1"  # scripted group (container) (typed FeaturePython)
  n = 1
  ref = P_element
FEATURE [App::DocumentObjectGroupPython] G4_TRIETHYL_PHOSPHATE  # scripted group (container) (typed FeaturePython)
  Dunit = g/cm3
  Dvalue = 1.07
  Group = -> [C_element116,H_element106,O_element099,P_element012]
  conduct = 2
  density = 1
  expand = 3
  formula = G4_TRIETHYL_PHOSPHATE
  name = G4_TRIETHYL_PHOSPHATE
  specific = 4
FEATURE [App::DocumentObjectGroupPython] W_element003  label="W_element : 003"  # scripted group (container) (typed FeaturePython)
  n = 1
  ref = W_element
FEATURE [App::DocumentObjectGroupPython] F_element017  label="F_element : 6"  # scripted group (container) (typed FeaturePython)
  n = 6
  ref = F_element
FEATURE [App::DocumentObjectGroupPython] G4_TUNGSTEN_HEXAFLUORIDE  # scripted group (container) (typed FeaturePython)
  Dunit = g/cm3
  Dvalue = 2.4
  Group = -> [W_element003,F_element017]
  conduct = 2
  density = 1
  expand = 3
  formula = G4_TUNGSTEN_HEXAFLUORIDE
  name = G4_TUNGSTEN_HEXAFLUORIDE
  specific = 4
FEATURE [App::DocumentObjectGroupPython] U_element001  label="U_element : 1"  # scripted group (container) (typed FeaturePython)
  n = 1
  ref = U_element
FEATURE [App::DocumentObjectGroupPython] C_element117  label="C_element : 064"  # scripted group (container) (typed FeaturePython)
  n = 2
  ref = C_element
FEATURE [App::DocumentObjectGroupPython] G4_URANIUM_DICARBIDE  # scripted group (container) (typed FeaturePython)
  Dunit = g/cm3
  Dvalue = 11.28
  Group = -> [U_element001,C_element117]
  conduct = 2
  density = 1
  expand = 3
  formula = G4_URANIUM_DICARBIDE
  name = G4_URANIUM_DICARBIDE
  specific = 4
FEATURE [App::DocumentObjectGroupPython] U_element002  label="U_element : 002"  # scripted group (container) (typed FeaturePython)
  n = 1
  ref = U_element
FEATURE [App::DocumentObjectGroupPython] C_element118  label="C_element : 065"  # scripted group (container) (typed FeaturePython)
  n = 1
  ref = C_element
FEATURE [App::DocumentObjectGroupPython] G4_URANIUM_MONOCARBIDE  # scripted group (container) (typed FeaturePython)
  Dunit = g/cm3
  Dvalue = 13.63
  Group = -> [U_element002,C_element118]
  conduct = 2
  density = 1
  expand = 3
  formula = G4_URANIUM_MONOCARBIDE
  name = G4_URANIUM_MONOCARBIDE
  specific = 4
FEATURE [App::DocumentObjectGroupPython] U_element003  label="U_element : 003"  # scripted group (container) (typed FeaturePython)
  n = 1
  ref = U_element
FEATURE [App::DocumentObjectGroupPython] O_element100  label="O_element : 054"  # scripted group (container) (typed FeaturePython)
  n = 2
  ref = O_element
FEATURE [App::DocumentObjectGroupPython] G4_URANIUM_OXIDE  # scripted group (container) (typed FeaturePython)
  Dunit = g/cm3
  Dvalue = 10.96
  Group = -> [U_element003,O_element100]
  conduct = 2
  density = 1
  expand = 3
  formula = G4_URANIUM_OXIDE
  name = G4_URANIUM_OXIDE
  specific = 4
FEATURE [App::DocumentObjectGroupPython] C_element119  label="C_element : 066"  # scripted group (container) (typed FeaturePython)
  n = 1
  ref = C_element
FEATURE [App::DocumentObjectGroupPython] H_element107  label="H_element : 057"  # scripted group (container) (typed FeaturePython)
  n = 4
  ref = H_element
FEATURE [App::DocumentObjectGroupPython] N_element046  label="N_element : 019"  # scripted group (container) (typed FeaturePython)
  n = 2
  ref = N_element
FEATURE [App::DocumentObjectGroupPython] O_element101  label="O_element : 055"  # scripted group (container) (typed FeaturePython)
  n = 1
  ref = O_element
FEATURE [App::DocumentObjectGroupPython] G4_UREA  # scripted group (container) (typed FeaturePython)
  Dunit = g/cm3
  Dvalue = 1.323
  Group = -> [C_element119,H_element107,N_element046,O_element101]
  conduct = 2
  density = 1
  expand = 3
  formula = G4_UREA
  name = G4_UREA
  specific = 4
FEATURE [App::DocumentObjectGroupPython] C_element120  label="C_element : 067"  # scripted group (container) (typed FeaturePython)
  n = 5
  ref = C_element
FEATURE [App::DocumentObjectGroupPython] H_element108  label="H_element : 058"  # scripted group (container) (typed FeaturePython)
  n = 11
  ref = H_element
FEATURE [App::DocumentObjectGroupPython] N_element047  label="N_element : 020"  # scripted group (container) (typed FeaturePython)
  n = 1
  ref = N_element
FEATURE [App::DocumentObjectGroupPython] O_element102  label="O_element : 056"  # scripted group (container) (typed FeaturePython)
  n = 2
  ref = O_element
FEATURE [App::DocumentObjectGroupPython] G4_VALINE  # scripted group (container) (typed FeaturePython)
  Dunit = g/cm3
  Dvalue = 1.23
  Group = -> [C_element120,H_element108,N_element047,O_element102]
  conduct = 2
  density = 1
  expand = 3
  formula = G4_VALINE
  name = G4_VALINE
  specific = 4
FEATURE [App::DocumentObjectGroupPython] H_element109  label="H_element : 0.009"  # scripted group (container) (typed FeaturePython)
  n = 0.009417
FEATURE [App::DocumentObjectGroupPython] C_element121  label="C_element : 0.281"  # scripted group (container) (typed FeaturePython)
  n = 0.280555
FEATURE [App::DocumentObjectGroupPython] F_element018  label="F_element : 0.710"  # scripted group (container) (typed FeaturePython)
  n = 0.710028
FEATURE [App::DocumentObjectGroupPython] G4_VITON  # scripted group (container) (typed FeaturePython)
  Dunit = g/cm3
  Dvalue = 1.8
  Group = -> [H_element109,C_element121,F_element018]
  conduct = 2
  density = 1
  expand = 3
  formula = G4_VITON
  name = G4_VITON
  specific = 4
FEATURE [App::DocumentObjectGroupPython] H_element110  label="H_element : 059"  # scripted group (container) (typed FeaturePython)
  n = 2
  ref = H_element
FEATURE [App::DocumentObjectGroupPython] O_element103  label="O_element : 057"  # scripted group (container) (typed FeaturePython)
  n = 1
  ref = O_element
FEATURE [App::DocumentObjectGroupPython] G4_WATER  # scripted group (container) (typed FeaturePython)
  Dunit = g/cm3
  Dvalue = 1
  Group = -> [H_element110,O_element103]
  conduct = 2
  density = 1
  expand = 3
  formula = G4_WATER
  name = G4_WATER
  specific = 4
FEATURE [App::DocumentObjectGroupPython] H_element111  label="H_element : 060"  # scripted group (container) (typed FeaturePython)
  n = 2
  ref = H_element
FEATURE [App::DocumentObjectGroupPython] O_element104  label="O_element : 058"  # scripted group (container) (typed FeaturePython)
  n = 1
  ref = O_element
FEATURE [App::DocumentObjectGroupPython] G4_WATER_VAPOR  # scripted group (container) (typed FeaturePython)
  Dunit = g/cm3
  Dvalue = 0.000756182
  Group = -> [H_element111,O_element104]
  conduct = 2
  density = 1
  expand = 3
  formula = G4_WATER_VAPOR
  name = G4_WATER_VAPOR
  specific = 4
FEATURE [App::DocumentObjectGroupPython] C_element122  label="C_element : 068"  # scripted group (container) (typed FeaturePython)
  n = 8
  ref = C_element
FEATURE [App::DocumentObjectGroupPython] H_element112  label="H_element : 061"  # scripted group (container) (typed FeaturePython)
  n = 10
  ref = H_element
FEATURE [App::DocumentObjectGroupPython] G4_XYLENE  # scripted group (container) (typed FeaturePython)
  Dunit = g/cm3
  Dvalue = 0.87
  Group = -> [C_element122,H_element112]
  conduct = 2
  density = 1
  expand = 3
  formula = G4_XYLENE
  name = G4_XYLENE
  specific = 4
FEATURE [App::DocumentObjectGroupPython] C_element123  label="C_element : 069"  # scripted group (container) (typed FeaturePython)
  n = 1
  ref = C_element
FEATURE [App::DocumentObjectGroupPython] G4_GRAPHITE  # scripted group (container) (typed FeaturePython)
  Dunit = g/cm3
  Dvalue = 2.21
  Group = -> [C_element123]
  conduct = 2
  density = 1
  expand = 3
  formula = G4_GRAPHITE
  name = G4_GRAPHITE
  specific = 4
FEATURE [App::DocumentObjectGroupPython] NIST  # scripted group (container) (typed FeaturePython)
  Group = -> [G4_A_150_TISSUE,G4_ACETONE,G4_ACETYLENE,G4_ADENINE,G4_ADIPOSE_TISSUE_ICRP,G4_AIR,G4_ALANINE,G4_ALUMINUM_OXIDE,G4_AMBER,G4_AMMONIA,G4_ANILINE,G4_ANTHRACENE,G4_B_100_BONE,G4_BAKELITE,G4_BARIUM_FLUORIDE,G4_BARIUM_SULFATE,G4_BENZENE,G4_BERYLLIUM_OXIDE,G4_BGO,G4_BLOOD_ICRP,G4_BONE_COMPACT_ICRU,G4_BONE_CORTICAL_ICRP,G4_BORON_CARBIDE,G4_BORON_OXIDE,G4_BRAIN_ICRP,G4_BUTANE,G4_N_BUTYL_ALCOHOL,G4_C_552,+152 more]
FEATURE [App::DocumentObjectGroupPython] H_element113  label="H_element : 062"  # scripted group (container) (typed FeaturePython)
  n = 1
  ref = H_element
FEATURE [App::DocumentObjectGroupPython] G4_H  # scripted group (container) (typed FeaturePython)
  Dunit = g/cm3
  Dvalue = 8.3748e-05
  Group = -> [H_element113]
  conduct = 2
  density = 1
  expand = 3
  formula = H
  name = G4_H
  specific = 4
FEATURE [App::DocumentObjectGroupPython] He_element001  label="He_element : 1"  # scripted group (container) (typed FeaturePython)
  n = 1
  ref = He_element
FEATURE [App::DocumentObjectGroupPython] G4_He  # scripted group (container) (typed FeaturePython)
  Dunit = g/cm3
  Dvalue = 0.000166322
  Group = -> [He_element001]
  conduct = 2
  density = 1
  expand = 3
  formula = He
  name = G4_He
  specific = 4
FEATURE [App::DocumentObjectGroupPython] Li_element008  label="Li_element : 008"  # scripted group (container) (typed FeaturePython)
  n = 1
  ref = Li_element
FEATURE [App::DocumentObjectGroupPython] G4_Li  # scripted group (container) (typed FeaturePython)
  Dunit = g/cm3
  Dvalue = 0.534
  Group = -> [Li_element008]
  conduct = 2
  density = 1
  expand = 3
  formula = Li
  name = G4_Li
  specific = 4
FEATURE [App::DocumentObjectGroupPython] Be_element002  label="Be_element : 002"  # scripted group (container) (typed FeaturePython)
  n = 1
  ref = Be_element
FEATURE [App::DocumentObjectGroupPython] G4_Be  # scripted group (container) (typed FeaturePython)
  Dunit = g/cm3
  Dvalue = 1.848
  Group = -> [Be_element002]
  conduct = 2
  density = 1
  expand = 3
  formula = Be
  name = G4_Be
  specific = 4
FEATURE [App::DocumentObjectGroupPython] B_element007  label="B_element : 007"  # scripted group (container) (typed FeaturePython)
  n = 1
  ref = B_element
FEATURE [App::DocumentObjectGroupPython] G4_B  # scripted group (container) (typed FeaturePython)
  Dunit = g/cm3
  Dvalue = 2.37
  Group = -> [B_element007]
  conduct = 2
  density = 1
  expand = 3
  formula = B
  name = G4_B
  specific = 4
FEATURE [App::DocumentObjectGroupPython] C_element124  label="C_element : 070"  # scripted group (container) (typed FeaturePython)
  n = 1
  ref = C_element
FEATURE [App::DocumentObjectGroupPython] G4_C  # scripted group (container) (typed FeaturePython)
  Dunit = g/cm3
  Dvalue = 2
  Group = -> [C_element124]
  conduct = 2
  density = 1
  expand = 3
  formula = C
  name = G4_C
  specific = 4
FEATURE [App::DocumentObjectGroupPython] N_element048  label="N_element : 021"  # scripted group (container) (typed FeaturePython)
  n = 1
  ref = N_element
FEATURE [App::DocumentObjectGroupPython] G4_N  # scripted group (container) (typed FeaturePython)
  Dunit = g/cm3
  Dvalue = 0.0011652
  Group = -> [N_element048]
  conduct = 2
  density = 1
  expand = 3
  formula = N
  name = G4_N
  specific = 4
FEATURE [App::DocumentObjectGroupPython] O_element105  label="O_element : 059"  # scripted group (container) (typed FeaturePython)
  n = 1
  ref = O_element
FEATURE [App::DocumentObjectGroupPython] G4_O  # scripted group (container) (typed FeaturePython)
  Dunit = g/cm3
  Dvalue = 0.00133151
  Group = -> [O_element105]
  conduct = 2
  density = 1
  expand = 3
  formula = O
  name = G4_O
  specific = 4
FEATURE [App::DocumentObjectGroupPython] F_element019  label="F_element : 008"  # scripted group (container) (typed FeaturePython)
  n = 1
  ref = F_element
FEATURE [App::DocumentObjectGroupPython] G4_F  # scripted group (container) (typed FeaturePython)
  Dunit = g/cm3
  Dvalue = 0.00158029
  Group = -> [F_element019]
  conduct = 2
  density = 1
  expand = 3
  formula = F
  name = G4_F
  specific = 4
FEATURE [App::DocumentObjectGroupPython] Ne_element001  label="Ne_element : 1"  # scripted group (container) (typed FeaturePython)
  n = 1
  ref = Ne_element
FEATURE [App::DocumentObjectGroupPython] G4_Ne  # scripted group (container) (typed FeaturePython)
  Dunit = g/cm3
  Dvalue = 0.000838505
  Group = -> [Ne_element001]
  conduct = 2
  density = 1
  expand = 3
  formula = Ne
  name = G4_Ne
  specific = 4
FEATURE [App::DocumentObjectGroupPython] Na_element020  label="Na_element : 005"  # scripted group (container) (typed FeaturePython)
  n = 1
  ref = Na_element
FEATURE [App::DocumentObjectGroupPython] G4_Na  # scripted group (container) (typed FeaturePython)
  Dunit = g/cm3
  Dvalue = 0.971
  Group = -> [Na_element020]
  conduct = 2
  density = 1
  expand = 3
  formula = Na
  name = G4_Na
  specific = 4
FEATURE [App::DocumentObjectGroupPython] Mg_element011  label="Mg_element : 005"  # scripted group (container) (typed FeaturePython)
  n = 1
  ref = Mg_element
FEATURE [App::DocumentObjectGroupPython] G4_Mg  # scripted group (container) (typed FeaturePython)
  Dunit = g/cm3
  Dvalue = 1.74
  Group = -> [Mg_element011]
  conduct = 2
  density = 1
  expand = 3
  formula = Mg
  name = G4_Mg
  specific = 4
FEATURE [App::DocumentObjectGroupPython] Al_element004  label="Al_element : 1"  # scripted group (container) (typed FeaturePython)
  n = 1
  ref = Al_element
FEATURE [App::DocumentObjectGroupPython] G4_Al  # scripted group (container) (typed FeaturePython)
  Dunit = g/cm3
  Dvalue = 2.699
  Group = -> [Al_element004]
  conduct = 2
  density = 1
  expand = 3
  formula = Al
  name = G4_Al
  specific = 4
FEATURE [App::DocumentObjectGroupPython] Si_element007  label="Si_element : 002"  # scripted group (container) (typed FeaturePython)
  n = 1
  ref = Si_element
FEATURE [App::DocumentObjectGroupPython] G4_Si  # scripted group (container) (typed FeaturePython)
  Dunit = g/cm3
  Dvalue = 2.33
  Group = -> [Si_element007]
  conduct = 2
  density = 1
  expand = 3
  formula = Si
  name = G4_Si
  specific = 4
FEATURE [App::DocumentObjectGroupPython] P_element013  label="P_element : 002"  # scripted group (container) (typed FeaturePython)
  n = 1
  ref = P_element
FEATURE [App::DocumentObjectGroupPython] G4_P  # scripted group (container) (typed FeaturePython)
  Dunit = g/cm3
  Dvalue = 2.2
  Group = -> [P_element013]
  conduct = 2
  density = 1
  expand = 3
  formula = P
  name = G4_P
  specific = 4
FEATURE [App::DocumentObjectGroupPython] S_element023  label="S_element : 007"  # scripted group (container) (typed FeaturePython)
  n = 1
  ref = S_element
FEATURE [App::DocumentObjectGroupPython] G4_S  # scripted group (container) (typed FeaturePython)
  Dunit = g/cm3
  Dvalue = 2
  Group = -> [S_element023]
  conduct = 2
  density = 1
  expand = 3
  formula = S
  name = G4_S
  specific = 4
FEATURE [App::DocumentObjectGroupPython] Cl_element029  label="Cl_element : 015"  # scripted group (container) (typed FeaturePython)
  n = 1
  ref = Cl_element
FEATURE [App::DocumentObjectGroupPython] G4_Cl  # scripted group (container) (typed FeaturePython)
  Dunit = g/cm3
  Dvalue = 0.00299473
  Group = -> [Cl_element029]
  conduct = 2
  density = 1
  expand = 3
  formula = Cl
  name = G4_Cl
  specific = 4
FEATURE [App::DocumentObjectGroupPython] Ar_element002  label="Ar_element : 1"  # scripted group (container) (typed FeaturePython)
  n = 1
  ref = Ar_element
FEATURE [App::DocumentObjectGroupPython] G4_Ar  # scripted group (container) (typed FeaturePython)
  Dunit = g/cm3
  Dvalue = 0.00166201
  Group = -> [Ar_element002]
  conduct = 2
  density = 1
  expand = 3
  formula = Ar
  name = G4_Ar
  specific = 4
FEATURE [App::DocumentObjectGroupPython] K_element013  label="K_element : 003"  # scripted group (container) (typed FeaturePython)
  n = 1
  ref = K_element
FEATURE [App::DocumentObjectGroupPython] G4_K  # scripted group (container) (typed FeaturePython)
  Dunit = g/cm3
  Dvalue = 0.862
  Group = -> [K_element013]
  conduct = 2
  density = 1
  expand = 3
  formula = K
  name = G4_K
  specific = 4
FEATURE [App::DocumentObjectGroupPython] Ca_element014  label="Ca_element : 007"  # scripted group (container) (typed FeaturePython)
  n = 1
  ref = Ca_element
FEATURE [App::DocumentObjectGroupPython] G4_Ca  # scripted group (container) (typed FeaturePython)
  Dunit = g/cm3
  Dvalue = 1.55
  Group = -> [Ca_element014]
  conduct = 2
  density = 1
  expand = 3
  formula = Ca
  name = G4_Ca
  specific = 4
FEATURE [App::DocumentObjectGroupPython] Sc_element001  label="Sc_element : 1"  # scripted group (container) (typed FeaturePython)
  n = 1
  ref = Sc_element
FEATURE [App::DocumentObjectGroupPython] G4_Sc  # scripted group (container) (typed FeaturePython)
  Dunit = g/cm3
  Dvalue = 2.989
  Group = -> [Sc_element001]
  conduct = 2
  density = 1
  expand = 3
  formula = Sc
  name = G4_Sc
  specific = 4
FEATURE [App::DocumentObjectGroupPython] Ti_element004  label="Ti_element : 002"  # scripted group (container) (typed FeaturePython)
  n = 1
  ref = Ti_element
FEATURE [App::DocumentObjectGroupPython] G4_Ti  # scripted group (container) (typed FeaturePython)
  Dunit = g/cm3
  Dvalue = 4.54
  Group = -> [Ti_element004]
  conduct = 2
  density = 1
  expand = 3
  formula = Ti
  name = G4_Ti
  specific = 4
FEATURE [App::DocumentObjectGroupPython] V_element001  label="V_element : 1"  # scripted group (container) (typed FeaturePython)
  n = 1
  ref = V_element
FEATURE [App::DocumentObjectGroupPython] G4_V  # scripted group (container) (typed FeaturePython)
  Dunit = g/cm3
  Dvalue = 6.11
  Group = -> [V_element001]
  conduct = 2
  density = 1
  expand = 3
  formula = V
  name = G4_V
  specific = 4
FEATURE [App::DocumentObjectGroupPython] Cr_element001  label="Cr_element : 1"  # scripted group (container) (typed FeaturePython)
  n = 1
  ref = Cr_element
FEATURE [App::DocumentObjectGroupPython] G4_Cr  # scripted group (container) (typed FeaturePython)
  Dunit = g/cm3
  Dvalue = 7.18
  Group = -> [Cr_element001]
  conduct = 2
  density = 1
  expand = 3
  formula = Cr
  name = G4_Cr
  specific = 4
FEATURE [App::DocumentObjectGroupPython] Mn_element001  label="Mn_element : 1"  # scripted group (container) (typed FeaturePython)
  n = 1
  ref = Mn_element
FEATURE [App::DocumentObjectGroupPython] G4_Mn  # scripted group (container) (typed FeaturePython)
  Dunit = g/cm3
  Dvalue = 7.44
  Group = -> [Mn_element001]
  conduct = 2
  density = 1
  expand = 3
  formula = Mn
  name = G4_Mn
  specific = 4
FEATURE [App::DocumentObjectGroupPython] Fe_element007  label="Fe_element : 004"  # scripted group (container) (typed FeaturePython)
  n = 1
  ref = Fe_element
FEATURE [App::DocumentObjectGroupPython] G4_Fe  # scripted group (container) (typed FeaturePython)
  Dunit = g/cm3
  Dvalue = 7.874
  Group = -> [Fe_element007]
  conduct = 2
  density = 1
  expand = 3
  formula = Fe
  name = G4_Fe
  specific = 4
FEATURE [App::DocumentObjectGroupPython] Co_element001  label="Co_element : 1"  # scripted group (container) (typed FeaturePython)
  n = 1
  ref = Co_element
FEATURE [App::DocumentObjectGroupPython] G4_Co  # scripted group (container) (typed FeaturePython)
  Dunit = g/cm3
  Dvalue = 8.9
  Group = -> [Co_element001]
  conduct = 2
  density = 1
  expand = 3
  formula = Co
  name = G4_Co
  specific = 4
FEATURE [App::DocumentObjectGroupPython] Ni_element001  label="Ni_element : 1"  # scripted group (container) (typed FeaturePython)
  n = 1
  ref = Ni_element
FEATURE [App::DocumentObjectGroupPython] G4_Ni  # scripted group (container) (typed FeaturePython)
  Dunit = g/cm3
  Dvalue = 8.902
  Group = -> [Ni_element001]
  conduct = 2
  density = 1
  expand = 3
  formula = Ni
  name = G4_Ni
  specific = 4
FEATURE [App::DocumentObjectGroupPython] Cu_element001  label="Cu_element : 1"  # scripted group (container) (typed FeaturePython)
  n = 1
  ref = Cu_element
FEATURE [App::DocumentObjectGroupPython] G4_Cu  # scripted group (container) (typed FeaturePython)
  Dunit = g/cm3
  Dvalue = 8.96
  Group = -> [Cu_element001]
  conduct = 2
  density = 1
  expand = 3
  formula = Cu
  name = G4_Cu
  specific = 4
FEATURE [App::DocumentObjectGroupPython] Zn_element001  label="Zn_element : 1"  # scripted group (container) (typed FeaturePython)
  n = 1
  ref = Zn_element
FEATURE [App::DocumentObjectGroupPython] G4_Zn  # scripted group (container) (typed FeaturePython)
  Dunit = g/cm3
  Dvalue = 7.133
  Group = -> [Zn_element001]
  conduct = 2
  density = 1
  expand = 3
  formula = Zn
  name = G4_Zn
  specific = 4
FEATURE [App::DocumentObjectGroupPython] Ga_element002  label="Ga_element : 002"  # scripted group (container) (typed FeaturePython)
  n = 1
  ref = Ga_element
FEATURE [App::DocumentObjectGroupPython] G4_Ga  # scripted group (container) (typed FeaturePython)
  Dunit = g/cm3
  Dvalue = 5.904
  Group = -> [Ga_element002]
  conduct = 2
  density = 1
  expand = 3
  formula = Ga
  name = G4_Ga
  specific = 4
FEATURE [App::DocumentObjectGroupPython] Ge_element002  label="Ge_element : 1"  # scripted group (container) (typed FeaturePython)
  n = 1
  ref = Ge_element
FEATURE [App::DocumentObjectGroupPython] G4_Ge  # scripted group (container) (typed FeaturePython)
  Dunit = g/cm3
  Dvalue = 5.323
  Group = -> [Ge_element002]
  conduct = 2
  density = 1
  expand = 3
  formula = Ge
  name = G4_Ge
  specific = 4
FEATURE [App::DocumentObjectGroupPython] As_element003  label="As_element : 002"  # scripted group (container) (typed FeaturePython)
  n = 1
  ref = As_element
FEATURE [App::DocumentObjectGroupPython] G4_As  # scripted group (container) (typed FeaturePython)
  Dunit = g/cm3
  Dvalue = 5.73
  Group = -> [As_element003]
  conduct = 2
  density = 1
  expand = 3
  formula = As
  name = G4_As
  specific = 4
FEATURE [App::DocumentObjectGroupPython] Se_element001  label="Se_element : 1"  # scripted group (container) (typed FeaturePython)
  n = 1
  ref = Se_element
FEATURE [App::DocumentObjectGroupPython] G4_Se  # scripted group (container) (typed FeaturePython)
  Dunit = g/cm3
  Dvalue = 4.5
  Group = -> [Se_element001]
  conduct = 2
  density = 1
  expand = 3
  formula = Se
  name = G4_Se
  specific = 4
FEATURE [App::DocumentObjectGroupPython] Br_element007  label="Br_element : 004"  # scripted group (container) (typed FeaturePython)
  n = 1
  ref = Br_element
FEATURE [App::DocumentObjectGroupPython] G4_Br  # scripted group (container) (typed FeaturePython)
  Dunit = g/cm3
  Dvalue = 0.0070721
  Group = -> [Br_element007]
  conduct = 2
  density = 1
  expand = 3
  formula = Br
  name = G4_Br
  specific = 4
FEATURE [App::DocumentObjectGroupPython] Kr_element001  label="Kr_element : 1"  # scripted group (container) (typed FeaturePython)
  n = 1
  ref = Kr_element
FEATURE [App::DocumentObjectGroupPython] G4_Kr  # scripted group (container) (typed FeaturePython)
  Dunit = g/cm3
  Dvalue = 0.00347832
  Group = -> [Kr_element001]
  conduct = 2
  density = 1
  expand = 3
  formula = Kr
  name = G4_Kr
  specific = 4
FEATURE [App::DocumentObjectGroupPython] Rb_element001  label="Rb_element : 1"  # scripted group (container) (typed FeaturePython)
  n = 1
  ref = Rb_element
FEATURE [App::DocumentObjectGroupPython] G4_Rb  # scripted group (container) (typed FeaturePython)
  Dunit = g/cm3
  Dvalue = 1.532
  Group = -> [Rb_element001]
  conduct = 2
  density = 1
  expand = 3
  formula = Rb
  name = G4_Rb
  specific = 4
FEATURE [App::DocumentObjectGroupPython] Sr_element001  label="Sr_element : 1"  # scripted group (container) (typed FeaturePython)
  n = 1
  ref = Sr_element
FEATURE [App::DocumentObjectGroupPython] G4_Sr  # scripted group (container) (typed FeaturePython)
  Dunit = g/cm3
  Dvalue = 2.54
  Group = -> [Sr_element001]
  conduct = 2
  density = 1
  expand = 3
  formula = Sr
  name = G4_Sr
  specific = 4
FEATURE [App::DocumentObjectGroupPython] Y_element001  label="Y_element : 1"  # scripted group (container) (typed FeaturePython)
  n = 1
  ref = Y_element
FEATURE [App::DocumentObjectGroupPython] G4_Y  # scripted group (container) (typed FeaturePython)
  Dunit = g/cm3
  Dvalue = 4.469
  Group = -> [Y_element001]
  conduct = 2
  density = 1
  expand = 3
  formula = Y
  name = G4_Y
  specific = 4
FEATURE [App::DocumentObjectGroupPython] Zr_element001  label="Zr_element : 1"  # scripted group (container) (typed FeaturePython)
  n = 1
  ref = Zr_element
FEATURE [App::DocumentObjectGroupPython] G4_Zr  # scripted group (container) (typed FeaturePython)
  Dunit = g/cm3
  Dvalue = 6.506
  Group = -> [Zr_element001]
  conduct = 2
  density = 1
  expand = 3
  formula = Zr
  name = G4_Zr
  specific = 4
FEATURE [App::DocumentObjectGroupPython] Nb_element001  label="Nb_element : 1"  # scripted group (container) (typed FeaturePython)
  n = 1
  ref = Nb_element
FEATURE [App::DocumentObjectGroupPython] G4_Nb  # scripted group (container) (typed FeaturePython)
  Dunit = g/cm3
  Dvalue = 8.57
  Group = -> [Nb_element001]
  conduct = 2
  density = 1
  expand = 3
  formula = Nb
  name = G4_Nb
  specific = 4
FEATURE [App::DocumentObjectGroupPython] Mo_element001  label="Mo_element : 1"  # scripted group (container) (typed FeaturePython)
  n = 1
  ref = Mo_element
FEATURE [App::DocumentObjectGroupPython] G4_Mo  # scripted group (container) (typed FeaturePython)
  Dunit = g/cm3
  Dvalue = 10.22
  Group = -> [Mo_element001]
  conduct = 2
  density = 1
  expand = 3
  formula = Mo
  name = G4_Mo
  specific = 4
FEATURE [App::DocumentObjectGroupPython] Tc_element001  label="Tc_element : 1"  # scripted group (container) (typed FeaturePython)
  n = 1
  ref = Tc_element
FEATURE [App::DocumentObjectGroupPython] G4_Tc  # scripted group (container) (typed FeaturePython)
  Dunit = g/cm3
  Dvalue = 11.5
  Group = -> [Tc_element001]
  conduct = 2
  density = 1
  expand = 3
  formula = Tc
  name = G4_Tc
  specific = 4
FEATURE [App::DocumentObjectGroupPython] Ru_element001  label="Ru_element : 1"  # scripted group (container) (typed FeaturePython)
  n = 1
  ref = Ru_element
FEATURE [App::DocumentObjectGroupPython] G4_Ru  # scripted group (container) (typed FeaturePython)
  Dunit = g/cm3
  Dvalue = 12.41
  Group = -> [Ru_element001]
  conduct = 2
  density = 1
  expand = 3
  formula = Ru
  name = G4_Ru
  specific = 4
FEATURE [App::DocumentObjectGroupPython] Rh_element001  label="Rh_element : 1"  # scripted group (container) (typed FeaturePython)
  n = 1
  ref = Rh_element
FEATURE [App::DocumentObjectGroupPython] G4_Rh  # scripted group (container) (typed FeaturePython)
  Dunit = g/cm3
  Dvalue = 12.41
  Group = -> [Rh_element001]
  conduct = 2
  density = 1
  expand = 3
  formula = Rh
  name = G4_Rh
  specific = 4
FEATURE [App::DocumentObjectGroupPython] Pd_element001  label="Pd_element : 1"  # scripted group (container) (typed FeaturePython)
  n = 1
  ref = Pd_element
FEATURE [App::DocumentObjectGroupPython] G4_Pd  # scripted group (container) (typed FeaturePython)
  Dunit = g/cm3
  Dvalue = 12.02
  Group = -> [Pd_element001]
  conduct = 2
  density = 1
  expand = 3
  formula = Pd
  name = G4_Pd
  specific = 4
FEATURE [App::DocumentObjectGroupPython] Ag_element006  label="Ag_element : 004"  # scripted group (container) (typed FeaturePython)
  n = 1
  ref = Ag_element
FEATURE [App::DocumentObjectGroupPython] G4_Ag  # scripted group (container) (typed FeaturePython)
  Dunit = g/cm3
  Dvalue = 10.5
  Group = -> [Ag_element006]
  conduct = 2
  density = 1
  expand = 3
  formula = Ag
  name = G4_Ag
  specific = 4
FEATURE [App::DocumentObjectGroupPython] Cd_element003  label="Cd_element : 003"  # scripted group (container) (typed FeaturePython)
  n = 1
  ref = Cd_element
FEATURE [App::DocumentObjectGroupPython] G4_Cd  # scripted group (container) (typed FeaturePython)
  Dunit = g/cm3
  Dvalue = 8.65
  Group = -> [Cd_element003]
  conduct = 2
  density = 1
  expand = 3
  formula = Cd
  name = G4_Cd
  specific = 4
FEATURE [App::DocumentObjectGroupPython] In_element001  label="In_element : 1"  # scripted group (container) (typed FeaturePython)
  n = 1
  ref = In_element
FEATURE [App::DocumentObjectGroupPython] G4_In  # scripted group (container) (typed FeaturePython)
  Dunit = g/cm3
  Dvalue = 7.31
  Group = -> [In_element001]
  conduct = 2
  density = 1
  expand = 3
  formula = In
  name = G4_In
  specific = 4
FEATURE [App::DocumentObjectGroupPython] Sn_element001  label="Sn_element : 1"  # scripted group (container) (typed FeaturePython)
  n = 1
  ref = Sn_element
FEATURE [App::DocumentObjectGroupPython] G4_Sn  # scripted group (container) (typed FeaturePython)
  Dunit = g/cm3
  Dvalue = 7.31
  Group = -> [Sn_element001]
  conduct = 2
  density = 1
  expand = 3
  formula = Sn
  name = G4_Sn
  specific = 4
FEATURE [App::DocumentObjectGroupPython] Sb_element001  label="Sb_element : 1"  # scripted group (container) (typed FeaturePython)
  n = 1
  ref = Sb_element
FEATURE [App::DocumentObjectGroupPython] G4_Sb  # scripted group (container) (typed FeaturePython)
  Dunit = g/cm3
  Dvalue = 6.691
  Group = -> [Sb_element001]
  conduct = 2
  density = 1
  expand = 3
  formula = Sb
  name = G4_Sb
  specific = 4
FEATURE [App::DocumentObjectGroupPython] Te_element002  label="Te_element : 002"  # scripted group (container) (typed FeaturePython)
  n = 1
  ref = Te_element
FEATURE [App::DocumentObjectGroupPython] G4_Te  # scripted group (container) (typed FeaturePython)
  Dunit = g/cm3
  Dvalue = 6.24
  Group = -> [Te_element002]
  conduct = 2
  density = 1
  expand = 3
  formula = Te
  name = G4_Te
  specific = 4
FEATURE [App::DocumentObjectGroupPython] I_element010  label="I_element : 006"  # scripted group (container) (typed FeaturePython)
  n = 1
  ref = I_element
FEATURE [App::DocumentObjectGroupPython] G4_I  # scripted group (container) (typed FeaturePython)
  Dunit = g/cm3
  Dvalue = 4.93
  Group = -> [I_element010]
  conduct = 2
  density = 1
  expand = 3
  formula = I
  name = G4_I
  specific = 4
FEATURE [App::DocumentObjectGroupPython] Xe_element001  label="Xe_element : 1"  # scripted group (container) (typed FeaturePython)
  n = 1
  ref = Xe_element
FEATURE [App::DocumentObjectGroupPython] G4_Xe  # scripted group (container) (typed FeaturePython)
  Dunit = g/cm3
  Dvalue = 0.00548536
  Group = -> [Xe_element001]
  conduct = 2
  density = 1
  expand = 3
  formula = Xe
  name = G4_Xe
  specific = 4
FEATURE [App::DocumentObjectGroupPython] Cs_element003  label="Cs_element : 003"  # scripted group (container) (typed FeaturePython)
  n = 1
  ref = Cs_element
FEATURE [App::DocumentObjectGroupPython] G4_Cs  # scripted group (container) (typed FeaturePython)
  Dunit = g/cm3
  Dvalue = 1.873
  Group = -> [Cs_element003]
  conduct = 2
  density = 1
  expand = 3
  formula = Cs
  name = G4_Cs
  specific = 4
FEATURE [App::DocumentObjectGroupPython] Ba_element003  label="Ba_element : 003"  # scripted group (container) (typed FeaturePython)
  n = 1
  ref = Ba_element
FEATURE [App::DocumentObjectGroupPython] G4_Ba  # scripted group (container) (typed FeaturePython)
  Dunit = g/cm3
  Dvalue = 3.5
  Group = -> [Ba_element003]
  conduct = 2
  density = 1
  expand = 3
  formula = Ba
  name = G4_Ba
  specific = 4
FEATURE [App::DocumentObjectGroupPython] La_element003  label="La_element : 003"  # scripted group (container) (typed FeaturePython)
  n = 1
  ref = La_element
FEATURE [App::DocumentObjectGroupPython] G4_La  # scripted group (container) (typed FeaturePython)
  Dunit = g/cm3
  Dvalue = 6.154
  Group = -> [La_element003]
  conduct = 2
  density = 1
  expand = 3
  formula = La
  name = G4_La
  specific = 4
FEATURE [App::DocumentObjectGroupPython] Ce_element002  label="Ce_element : 1"  # scripted group (container) (typed FeaturePython)
  n = 1
  ref = Ce_element
FEATURE [App::DocumentObjectGroupPython] G4_Ce  # scripted group (container) (typed FeaturePython)
  Dunit = g/cm3
  Dvalue = 6.657
  Group = -> [Ce_element002]
  conduct = 2
  density = 1
  expand = 3
  formula = Ce
  name = G4_Ce
  specific = 4
FEATURE [App::DocumentObjectGroupPython] Pr_element001  label="Pr_element : 1"  # scripted group (container) (typed FeaturePython)
  n = 1
  ref = Pr_element
FEATURE [App::DocumentObjectGroupPython] G4_Pr  # scripted group (container) (typed FeaturePython)
  Dunit = g/cm3
  Dvalue = 6.71
  Group = -> [Pr_element001]
  conduct = 2
  density = 1
  expand = 3
  formula = Pr
  name = G4_Pr
  specific = 4
FEATURE [App::DocumentObjectGroupPython] Nd_element001  label="Nd_element : 1"  # scripted group (container) (typed FeaturePython)
  n = 1
  ref = Nd_element
FEATURE [App::DocumentObjectGroupPython] G4_Nd  # scripted group (container) (typed FeaturePython)
  Dunit = g/cm3
  Dvalue = 6.9
  Group = -> [Nd_element001]
  conduct = 2
  density = 1
  expand = 3
  formula = Nd
  name = G4_Nd
  specific = 4
FEATURE [App::DocumentObjectGroupPython] Pm_element001  label="Pm_element : 1"  # scripted group (container) (typed FeaturePython)
  n = 1
  ref = Pm_element
FEATURE [App::DocumentObjectGroupPython] G4_Pm  # scripted group (container) (typed FeaturePython)
  Dunit = g/cm3
  Dvalue = 7.22
  Group = -> [Pm_element001]
  conduct = 2
  density = 1
  expand = 3
  formula = Pm
  name = G4_Pm
  specific = 4
FEATURE [App::DocumentObjectGroupPython] Sm_element001  label="Sm_element : 1"  # scripted group (container) (typed FeaturePython)
  n = 1
  ref = Sm_element
FEATURE [App::DocumentObjectGroupPython] G4_Sm  # scripted group (container) (typed FeaturePython)
  Dunit = g/cm3
  Dvalue = 7.46
  Group = -> [Sm_element001]
  conduct = 2
  density = 1
  expand = 3
  formula = Sm
  name = G4_Sm
  specific = 4
FEATURE [App::DocumentObjectGroupPython] Eu_element001  label="Eu_element : 1"  # scripted group (container) (typed FeaturePython)
  n = 1
  ref = Eu_element
FEATURE [App::DocumentObjectGroupPython] G4_Eu  # scripted group (container) (typed FeaturePython)
  Dunit = g/cm3
  Dvalue = 5.243
  Group = -> [Eu_element001]
  conduct = 2
  density = 1
  expand = 3
  formula = Eu
  name = G4_Eu
  specific = 4
FEATURE [App::DocumentObjectGroupPython] Gd_element002  label="Gd_element : 1"  # scripted group (container) (typed FeaturePython)
  n = 1
  ref = Gd_element
FEATURE [App::DocumentObjectGroupPython] G4_Gd  # scripted group (container) (typed FeaturePython)
  Dunit = g/cm3
  Dvalue = 7.9004
  Group = -> [Gd_element002]
  conduct = 2
  density = 1
  expand = 3
  formula = Gd
  name = G4_Gd
  specific = 4
FEATURE [App::DocumentObjectGroupPython] Tb_element001  label="Tb_element : 1"  # scripted group (container) (typed FeaturePython)
  n = 1
  ref = Tb_element
FEATURE [App::DocumentObjectGroupPython] G4_Tb  # scripted group (container) (typed FeaturePython)
  Dunit = g/cm3
  Dvalue = 8.229
  Group = -> [Tb_element001]
  conduct = 2
  density = 1
  expand = 3
  formula = Tb
  name = G4_Tb
  specific = 4
FEATURE [App::DocumentObjectGroupPython] Dy_element001  label="Dy_element : 1"  # scripted group (container) (typed FeaturePython)
  n = 1
  ref = Dy_element
FEATURE [App::DocumentObjectGroupPython] G4_Dy  # scripted group (container) (typed FeaturePython)
  Dunit = g/cm3
  Dvalue = 8.55
  Group = -> [Dy_element001]
  conduct = 2
  density = 1
  expand = 3
  formula = Dy
  name = G4_Dy
  specific = 4
FEATURE [App::DocumentObjectGroupPython] Ho_element001  label="Ho_element : 1"  # scripted group (container) (typed FeaturePython)
  n = 1
  ref = Ho_element
FEATURE [App::DocumentObjectGroupPython] G4_Ho  # scripted group (container) (typed FeaturePython)
  Dunit = g/cm3
  Dvalue = 8.795
  Group = -> [Ho_element001]
  conduct = 2
  density = 1
  expand = 3
  formula = Ho
  name = G4_Ho
  specific = 4
FEATURE [App::DocumentObjectGroupPython] Er_element001  label="Er_element : 1"  # scripted group (container) (typed FeaturePython)
  n = 1
  ref = Er_element
FEATURE [App::DocumentObjectGroupPython] G4_Er  # scripted group (container) (typed FeaturePython)
  Dunit = g/cm3
  Dvalue = 9.066
  Group = -> [Er_element001]
  conduct = 2
  density = 1
  expand = 3
  formula = Er
  name = G4_Er
  specific = 4
FEATURE [App::DocumentObjectGroupPython] Tm_element001  label="Tm_element : 1"  # scripted group (container) (typed FeaturePython)
  n = 1
  ref = Tm_element
FEATURE [App::DocumentObjectGroupPython] G4_Tm  # scripted group (container) (typed FeaturePython)
  Dunit = g/cm3
  Dvalue = 9.321
  Group = -> [Tm_element001]
  conduct = 2
  density = 1
  expand = 3
  formula = Tm
  name = G4_Tm
  specific = 4
FEATURE [App::DocumentObjectGroupPython] Yb_element001  label="Yb_element : 1"  # scripted group (container) (typed FeaturePython)
  n = 1
  ref = Yb_element
FEATURE [App::DocumentObjectGroupPython] G4_Yb  # scripted group (container) (typed FeaturePython)
  Dunit = g/cm3
  Dvalue = 6.73
  Group = -> [Yb_element001]
  conduct = 2
  density = 1
  expand = 3
  formula = Yb
  name = G4_Yb
  specific = 4
FEATURE [App::DocumentObjectGroupPython] Lu_element001  label="Lu_element : 1"  # scripted group (container) (typed FeaturePython)
  n = 1
  ref = Lu_element
FEATURE [App::DocumentObjectGroupPython] G4_Lu  # scripted group (container) (typed FeaturePython)
  Dunit = g/cm3
  Dvalue = 9.84
  Group = -> [Lu_element001]
  conduct = 2
  density = 1
  expand = 3
  formula = Lu
  name = G4_Lu
  specific = 4
FEATURE [App::DocumentObjectGroupPython] Hf_element001  label="Hf_element : 1"  # scripted group (container) (typed FeaturePython)
  n = 1
  ref = Hf_element
FEATURE [App::DocumentObjectGroupPython] G4_Hf  # scripted group (container) (typed FeaturePython)
  Dunit = g/cm3
  Dvalue = 13.31
  Group = -> [Hf_element001]
  conduct = 2
  density = 1
  expand = 3
  formula = Hf
  name = G4_Hf
  specific = 4
FEATURE [App::DocumentObjectGroupPython] Ta_element001  label="Ta_element : 1"  # scripted group (container) (typed FeaturePython)
  n = 1
  ref = Ta_element
FEATURE [App::DocumentObjectGroupPython] G4_Ta  # scripted group (container) (typed FeaturePython)
  Dunit = g/cm3
  Dvalue = 16.654
  Group = -> [Ta_element001]
  conduct = 2
  density = 1
  expand = 3
  formula = Ta
  name = G4_Ta
  specific = 4
FEATURE [App::DocumentObjectGroupPython] W_element004  label="W_element : 004"  # scripted group (container) (typed FeaturePython)
  n = 1
  ref = W_element
FEATURE [App::DocumentObjectGroupPython] G4_W  # scripted group (container) (typed FeaturePython)
  Dunit = g/cm3
  Dvalue = 19.3
  Group = -> [W_element004]
  conduct = 2
  density = 1
  expand = 3
  formula = W
  name = G4_W
  specific = 4
FEATURE [App::DocumentObjectGroupPython] Re_element001  label="Re_element : 1"  # scripted group (container) (typed FeaturePython)
  n = 1
  ref = Re_element
FEATURE [App::DocumentObjectGroupPython] G4_Re  # scripted group (container) (typed FeaturePython)
  Dunit = g/cm3
  Dvalue = 21.02
  Group = -> [Re_element001]
  conduct = 2
  density = 1
  expand = 3
  formula = Re
  name = G4_Re
  specific = 4
FEATURE [App::DocumentObjectGroupPython] Os_element001  label="Os_element : 1"  # scripted group (container) (typed FeaturePython)
  n = 1
  ref = Os_element
FEATURE [App::DocumentObjectGroupPython] G4_Os  # scripted group (container) (typed FeaturePython)
  Dunit = g/cm3
  Dvalue = 22.57
  Group = -> [Os_element001]
  conduct = 2
  density = 1
  expand = 3
  formula = Os
  name = G4_Os
  specific = 4
FEATURE [App::DocumentObjectGroupPython] Ir_element001  label="Ir_element : 1"  # scripted group (container) (typed FeaturePython)
  n = 1
  ref = Ir_element
FEATURE [App::DocumentObjectGroupPython] G4_Ir  # scripted group (container) (typed FeaturePython)
  Dunit = g/cm3
  Dvalue = 22.42
  Group = -> [Ir_element001]
  conduct = 2
  density = 1
  expand = 3
  formula = Ir
  name = G4_Ir
  specific = 4
FEATURE [App::DocumentObjectGroupPython] Pt_element001  label="Pt_element : 1"  # scripted group (container) (typed FeaturePython)
  n = 1
  ref = Pt_element
FEATURE [App::DocumentObjectGroupPython] G4_Pt  # scripted group (container) (typed FeaturePython)
  Dunit = g/cm3
  Dvalue = 21.45
  Group = -> [Pt_element001]
  conduct = 2
  density = 1
  expand = 3
  formula = Pt
  name = G4_Pt
  specific = 4
FEATURE [App::DocumentObjectGroupPython] Au_element001  label="Au_element : 1"  # scripted group (container) (typed FeaturePython)
  n = 1
  ref = Au_element
FEATURE [App::DocumentObjectGroupPython] G4_Au  # scripted group (container) (typed FeaturePython)
  Dunit = g/cm3
  Dvalue = 19.32
  Group = -> [Au_element001]
  conduct = 2
  density = 1
  expand = 3
  formula = Au
  name = G4_Au
  specific = 4
FEATURE [App::DocumentObjectGroupPython] Hg_element002  label="Hg_element : 002"  # scripted group (container) (typed FeaturePython)
  n = 1
  ref = Hg_element
FEATURE [App::DocumentObjectGroupPython] G4_Hg  # scripted group (container) (typed FeaturePython)
  Dunit = g/cm3
  Dvalue = 13.546
  Group = -> [Hg_element002]
  conduct = 2
  density = 1
  expand = 3
  formula = Hg
  name = G4_Hg
  specific = 4
FEATURE [App::DocumentObjectGroupPython] Tl_element002  label="Tl_element : 002"  # scripted group (container) (typed FeaturePython)
  n = 1
  ref = Tl_element
FEATURE [App::DocumentObjectGroupPython] G4_Tl  # scripted group (container) (typed FeaturePython)
  Dunit = g/cm3
  Dvalue = 11.72
  Group = -> [Tl_element002]
  conduct = 2
  density = 1
  expand = 3
  formula = Tl
  name = G4_Tl
  specific = 4
FEATURE [App::DocumentObjectGroupPython] Pb_element003  label="Pb_element : 1"  # scripted group (container) (typed FeaturePython)
  n = 1
  ref = Pb_element
FEATURE [App::DocumentObjectGroupPython] G4_Pb  # scripted group (container) (typed FeaturePython)
  Dunit = g/cm3
  Dvalue = 11.35
  Group = -> [Pb_element003]
  conduct = 2
  density = 1
  expand = 3
  formula = Pb
  name = G4_Pb
  specific = 4
FEATURE [App::DocumentObjectGroupPython] Bi_element002  label="Bi_element : 1"  # scripted group (container) (typed FeaturePython)
  n = 1
  ref = Bi_element
FEATURE [App::DocumentObjectGroupPython] G4_Bi  # scripted group (container) (typed FeaturePython)
  Dunit = g/cm3
  Dvalue = 9.747
  Group = -> [Bi_element002]
  conduct = 2
  density = 1
  expand = 3
  formula = Bi
  name = G4_Bi
  specific = 4
FEATURE [App::DocumentObjectGroupPython] Po_element001  label="Po_element : 1"  # scripted group (container) (typed FeaturePython)
  n = 1
  ref = Po_element
FEATURE [App::DocumentObjectGroupPython] G4_Po  # scripted group (container) (typed FeaturePython)
  Dunit = g/cm3
  Dvalue = 9.32
  Group = -> [Po_element001]
  conduct = 2
  density = 1
  expand = 3
  formula = Po
  name = G4_Po
  specific = 4
FEATURE [App::DocumentObjectGroupPython] At_element001  label="At_element : 1"  # scripted group (container) (typed FeaturePython)
  n = 1
  ref = At_element
FEATURE [App::DocumentObjectGroupPython] G4_At  # scripted group (container) (typed FeaturePython)
  Dunit = g/cm3
  Dvalue = 9.32
  Group = -> [At_element001]
  conduct = 2
  density = 1
  expand = 3
  formula = At
  name = G4_At
  specific = 4
FEATURE [App::DocumentObjectGroupPython] Rn_element001  label="Rn_element : 1"  # scripted group (container) (typed FeaturePython)
  n = 1
  ref = Rn_element
FEATURE [App::DocumentObjectGroupPython] G4_Rn  # scripted group (container) (typed FeaturePython)
  Dunit = g/cm3
  Dvalue = 0.00900662
  Group = -> [Rn_element001]
  conduct = 2
  density = 1
  expand = 3
  formula = Rn
  name = G4_Rn
  specific = 4
FEATURE [App::DocumentObjectGroupPython] Fr_element001  label="Fr_element : 1"  # scripted group (container) (typed FeaturePython)
  n = 1
  ref = Fr_element
FEATURE [App::DocumentObjectGroupPython] G4_Fr  # scripted group (container) (typed FeaturePython)
  Dunit = g/cm3
  Dvalue = 1
  Group = -> [Fr_element001]
  conduct = 2
  density = 1
  expand = 3
  formula = Fr
  name = G4_Fr
  specific = 4
FEATURE [App::DocumentObjectGroupPython] Ra_element001  label="Ra_element : 1"  # scripted group (container) (typed FeaturePython)
  n = 1
  ref = Ra_element
FEATURE [App::DocumentObjectGroupPython] G4_Ra  # scripted group (container) (typed FeaturePython)
  Dunit = g/cm3
  Dvalue = 5
  Group = -> [Ra_element001]
  conduct = 2
  density = 1
  expand = 3
  formula = Ra
  name = G4_Ra
  specific = 4
FEATURE [App::DocumentObjectGroupPython] Ac_element001  label="Ac_element : 1"  # scripted group (container) (typed FeaturePython)
  n = 1
  ref = Ac_element
FEATURE [App::DocumentObjectGroupPython] G4_Ac  # scripted group (container) (typed FeaturePython)
  Dunit = g/cm3
  Dvalue = 10.07
  Group = -> [Ac_element001]
  conduct = 2
  density = 1
  expand = 3
  formula = Ac
  name = G4_Ac
  specific = 4
FEATURE [App::DocumentObjectGroupPython] Th_element001  label="Th_element : 1"  # scripted group (container) (typed FeaturePython)
  n = 1
  ref = Th_element
FEATURE [App::DocumentObjectGroupPython] G4_Th  # scripted group (container) (typed FeaturePython)
  Dunit = g/cm3
  Dvalue = 11.72
  Group = -> [Th_element001]
  conduct = 2
  density = 1
  expand = 3
  formula = Th
  name = G4_Th
  specific = 4
FEATURE [App::DocumentObjectGroupPython] Pa_element001  label="Pa_element : 1"  # scripted group (container) (typed FeaturePython)
  n = 1
  ref = Pa_element
FEATURE [App::DocumentObjectGroupPython] G4_Pa  # scripted group (container) (typed FeaturePython)
  Dunit = g/cm3
  Dvalue = 15.37
  Group = -> [Pa_element001]
  conduct = 2
  density = 1
  expand = 3
  formula = Pa
  name = G4_Pa
  specific = 4
FEATURE [App::DocumentObjectGroupPython] U_element004  label="U_element : 004"  # scripted group (container) (typed FeaturePython)
  n = 1
  ref = U_element
FEATURE [App::DocumentObjectGroupPython] G4_U  # scripted group (container) (typed FeaturePython)
  Dunit = g/cm3
  Dvalue = 18.95
  Group = -> [U_element004]
  conduct = 2
  density = 1
  expand = 3
  formula = U
  name = G4_U
  specific = 4
FEATURE [App::DocumentObjectGroupPython] Np_element001  label="Np_element : 1"  # scripted group (container) (typed FeaturePython)
  n = 1
  ref = Np_element
FEATURE [App::DocumentObjectGroupPython] G4_Np  # scripted group (container) (typed FeaturePython)
  Dunit = g/cm3
  Dvalue = 20.25
  Group = -> [Np_element001]
  conduct = 2
  density = 1
  expand = 3
  formula = Np
  name = G4_Np
  specific = 4
FEATURE [App::DocumentObjectGroupPython] Pu_element002  label="Pu_element : 002"  # scripted group (container) (typed FeaturePython)
  n = 1
  ref = Pu_element
FEATURE [App::DocumentObjectGroupPython] G4_Pu  # scripted group (container) (typed FeaturePython)
  Dunit = g/cm3
  Dvalue = 19.84
  Group = -> [Pu_element002]
  conduct = 2
  density = 1
  expand = 3
  formula = Pu
  name = G4_Pu
  specific = 4
FEATURE [App::DocumentObjectGroupPython] Am_element001  label="Am_element : 1"  # scripted group (container) (typed FeaturePython)
  n = 1
  ref = Am_element
FEATURE [App::DocumentObjectGroupPython] G4_Am  # scripted group (container) (typed FeaturePython)
  Dunit = g/cm3
  Dvalue = 13.67
  Group = -> [Am_element001]
  conduct = 2
  density = 1
  expand = 3
  formula = Am
  name = G4_Am
  specific = 4
FEATURE [App::DocumentObjectGroupPython] Cm_element001  label="Cm_element : 1"  # scripted group (container) (typed FeaturePython)
  n = 1
  ref = Cm_element
FEATURE [App::DocumentObjectGroupPython] G4_Cm  # scripted group (container) (typed FeaturePython)
  Dunit = g/cm3
  Dvalue = 13.51
  Group = -> [Cm_element001]
  conduct = 2
  density = 1
  expand = 3
  formula = Cm
  name = G4_Cm
  specific = 4
FEATURE [App::DocumentObjectGroupPython] Bk_element001  label="Bk_element : 1"  # scripted group (container) (typed FeaturePython)
  n = 1
  ref = Bk_element
FEATURE [App::DocumentObjectGroupPython] G4_Bk  # scripted group (container) (typed FeaturePython)
  Dunit = g/cm3
  Dvalue = 14
  Group = -> [Bk_element001]
  conduct = 2
  density = 1
  expand = 3
  formula = Bk
  name = G4_Bk
  specific = 4
FEATURE [App::DocumentObjectGroupPython] Cf_element001  label="Cf_element : 1"  # scripted group (container) (typed FeaturePython)
  n = 1
  ref = Cf_element
FEATURE [App::DocumentObjectGroupPython] G4_Cf  # scripted group (container) (typed FeaturePython)
  Dunit = g/cm3
  Dvalue = 10
  Group = -> [Cf_element001]
  conduct = 2
  density = 1
  expand = 3
  formula = Cf
  name = G4_Cf
  specific = 4
FEATURE [App::DocumentObjectGroupPython] Element  # scripted group (container) (typed FeaturePython)
  Group = -> [G4_H,G4_He,G4_Li,G4_Be,G4_B,G4_C,G4_N,G4_O,G4_F,G4_Ne,G4_Na,G4_Mg,G4_Al,G4_Si,G4_P,G4_S,G4_Cl,G4_Ar,G4_K,G4_Ca,G4_Sc,G4_Ti,G4_V,G4_Cr,G4_Mn,G4_Fe,G4_Co,G4_Ni,G4_Cu,G4_Zn,G4_Ga,G4_Ge,G4_As,G4_Se,G4_Br,G4_Kr,G4_Rb,G4_Sr,G4_Y,G4_Zr,G4_Nb,G4_Mo,G4_Tc,G4_Ru,G4_Rh,G4_Pd,G4_Ag,G4_Cd,G4_In,G4_Sn,G4_Sb,G4_Te,G4_I,G4_Xe,G4_Cs,G4_Ba,G4_La,G4_Ce,G4_Pr,G4_Nd,G4_Pm,G4_Sm,G4_Eu,G4_Gd,G4_Tb,G4_Dy,G4_Ho,G4_Er,+30 more]
FEATURE [App::DocumentObjectGroupPython] H_element114  label="H_element : 063"  # scripted group (container) (typed FeaturePython)
  n = 2
  ref = H_element
FEATURE [App::DocumentObjectGroupPython] G4_lH2  # scripted group (container) (typed FeaturePython)
  Dunit = g/cm3
  Dvalue = 0.0708
  Group = -> [H_element114]
  conduct = 2
  density = 1
  expand = 3
  formula = G4_lH2
  name = G4_lH2
  specific = 4
FEATURE [App::DocumentObjectGroupPython] N_element049  label="N_element : 022"  # scripted group (container) (typed FeaturePython)
  n = 2
  ref = N_element
FEATURE [App::DocumentObjectGroupPython] G4_lN2  # scripted group (container) (typed FeaturePython)
  Dunit = g/cm3
  Dvalue = 0.807
  Group = -> [N_element049]
  conduct = 2
  density = 1
  expand = 3
  formula = G4_lN2
  name = G4_lN2
  specific = 4
FEATURE [App::DocumentObjectGroupPython] O_element106  label="O_element : 060"  # scripted group (container) (typed FeaturePython)
  n = 2
  ref = O_element
FEATURE [App::DocumentObjectGroupPython] G4_lO2  # scripted group (container) (typed FeaturePython)
  Dunit = g/cm3
  Dvalue = 1.141
  Group = -> [O_element106]
  conduct = 2
  density = 1
  expand = 3
  formula = G4_lO2
  name = G4_lO2
  specific = 4
FEATURE [App::DocumentObjectGroupPython] Ar_element003  label="Ar_element : 002"  # scripted group (container) (typed FeaturePython)
  n = 1
  ref = Ar_element
FEATURE [App::DocumentObjectGroupPython] G4_lAr  # scripted group (container) (typed FeaturePython)
  Dunit = g/cm3
  Dvalue = 1.396
  Group = -> [Ar_element003]
  conduct = 2
  density = 1
  expand = 3
  formula = G4_lAr
  name = G4_lAr
  specific = 4
FEATURE [App::DocumentObjectGroupPython] Br_element008  label="Br_element : 005"  # scripted group (container) (typed FeaturePython)
  n = 1
  ref = Br_element
FEATURE [App::DocumentObjectGroupPython] G4_lBr  # scripted group (container) (typed FeaturePython)
  Dunit = g/cm3
  Dvalue = 3.1028
  Group = -> [Br_element008]
  conduct = 2
  density = 1
  expand = 3
  formula = G4_lBr
  name = G4_lBr
  specific = 4
FEATURE [App::DocumentObjectGroupPython] Kr_element002  label="Kr_element : 002"  # scripted group (container) (typed FeaturePython)
  n = 1
  ref = Kr_element
FEATURE [App::DocumentObjectGroupPython] G4_lKr  # scripted group (container) (typed FeaturePython)
  Dunit = g/cm3
  Dvalue = 2.418
  Group = -> [Kr_element002]
  conduct = 2
  density = 1
  expand = 3
  formula = G4_lKr
  name = G4_lKr
  specific = 4
FEATURE [App::DocumentObjectGroupPython] Xe_element002  label="Xe_element : 002"  # scripted group (container) (typed FeaturePython)
  n = 1
  ref = Xe_element
FEATURE [App::DocumentObjectGroupPython] G4_lXe  # scripted group (container) (typed FeaturePython)
  Dunit = g/cm3
  Dvalue = 2.953
  Group = -> [Xe_element002]
  conduct = 2
  density = 1
  expand = 3
  formula = G4_lXe
  name = G4_lXe
  specific = 4
FEATURE [App::DocumentObjectGroupPython] O_element107  label="O_element : 061"  # scripted group (container) (typed FeaturePython)
  n = 4
  ref = O_element
FEATURE [App::DocumentObjectGroupPython] Pb_element004  label="Pb_element : 002"  # scripted group (container) (typed FeaturePython)
  n = 1
  ref = Pb_element
FEATURE [App::DocumentObjectGroupPython] W_element005  label="W_element : 005"  # scripted group (container) (typed FeaturePython)
  n = 1
  ref = W_element
FEATURE [App::DocumentObjectGroupPython] G4_PbWO4  # scripted group (container) (typed FeaturePython)
  Dunit = g/cm3
  Dvalue = 8.28
  Group = -> [O_element107,Pb_element004,W_element005]
  conduct = 2
  density = 1
  expand = 3
  formula = G4_PbWO4
  name = G4_PbWO4
  specific = 4
FEATURE [App::DocumentObjectGroupPython] H_element115  label="H_element : 064"  # scripted group (container) (typed FeaturePython)
  n = 1
  ref = H_element
FEATURE [App::DocumentObjectGroupPython] G4_Galactic  # scripted group (container) (typed FeaturePython)
  Dunit = g/cm3
  Dvalue = 0
  Group = -> [H_element115]
  conduct = 2
  density = 1
  expand = 3
  formula = G4_Galactic
  name = G4_Galactic
  specific = 4
FEATURE [App::DocumentObjectGroupPython] C_element125  label="C_element : 071"  # scripted group (container) (typed FeaturePython)
  n = 1
  ref = C_element
FEATURE [App::DocumentObjectGroupPython] G4_GRAPHITE_POROUS  # scripted group (container) (typed FeaturePython)
  Dunit = g/cm3
  Dvalue = 1.7
  Group = -> [C_element125]
  conduct = 2
  density = 1
  expand = 3
  formula = G4_GRAPHITE_POROUS
  name = G4_GRAPHITE_POROUS
  specific = 4
FEATURE [App::DocumentObjectGroupPython] H_element116  label="H_element : 0.150"  # scripted group (container) (typed FeaturePython)
  n = 0.080538
FEATURE [App::DocumentObjectGroupPython] C_element126  label="C_element : 0.600"  # scripted group (container) (typed FeaturePython)
  n = 0.599848
FEATURE [App::DocumentObjectGroupPython] O_element108  label="O_element : 0.320"  # scripted group (container) (typed FeaturePython)
  n = 0.319614
FEATURE [App::DocumentObjectGroupPython] G4_LUCITE  # scripted group (container) (typed FeaturePython)
  Dunit = g/cm3
  Dvalue = 1.19
  Group = -> [H_element116,C_element126,O_element108]
  conduct = 2
  density = 1
  expand = 3
  formula = G4_LUCITE
  name = G4_LUCITE
  specific = 4
FEATURE [App::DocumentObjectGroupPython] Cu_element002  label="Cu_element : 62"  # scripted group (container) (typed FeaturePython)
  n = 62
  ref = Cu_element
FEATURE [App::DocumentObjectGroupPython] Zn_element002  label="Zn_element : 35"  # scripted group (container) (typed FeaturePython)
  n = 35
  ref = Zn_element
FEATURE [App::DocumentObjectGroupPython] Pb_element005  label="Pb_element : 3"  # scripted group (container) (typed FeaturePython)
  n = 3
  ref = Pb_element
FEATURE [App::DocumentObjectGroupPython] G4_BRASS  # scripted group (container) (typed FeaturePython)
  Dunit = g/cm3
  Dvalue = 8.52
  Group = -> [Cu_element002,Zn_element002,Pb_element005]
  conduct = 2
  density = 1
  expand = 3
  formula = G4_BRASS
  name = G4_BRASS
  specific = 4
FEATURE [App::DocumentObjectGroupPython] Cu_element003  label="Cu_element : 89"  # scripted group (container) (typed FeaturePython)
  n = 89
  ref = Cu_element
FEATURE [App::DocumentObjectGroupPython] Zn_element003  label="Zn_element : 9"  # scripted group (container) (typed FeaturePython)
  n = 9
  ref = Zn_element
FEATURE [App::DocumentObjectGroupPython] Pb_element006  label="Pb_element : 2"  # scripted group (container) (typed FeaturePython)
  n = 2
  ref = Pb_element
FEATURE [App::DocumentObjectGroupPython] G4_BRONZE  # scripted group (container) (typed FeaturePython)
  Dunit = g/cm3
  Dvalue = 8.82
  Group = -> [Cu_element003,Zn_element003,Pb_element006]
  conduct = 2
  density = 1
  expand = 3
  formula = G4_BRONZE
  name = G4_BRONZE
  specific = 4
FEATURE [App::DocumentObjectGroupPython] Fe_element008  label="Fe_element : 74"  # scripted group (container) (typed FeaturePython)
  n = 74
  ref = Fe_element
FEATURE [App::DocumentObjectGroupPython] Cr_element002  label="Cr_element : 18"  # scripted group (container) (typed FeaturePython)
  n = 18
  ref = Cr_element
FEATURE [App::DocumentObjectGroupPython] Ni_element002  label="Ni_element : 8"  # scripted group (container) (typed FeaturePython)
  n = 8
  ref = Ni_element
FEATURE [App::DocumentObjectGroupPython] G4_STAINLESS_STEEL  label="G4_STAINLESS-STEEL"  # scripted group (container) (typed FeaturePython)
  Dunit = g/cm3
  Dvalue = 8
  Group = -> [Fe_element008,Cr_element002,Ni_element002]
  conduct = 2
  density = 1
  expand = 3
  formula = G4_STAINLESS-STEEL
  name = G4_STAINLESS-STEEL
  specific = 4
FEATURE [App::DocumentObjectGroupPython] H_element117  label="H_element : 065"  # scripted group (container) (typed FeaturePython)
  n = 18
  ref = H_element
FEATURE [App::DocumentObjectGroupPython] C_element127  label="C_element : 072"  # scripted group (container) (typed FeaturePython)
  n = 12
  ref = C_element
FEATURE [App::DocumentObjectGroupPython] O_element109  label="O_element : 062"  # scripted group (container) (typed FeaturePython)
  n = 7
  ref = O_element
FEATURE [App::DocumentObjectGroupPython] G4_CR39  # scripted group (container) (typed FeaturePython)
  Dunit = g/cm3
  Dvalue = 1.32
  Group = -> [H_element117,C_element127,O_element109]
  conduct = 2
  density = 1
  expand = 3
  formula = G4_CR39
  name = G4_CR39
  specific = 4
FEATURE [App::DocumentObjectGroupPython] H_element118  label="H_element : 38"  # scripted group (container) (typed FeaturePython)
  n = 38
  ref = H_element
FEATURE [App::DocumentObjectGroupPython] C_element128  label="C_element : 073"  # scripted group (container) (typed FeaturePython)
  n = 18
  ref = C_element
FEATURE [App::DocumentObjectGroupPython] O_element110  label="O_element : 063"  # scripted group (container) (typed FeaturePython)
  n = 1
  ref = O_element
FEATURE [App::DocumentObjectGroupPython] G4_OCTADECANOL  # scripted group (container) (typed FeaturePython)
  Dunit = g/cm3
  Dvalue = 0.812
  Group = -> [H_element118,C_element128,O_element110]
  conduct = 2
  density = 1
  expand = 3
  formula = G4_OCTADECANOL
  name = G4_OCTADECANOL
  specific = 4
FEATURE [App::DocumentObjectGroupPython] HEP  # scripted group (container) (typed FeaturePython)
  Group = -> [G4_lH2,G4_lN2,G4_lO2,G4_lAr,G4_lBr,G4_lKr,G4_lXe,G4_PbWO4,G4_Galactic,G4_GRAPHITE_POROUS,G4_LUCITE,G4_BRASS,G4_BRONZE,G4_STAINLESS_STEEL,G4_CR39,G4_OCTADECANOL]
FEATURE [App::DocumentObjectGroupPython] C_element129  label="C_element : 074"  # scripted group (container) (typed FeaturePython)
  n = 14
  ref = C_element
FEATURE [App::DocumentObjectGroupPython] H_element119  label="H_element : 066"  # scripted group (container) (typed FeaturePython)
  n = 10
  ref = H_element
FEATURE [App::DocumentObjectGroupPython] O_element111  label="O_element : 064"  # scripted group (container) (typed FeaturePython)
  n = 2
  ref = O_element
FEATURE [App::DocumentObjectGroupPython] N_element050  label="N_element : 023"  # scripted group (container) (typed FeaturePython)
  n = 2
  ref = N_element
FEATURE [App::DocumentObjectGroupPython] G4_KEVLAR  # scripted group (container) (typed FeaturePython)
  Dunit = g/cm3
  Dvalue = 1.44
  Group = -> [C_element129,H_element119,O_element111,N_element050]
  conduct = 2
  density = 1
  expand = 3
  formula = G4_KEVLAR
  name = G4_KEVLAR
  specific = 4
FEATURE [App::DocumentObjectGroupPython] C_element130  label="C_element : 075"  # scripted group (container) (typed FeaturePython)
  n = 10
  ref = C_element
FEATURE [App::DocumentObjectGroupPython] H_element120  label="H_element : 067"  # scripted group (container) (typed FeaturePython)
  n = 8
  ref = H_element
FEATURE [App::DocumentObjectGroupPython] O_element112  label="O_element : 065"  # scripted group (container) (typed FeaturePython)
  n = 4
  ref = O_element
FEATURE [App::DocumentObjectGroupPython] G4_DACRON  # scripted group (container) (typed FeaturePython)
  Dunit = g/cm3
  Dvalue = 1.4
  Group = -> [C_element130,H_element120,O_element112]
  conduct = 2
  density = 1
  expand = 3
  formula = G4_DACRON
  name = G4_DACRON
  specific = 4
FEATURE [App::DocumentObjectGroupPython] C_element131  label="C_element : 076"  # scripted group (container) (typed FeaturePython)
  n = 4
  ref = C_element
FEATURE [App::DocumentObjectGroupPython] H_element121  label="H_element : 068"  # scripted group (container) (typed FeaturePython)
  n = 5
  ref = H_element
FEATURE [App::DocumentObjectGroupPython] Cl_element030  label="Cl_element : 016"  # scripted group (container) (typed FeaturePython)
  n = 1
  ref = Cl_element
FEATURE [App::DocumentObjectGroupPython] G4_NEOPRENE  # scripted group (container) (typed FeaturePython)
  Dunit = g/cm3
  Dvalue = 1.23
  Group = -> [C_element131,H_element121,Cl_element030]
  conduct = 2
  density = 1
  expand = 3
  formula = G4_NEOPRENE
  name = G4_NEOPRENE
  specific = 4
FEATURE [App::DocumentObjectGroupPython] Space  # scripted group (container) (typed FeaturePython)
  Group = -> [G4_KEVLAR,G4_DACRON,G4_NEOPRENE]
FEATURE [App::DocumentObjectGroupPython] H_element122  label="H_element : 069"  # scripted group (container) (typed FeaturePython)
  n = 5
  ref = H_element
FEATURE [App::DocumentObjectGroupPython] C_element132  label="C_element : 077"  # scripted group (container) (typed FeaturePython)
  n = 4
  ref = C_element
FEATURE [App::DocumentObjectGroupPython] N_element051  label="N_element : 3"  # scripted group (container) (typed FeaturePython)
  n = 3
  ref = N_element
FEATURE [App::DocumentObjectGroupPython] O_element113  label="O_element : 066"  # scripted group (container) (typed FeaturePython)
  n = 1
  ref = O_element
FEATURE [App::DocumentObjectGroupPython] G4_CYTOSINE  # scripted group (container) (typed FeaturePython)
  Dunit = g/cm3
  Dvalue = 1.55
  Group = -> [H_element122,C_element132,N_element051,O_element113]
  conduct = 2
  density = 1
  expand = 3
  formula = G4_CYTOSINE
  name = G4_CYTOSINE
  specific = 4
FEATURE [App::DocumentObjectGroupPython] H_element123  label="H_element : 070"  # scripted group (container) (typed FeaturePython)
  n = 6
  ref = H_element
FEATURE [App::DocumentObjectGroupPython] C_element133  label="C_element : 078"  # scripted group (container) (typed FeaturePython)
  n = 5
  ref = C_element
FEATURE [App::DocumentObjectGroupPython] N_element052  label="N_element : 024"  # scripted group (container) (typed FeaturePython)
  n = 2
  ref = N_element
FEATURE [App::DocumentObjectGroupPython] O_element114  label="O_element : 067"  # scripted group (container) (typed FeaturePython)
  n = 2
  ref = O_element
FEATURE [App::DocumentObjectGroupPython] G4_THYMINE  # scripted group (container) (typed FeaturePython)
  Dunit = g/cm3
  Dvalue = 1.23
  Group = -> [H_element123,C_element133,N_element052,O_element114]
  conduct = 2
  density = 1
  expand = 3
  formula = G4_THYMINE
  name = G4_THYMINE
  specific = 4
FEATURE [App::DocumentObjectGroupPython] H_element124  label="H_element : 071"  # scripted group (container) (typed FeaturePython)
  n = 4
  ref = H_element
FEATURE [App::DocumentObjectGroupPython] C_element134  label="C_element : 079"  # scripted group (container) (typed FeaturePython)
  n = 4
  ref = C_element
FEATURE [App::DocumentObjectGroupPython] N_element053  label="N_element : 025"  # scripted group (container) (typed FeaturePython)
  n = 2
  ref = N_element
FEATURE [App::DocumentObjectGroupPython] O_element115  label="O_element : 068"  # scripted group (container) (typed FeaturePython)
  n = 2
  ref = O_element
FEATURE [App::DocumentObjectGroupPython] G4_URACIL  # scripted group (container) (typed FeaturePython)
  Dunit = g/cm3
  Dvalue = 1.32
  Group = -> [H_element124,C_element134,N_element053,O_element115]
  conduct = 2
  density = 1
  expand = 3
  formula = G4_URACIL
  name = G4_URACIL
  specific = 4
FEATURE [App::DocumentObjectGroupPython] H_element125  label="H_element : 072"  # scripted group (container) (typed FeaturePython)
  n = 4
  ref = H_element
FEATURE [App::DocumentObjectGroupPython] C_element135  label="C_element : 080"  # scripted group (container) (typed FeaturePython)
  n = 5
  ref = C_element
FEATURE [App::DocumentObjectGroupPython] N_element054  label="N_element : 026"  # scripted group (container) (typed FeaturePython)
  n = 5
  ref = N_element
FEATURE [App::DocumentObjectGroupPython] G4_DNA_ADENINE  # scripted group (container) (typed FeaturePython)
  Dunit = g/cm3
  Dvalue = 1
  Group = -> [H_element125,C_element135,N_element054]
  conduct = 2
  density = 1
  expand = 3
  formula = G4_DNA_ADENINE
  name = G4_DNA_ADENINE
  specific = 4
FEATURE [App::DocumentObjectGroupPython] H_element126  label="H_element : 073"  # scripted group (container) (typed FeaturePython)
  n = 4
  ref = H_element
FEATURE [App::DocumentObjectGroupPython] C_element136  label="C_element : 081"  # scripted group (container) (typed FeaturePython)
  n = 5
  ref = C_element
FEATURE [App::DocumentObjectGroupPython] N_element055  label="N_element : 027"  # scripted group (container) (typed FeaturePython)
  n = 5
  ref = N_element
FEATURE [App::DocumentObjectGroupPython] O_element116  label="O_element : 069"  # scripted group (container) (typed FeaturePython)
  n = 1
  ref = O_element
FEATURE [App::DocumentObjectGroupPython] G4_DNA_GUANINE  # scripted group (container) (typed FeaturePython)
  Dunit = g/cm3
  Dvalue = 1
  Group = -> [H_element126,C_element136,N_element055,O_element116]
  conduct = 2
  density = 1
  expand = 3
  formula = G4_DNA_GUANINE
  name = G4_DNA_GUANINE
  specific = 4
FEATURE [App::DocumentObjectGroupPython] H_element127  label="H_element : 074"  # scripted group (container) (typed FeaturePython)
  n = 4
  ref = H_element
FEATURE [App::DocumentObjectGroupPython] C_element137  label="C_element : 082"  # scripted group (container) (typed FeaturePython)
  n = 4
  ref = C_element
FEATURE [App::DocumentObjectGroupPython] N_element056  label="N_element : 028"  # scripted group (container) (typed FeaturePython)
  n = 3
  ref = N_element
FEATURE [App::DocumentObjectGroupPython] O_element117  label="O_element : 070"  # scripted group (container) (typed FeaturePython)
  n = 1
  ref = O_element
FEATURE [App::DocumentObjectGroupPython] G4_DNA_CYTOSINE  # scripted group (container) (typed FeaturePython)
  Dunit = g/cm3
  Dvalue = 1
  Group = -> [H_element127,C_element137,N_element056,O_element117]
  conduct = 2
  density = 1
  expand = 3
  formula = G4_DNA_CYTOSINE
  name = G4_DNA_CYTOSINE
  specific = 4
FEATURE [App::DocumentObjectGroupPython] H_element128  label="H_element : 075"  # scripted group (container) (typed FeaturePython)
  n = 5
  ref = H_element
FEATURE [App::DocumentObjectGroupPython] C_element138  label="C_element : 083"  # scripted group (container) (typed FeaturePython)
  n = 5
  ref = C_element
FEATURE [App::DocumentObjectGroupPython] N_element057  label="N_element : 029"  # scripted group (container) (typed FeaturePython)
  n = 2
  ref = N_element
FEATURE [App::DocumentObjectGroupPython] O_element118  label="O_element : 071"  # scripted group (container) (typed FeaturePython)
  n = 2
  ref = O_element
FEATURE [App::DocumentObjectGroupPython] G4_DNA_THYMINE  # scripted group (container) (typed FeaturePython)
  Dunit = g/cm3
  Dvalue = 1
  Group = -> [H_element128,C_element138,N_element057,O_element118]
  conduct = 2
  density = 1
  expand = 3
  formula = G4_DNA_THYMINE
  name = G4_DNA_THYMINE
  specific = 4
FEATURE [App::DocumentObjectGroupPython] H_element129  label="H_element : 076"  # scripted group (container) (typed FeaturePython)
  n = 3
  ref = H_element
FEATURE [App::DocumentObjectGroupPython] C_element139  label="C_element : 084"  # scripted group (container) (typed FeaturePython)
  n = 4
  ref = C_element
FEATURE [App::DocumentObjectGroupPython] N_element058  label="N_element : 030"  # scripted group (container) (typed FeaturePython)
  n = 2
  ref = N_element
FEATURE [App::DocumentObjectGroupPython] O_element119  label="O_element : 072"  # scripted group (container) (typed FeaturePython)
  n = 2
  ref = O_element
FEATURE [App::DocumentObjectGroupPython] G4_DNA_URACIL  # scripted group (container) (typed FeaturePython)
  Dunit = g/cm3
  Dvalue = 1
  Group = -> [H_element129,C_element139,N_element058,O_element119]
  conduct = 2
  density = 1
  expand = 3
  formula = G4_DNA_URACIL
  name = G4_DNA_URACIL
  specific = 4
FEATURE [App::DocumentObjectGroupPython] H_element130  label="H_element : 077"  # scripted group (container) (typed FeaturePython)
  n = 10
  ref = H_element
FEATURE [App::DocumentObjectGroupPython] C_element140  label="C_element : 085"  # scripted group (container) (typed FeaturePython)
  n = 10
  ref = C_element
FEATURE [App::DocumentObjectGroupPython] N_element059  label="N_element : 031"  # scripted group (container) (typed FeaturePython)
  n = 5
  ref = N_element
FEATURE [App::DocumentObjectGroupPython] O_element120  label="O_element : 073"  # scripted group (container) (typed FeaturePython)
  n = 4
  ref = O_element
FEATURE [App::DocumentObjectGroupPython] G4_DNA_ADENOSINE  # scripted group (container) (typed FeaturePython)
  Dunit = g/cm3
  Dvalue = 1
  Group = -> [H_element130,C_element140,N_element059,O_element120]
  conduct = 2
  density = 1
  expand = 3
  formula = G4_DNA_ADENOSINE
  name = G4_DNA_ADENOSINE
  specific = 4
FEATURE [App::DocumentObjectGroupPython] H_element131  label="H_element : 078"  # scripted group (container) (typed FeaturePython)
  n = 10
  ref = H_element
FEATURE [App::DocumentObjectGroupPython] C_element141  label="C_element : 086"  # scripted group (container) (typed FeaturePython)
  n = 10
  ref = C_element
FEATURE [App::DocumentObjectGroupPython] N_element060  label="N_element : 032"  # scripted group (container) (typed FeaturePython)
  n = 5
  ref = N_element
FEATURE [App::DocumentObjectGroupPython] O_element121  label="O_element : 074"  # scripted group (container) (typed FeaturePython)
  n = 5
  ref = O_element
FEATURE [App::DocumentObjectGroupPython] G4_DNA_GUANOSINE  # scripted group (container) (typed FeaturePython)
  Dunit = g/cm3
  Dvalue = 1
  Group = -> [H_element131,C_element141,N_element060,O_element121]
  conduct = 2
  density = 1
  expand = 3
  formula = G4_DNA_GUANOSINE
  name = G4_DNA_GUANOSINE
  specific = 4
FEATURE [App::DocumentObjectGroupPython] H_element132  label="H_element : 079"  # scripted group (container) (typed FeaturePython)
  n = 10
  ref = H_element
FEATURE [App::DocumentObjectGroupPython] C_element142  label="C_element : 087"  # scripted group (container) (typed FeaturePython)
  n = 9
  ref = C_element
FEATURE [App::DocumentObjectGroupPython] N_element061  label="N_element : 033"  # scripted group (container) (typed FeaturePython)
  n = 3
  ref = N_element
FEATURE [App::DocumentObjectGroupPython] O_element122  label="O_element : 075"  # scripted group (container) (typed FeaturePython)
  n = 5
  ref = O_element
FEATURE [App::DocumentObjectGroupPython] G4_DNA_CYTIDINE  # scripted group (container) (typed FeaturePython)
  Dunit = g/cm3
  Dvalue = 1
  Group = -> [H_element132,C_element142,N_element061,O_element122]
  conduct = 2
  density = 1
  expand = 3
  formula = G4_DNA_CYTIDINE
  name = G4_DNA_CYTIDINE
  specific = 4
FEATURE [App::DocumentObjectGroupPython] H_element133  label="H_element : 080"  # scripted group (container) (typed FeaturePython)
  n = 9
  ref = H_element
FEATURE [App::DocumentObjectGroupPython] C_element143  label="C_element : 088"  # scripted group (container) (typed FeaturePython)
  n = 9
  ref = C_element
FEATURE [App::DocumentObjectGroupPython] N_element062  label="N_element : 034"  # scripted group (container) (typed FeaturePython)
  n = 2
  ref = N_element
FEATURE [App::DocumentObjectGroupPython] O_element123  label="O_element : 076"  # scripted group (container) (typed FeaturePython)
  n = 6
  ref = O_element
FEATURE [App::DocumentObjectGroupPython] G4_DNA_URIDINE  # scripted group (container) (typed FeaturePython)
  Dunit = g/cm3
  Dvalue = 1
  Group = -> [H_element133,C_element143,N_element062,O_element123]
  conduct = 2
  density = 1
  expand = 3
  formula = G4_DNA_URIDINE
  name = G4_DNA_URIDINE
  specific = 4
FEATURE [App::DocumentObjectGroupPython] H_element134  label="H_element : 081"  # scripted group (container) (typed FeaturePython)
  n = 11
  ref = H_element
FEATURE [App::DocumentObjectGroupPython] C_element144  label="C_element : 089"  # scripted group (container) (typed FeaturePython)
  n = 10
  ref = C_element
FEATURE [App::DocumentObjectGroupPython] N_element063  label="N_element : 035"  # scripted group (container) (typed FeaturePython)
  n = 2
  ref = N_element
FEATURE [App::DocumentObjectGroupPython] O_element124  label="O_element : 077"  # scripted group (container) (typed FeaturePython)
  n = 6
  ref = O_element
FEATURE [App::DocumentObjectGroupPython] G4_DNA_METHYLURIDINE  # scripted group (container) (typed FeaturePython)
  Dunit = g/cm3
  Dvalue = 1
  Group = -> [H_element134,C_element144,N_element063,O_element124]
  conduct = 2
  density = 1
  expand = 3
  formula = G4_DNA_METHYLURIDINE
  name = G4_DNA_METHYLURIDINE
  specific = 4
FEATURE [App::DocumentObjectGroupPython] P_element014  label="P_element : 003"  # scripted group (container) (typed FeaturePython)
  n = 1
  ref = P_element
FEATURE [App::DocumentObjectGroupPython] O_element125  label="O_element : 078"  # scripted group (container) (typed FeaturePython)
  n = 3
  ref = O_element
FEATURE [App::DocumentObjectGroupPython] G4_DNA_MONOPHOSPHATE  # scripted group (container) (typed FeaturePython)
  Dunit = g/cm3
  Dvalue = 1
  Group = -> [P_element014,O_element125]
  conduct = 2
  density = 1
  expand = 3
  formula = G4_DNA_MONOPHOSPHATE
  name = G4_DNA_MONOPHOSPHATE
  specific = 4
FEATURE [App::DocumentObjectGroupPython] H_element135  label="H_element : 082"  # scripted group (container) (typed FeaturePython)
  n = 10
  ref = H_element
FEATURE [App::DocumentObjectGroupPython] C_element145  label="C_element : 090"  # scripted group (container) (typed FeaturePython)
  n = 10
  ref = C_element
FEATURE [App::DocumentObjectGroupPython] N_element064  label="N_element : 036"  # scripted group (container) (typed FeaturePython)
  n = 5
  ref = N_element
FEATURE [App::DocumentObjectGroupPython] O_element126  label="O_element : 079"  # scripted group (container) (typed FeaturePython)
  n = 7
  ref = O_element
FEATURE [App::DocumentObjectGroupPython] P_element015  label="P_element : 004"  # scripted group (container) (typed FeaturePython)
  n = 1
  ref = P_element
FEATURE [App::DocumentObjectGroupPython] G4_DNA_A  # scripted group (container) (typed FeaturePython)
  Dunit = g/cm3
  Dvalue = 1
  Group = -> [H_element135,C_element145,N_element064,O_element126,P_element015]
  conduct = 2
  density = 1
  expand = 3
  formula = G4_DNA_A
  name = G4_DNA_A
  specific = 4
FEATURE [App::DocumentObjectGroupPython] H_element136  label="H_element : 083"  # scripted group (container) (typed FeaturePython)
  n = 10
  ref = H_element
FEATURE [App::DocumentObjectGroupPython] C_element146  label="C_element : 091"  # scripted group (container) (typed FeaturePython)
  n = 10
  ref = C_element
FEATURE [App::DocumentObjectGroupPython] N_element065  label="N_element : 037"  # scripted group (container) (typed FeaturePython)
  n = 5
  ref = N_element
FEATURE [App::DocumentObjectGroupPython] O_element127  label="O_element : 8"  # scripted group (container) (typed FeaturePython)
  n = 8
  ref = O_element
FEATURE [App::DocumentObjectGroupPython] P_element016  label="P_element : 005"  # scripted group (container) (typed FeaturePython)
  n = 1
  ref = P_element
FEATURE [App::DocumentObjectGroupPython] G4_DNA_G  # scripted group (container) (typed FeaturePython)
  Dunit = g/cm3
  Dvalue = 1
  Group = -> [H_element136,C_element146,N_element065,O_element127,P_element016]
  conduct = 2
  density = 1
  expand = 3
  formula = G4_DNA_G
  name = G4_DNA_G
  specific = 4
FEATURE [App::DocumentObjectGroupPython] H_element137  label="H_element : 084"  # scripted group (container) (typed FeaturePython)
  n = 10
  ref = H_element
FEATURE [App::DocumentObjectGroupPython] C_element147  label="C_element : 092"  # scripted group (container) (typed FeaturePython)
  n = 9
  ref = C_element
FEATURE [App::DocumentObjectGroupPython] N_element066  label="N_element : 038"  # scripted group (container) (typed FeaturePython)
  n = 3
  ref = N_element
FEATURE [App::DocumentObjectGroupPython] O_element128  label="O_element : 080"  # scripted group (container) (typed FeaturePython)
  n = 8
  ref = O_element
FEATURE [App::DocumentObjectGroupPython] P_element017  label="P_element : 006"  # scripted group (container) (typed FeaturePython)
  n = 1
  ref = P_element
FEATURE [App::DocumentObjectGroupPython] G4_DNA_C  # scripted group (container) (typed FeaturePython)
  Dunit = g/cm3
  Dvalue = 1
  Group = -> [H_element137,C_element147,N_element066,O_element128,P_element017]
  conduct = 2
  density = 1
  expand = 3
  formula = G4_DNA_C
  name = G4_DNA_C
  specific = 4
FEATURE [App::DocumentObjectGroupPython] H_element138  label="H_element : 085"  # scripted group (container) (typed FeaturePython)
  n = 9
  ref = H_element
FEATURE [App::DocumentObjectGroupPython] C_element148  label="C_element : 093"  # scripted group (container) (typed FeaturePython)
  n = 9
  ref = C_element
FEATURE [App::DocumentObjectGroupPython] N_element067  label="N_element : 039"  # scripted group (container) (typed FeaturePython)
  n = 2
  ref = N_element
FEATURE [App::DocumentObjectGroupPython] O_element129  label="O_element : 9"  # scripted group (container) (typed FeaturePython)
  n = 9
  ref = O_element
FEATURE [App::DocumentObjectGroupPython] P_element018  label="P_element : 007"  # scripted group (container) (typed FeaturePython)
  n = 1
  ref = P_element
FEATURE [App::DocumentObjectGroupPython] G4_DNA_U  # scripted group (container) (typed FeaturePython)
  Dunit = g/cm3
  Dvalue = 1
  Group = -> [H_element138,C_element148,N_element067,O_element129,P_element018]
  conduct = 2
  density = 1
  expand = 3
  formula = G4_DNA_U
  name = G4_DNA_U
  specific = 4
FEATURE [App::DocumentObjectGroupPython] H_element139  label="H_element : 086"  # scripted group (container) (typed FeaturePython)
  n = 11
  ref = H_element
FEATURE [App::DocumentObjectGroupPython] C_element149  label="C_element : 094"  # scripted group (container) (typed FeaturePython)
  n = 10
  ref = C_element
FEATURE [App::DocumentObjectGroupPython] N_element068  label="N_element : 040"  # scripted group (container) (typed FeaturePython)
  n = 2
  ref = N_element
FEATURE [App::DocumentObjectGroupPython] O_element130  label="O_element : 081"  # scripted group (container) (typed FeaturePython)
  n = 9
  ref = O_element
FEATURE [App::DocumentObjectGroupPython] P_element019  label="P_element : 008"  # scripted group (container) (typed FeaturePython)
  n = 1
  ref = P_element
FEATURE [App::DocumentObjectGroupPython] G4_DNA_MU  # scripted group (container) (typed FeaturePython)
  Dunit = g/cm3
  Dvalue = 1
  Group = -> [H_element139,C_element149,N_element068,O_element130,P_element019]
  conduct = 2
  density = 1
  expand = 3
  formula = G4_DNA_MU
  name = G4_DNA_MU
  specific = 4
FEATURE [App::DocumentObjectGroupPython] BioChemical  # scripted group (container) (typed FeaturePython)
  Group = -> [G4_CYTOSINE,G4_THYMINE,G4_URACIL,G4_DNA_ADENINE,G4_DNA_GUANINE,G4_DNA_CYTOSINE,G4_DNA_THYMINE,G4_DNA_URACIL,G4_DNA_ADENOSINE,G4_DNA_GUANOSINE,G4_DNA_CYTIDINE,G4_DNA_URIDINE,G4_DNA_METHYLURIDINE,G4_DNA_MONOPHOSPHATE,G4_DNA_A,G4_DNA_G,G4_DNA_C,G4_DNA_U,G4_DNA_MU]
FEATURE [App::DocumentObjectGroupPython] G4Materials  # scripted group (container) (typed FeaturePython)
  Group = -> [NIST,Element,HEP,Space,BioChemical]
  version = 1
FEATURE [App::DocumentObjectGroupPython] Geant4  # scripted group (container) (typed FeaturePython)
  Group = -> [G4Isotopes,G4Elements,G4Materials]
FEATURE [App::DocumentObjectGroupPython] Materials  # scripted group (container) (typed FeaturePython)
  Group = -> [Geant4]
FEATURE [Part::FeaturePython] GDMLBox_WorldBox  # WARN: FeaturePython — macro-defined, semantics opaque (R4)
  lunit = 2
  material = 5
  x = 145.922
  y = 145.922
  z = 130
FEATURE [Part::FeaturePython] GDMLBox_Box  # WARN: FeaturePython — macro-defined, semantics opaque (R4)
  lunit = 2
  material = 0
  x = 20
  y = 10
  z = 10
FEATURE [App::Part] LV_Box
  Group = -> [GDMLBox_Box]
  Origin = -> Origin001
  Placement = pos=(35,0,0) rot=(0,0,1;0.261799rad)
FEATURE [Part::FeaturePython] Array  # Draft array (typed FeaturePython)
  AlwaysSyncPlacement = false
  Angle = 360
  ArrayType = 1
  Axis = (0,0,1)
  Base = -> LV_Box
  Center = (0,0,0)
  Count = 4
  ExpandArray = false
  Fuse = false
  IntervalAxis = (0,0,0)
  IntervalX = (50,0,0)
  IntervalY = (0,50,0)
  IntervalZ = (0,0,50)
  NumberCircles = 3
  NumberPolar = 4
  NumberX = 2
  NumberY = 2
  NumberZ = 1
  PlacementList = 4 placements: [(35,0,0),(7.10543e-15,35,0),(-35,4.28626e-15,0),(-7.10543e-15,-35,0)]
  RadialDistance = 50
  ScaleList = (4) [(1,1,1),(1,1,1),(1,1,1),(1,1,1)]
  Symmetry = 1
  TangentialDistance = 25
FEATURE [App::Part] Part
  Group = -> [LV_Box,Array]
  Origin = -> Origin002
FEATURE [App::Part] worldVOL
  Group = -> [GDMLBox_WorldBox,Part]
  Origin = -> Origin
